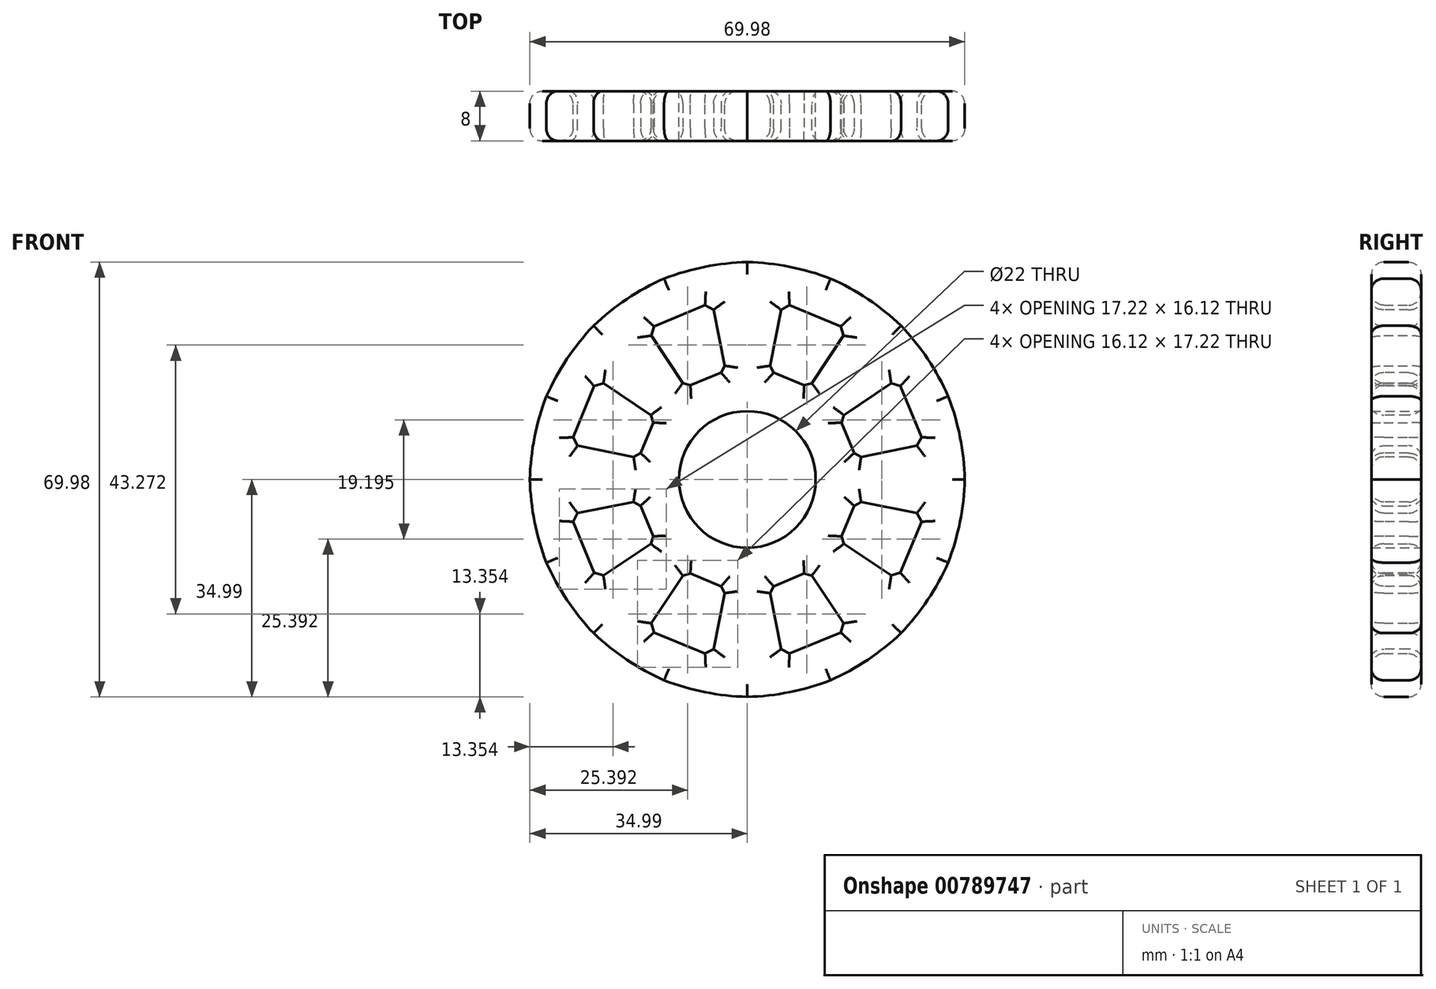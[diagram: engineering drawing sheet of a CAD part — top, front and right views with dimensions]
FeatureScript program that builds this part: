
annotation { "Feature Type Name" : "Feature", "Feature Type Description" : "" }
export const myFeature = defineFeature(function(context is Context, id is Id, definition is map)
    precondition{}
    {
        {
            var Q0;
            Q0=qCreatedBy(makeId("Front.planeOp"),FACE);
            var sketch = newSketch(context, id + "F0", { "sketchPlane" : qUnion([Q0])});
            skCircle(sketch, "E0.cCircle", {"center": v(0, 0) * mm, "radius": 35 * mm, "construction": true});
            skLineSegment(sketch, "E0.0", {"start": v(35, 6.96) * mm, "end": v(35, -6.96) * mm});
            skLineSegment(sketch, "E0.1", {"start": v(35, -6.96) * mm, "end": v(29.67, -19.83) * mm});
            skLineSegment(sketch, "E0.2", {"start": v(29.67, -19.83) * mm, "end": v(19.83, -29.67) * mm});
            skLineSegment(sketch, "E0.3", {"start": v(19.83, -29.67) * mm, "end": v(6.96, -35) * mm});
            skLineSegment(sketch, "E0.4", {"start": v(6.96, -35) * mm, "end": v(-6.96, -35) * mm});
            skLineSegment(sketch, "E0.5", {"start": v(-6.96, -35) * mm, "end": v(-19.83, -29.67) * mm});
            skLineSegment(sketch, "E0.6", {"start": v(-19.83, -29.67) * mm, "end": v(-29.67, -19.83) * mm});
            skLineSegment(sketch, "E0.7", {"start": v(-29.67, -19.83) * mm, "end": v(-35, -6.96) * mm});
            skLineSegment(sketch, "E0.8", {"start": v(-35, -6.96) * mm, "end": v(-35, 6.96) * mm});
            skLineSegment(sketch, "E0.9", {"start": v(-35, 6.96) * mm, "end": v(-29.67, 19.83) * mm});
            skLineSegment(sketch, "E0.10", {"start": v(-29.67, 19.83) * mm, "end": v(-19.83, 29.67) * mm});
            skLineSegment(sketch, "E0.11", {"start": v(-19.83, 29.67) * mm, "end": v(-6.96, 35) * mm});
            skLineSegment(sketch, "E0.12", {"start": v(-6.96, 35) * mm, "end": v(6.96, 35) * mm});
            skLineSegment(sketch, "E0.13", {"start": v(6.96, 35) * mm, "end": v(19.83, 29.67) * mm});
            skLineSegment(sketch, "E0.14", {"start": v(19.83, 29.67) * mm, "end": v(29.67, 19.83) * mm});
            skLineSegment(sketch, "E0.15", {"start": v(29.67, 19.83) * mm, "end": v(35, 6.96) * mm});
            skPoint(sketch, "E0.0.midPoint", {"position": v(35, 0) * mm});
            skCircle(sketch, "E1", {"center": v(0, 0) * mm, "radius": 11 * mm});
            skCircle(sketch, "E2.cCircle", {"center": v(0, 0) * mm, "radius": 28.5 * mm, "construction": true});
            skLineSegment(sketch, "E2.0", {"start": v(28.5, 5.67) * mm, "end": v(28.5, -5.67) * mm});
            skLineSegment(sketch, "E2.1", {"start": v(28.5, -5.67) * mm, "end": v(24.16, -16.14) * mm});
            skLineSegment(sketch, "E2.2", {"start": v(24.16, -16.14) * mm, "end": v(16.14, -24.16) * mm});
            skLineSegment(sketch, "E2.3", {"start": v(16.14, -24.16) * mm, "end": v(5.67, -28.5) * mm});
            skLineSegment(sketch, "E2.4", {"start": v(5.67, -28.5) * mm, "end": v(-5.67, -28.5) * mm});
            skLineSegment(sketch, "E2.5", {"start": v(-5.67, -28.5) * mm, "end": v(-16.14, -24.16) * mm});
            skLineSegment(sketch, "E2.6", {"start": v(-16.14, -24.16) * mm, "end": v(-24.16, -16.14) * mm});
            skLineSegment(sketch, "E2.7", {"start": v(-24.16, -16.14) * mm, "end": v(-28.5, -5.67) * mm});
            skLineSegment(sketch, "E2.8", {"start": v(-28.5, -5.67) * mm, "end": v(-28.5, 5.67) * mm});
            skLineSegment(sketch, "E2.9", {"start": v(-28.5, 5.67) * mm, "end": v(-24.16, 16.14) * mm});
            skLineSegment(sketch, "E2.10", {"start": v(-24.16, 16.14) * mm, "end": v(-16.14, 24.16) * mm});
            skLineSegment(sketch, "E2.11", {"start": v(-16.14, 24.16) * mm, "end": v(-5.67, 28.5) * mm});
            skLineSegment(sketch, "E2.12", {"start": v(-5.67, 28.5) * mm, "end": v(5.67, 28.5) * mm});
            skLineSegment(sketch, "E2.13", {"start": v(5.67, 28.5) * mm, "end": v(16.14, 24.16) * mm});
            skLineSegment(sketch, "E2.14", {"start": v(16.14, 24.16) * mm, "end": v(24.16, 16.14) * mm});
            skLineSegment(sketch, "E2.15", {"start": v(24.16, 16.14) * mm, "end": v(28.5, 5.67) * mm});
            skPoint(sketch, "E2.0.midPoint", {"position": v(28.5, 0) * mm});
            skCircle(sketch, "E3.cCircle", {"center": v(0, 0) * mm, "radius": 17.5 * mm, "construction": true});
            skLineSegment(sketch, "E3.0", {"start": v(17.5, 3.48) * mm, "end": v(17.5, -3.48) * mm});
            skLineSegment(sketch, "E3.1", {"start": v(17.5, -3.48) * mm, "end": v(14.84, -9.91) * mm});
            skLineSegment(sketch, "E3.2", {"start": v(14.84, -9.91) * mm, "end": v(9.91, -14.84) * mm});
            skLineSegment(sketch, "E3.3", {"start": v(9.91, -14.84) * mm, "end": v(3.48, -17.5) * mm});
            skLineSegment(sketch, "E3.4", {"start": v(3.48, -17.5) * mm, "end": v(-3.48, -17.5) * mm});
            skLineSegment(sketch, "E3.5", {"start": v(-3.48, -17.5) * mm, "end": v(-9.91, -14.84) * mm});
            skLineSegment(sketch, "E3.6", {"start": v(-9.91, -14.84) * mm, "end": v(-14.84, -9.91) * mm});
            skLineSegment(sketch, "E3.7", {"start": v(-14.84, -9.91) * mm, "end": v(-17.5, -3.48) * mm});
            skLineSegment(sketch, "E3.8", {"start": v(-17.5, -3.48) * mm, "end": v(-17.5, 3.48) * mm});
            skLineSegment(sketch, "E3.9", {"start": v(-17.5, 3.48) * mm, "end": v(-14.84, 9.91) * mm});
            skLineSegment(sketch, "E3.10", {"start": v(-14.84, 9.91) * mm, "end": v(-9.91, 14.84) * mm});
            skLineSegment(sketch, "E3.11", {"start": v(-9.91, 14.84) * mm, "end": v(-3.48, 17.5) * mm});
            skLineSegment(sketch, "E3.12", {"start": v(-3.48, 17.5) * mm, "end": v(3.48, 17.5) * mm});
            skLineSegment(sketch, "E3.13", {"start": v(3.48, 17.5) * mm, "end": v(9.91, 14.84) * mm});
            skLineSegment(sketch, "E3.14", {"start": v(9.91, 14.84) * mm, "end": v(14.84, 9.91) * mm});
            skLineSegment(sketch, "E3.15", {"start": v(14.84, 9.91) * mm, "end": v(17.5, 3.48) * mm});
            skPoint(sketch, "E3.0.midPoint", {"position": v(17.5, 0) * mm});
            skLineSegment(sketch, "E4", {"start": v(-3.48, 17.5) * mm, "end": v(-5.67, 28.5) * mm});
            skLineSegment(sketch, "E5", {"start": v(3.48, 17.5) * mm, "end": v(5.67, 28.5) * mm});
            skLineSegment(sketch, "E6", {"start": v(9.91, 14.84) * mm, "end": v(16.14, 24.16) * mm});
            skLineSegment(sketch, "E7", {"start": v(14.84, 9.91) * mm, "end": v(24.16, 16.14) * mm});
            skLineSegment(sketch, "E8", {"start": v(17.5, 3.48) * mm, "end": v(28.5, 5.67) * mm});
            skLineSegment(sketch, "E9", {"start": v(17.5, -3.48) * mm, "end": v(28.5, -5.67) * mm});
            skLineSegment(sketch, "E10", {"start": v(14.84, -9.91) * mm, "end": v(24.16, -16.14) * mm});
            skLineSegment(sketch, "E11", {"start": v(9.91, -14.84) * mm, "end": v(16.14, -24.16) * mm});
            skLineSegment(sketch, "E12", {"start": v(3.48, -17.5) * mm, "end": v(5.67, -28.5) * mm});
            skLineSegment(sketch, "E13", {"start": v(-3.48, -17.5) * mm, "end": v(-5.67, -28.5) * mm});
            skLineSegment(sketch, "E14", {"start": v(-9.91, -14.84) * mm, "end": v(-16.14, -24.16) * mm});
            skLineSegment(sketch, "E15", {"start": v(-14.84, -9.91) * mm, "end": v(-24.16, -16.14) * mm});
            skLineSegment(sketch, "E16", {"start": v(-17.5, -3.48) * mm, "end": v(-28.5, -5.67) * mm});
            skLineSegment(sketch, "E17", {"start": v(-17.5, 3.48) * mm, "end": v(-28.5, 5.67) * mm});
            skLineSegment(sketch, "E18", {"start": v(-14.84, 9.91) * mm, "end": v(-24.16, 16.14) * mm});
            skLineSegment(sketch, "E19", {"start": v(-9.91, 14.84) * mm, "end": v(-16.14, 24.16) * mm});
            skSolve(sketch);
        }
        {
            var Q0;
            Q0=makeQuery(id+"F0.imprint","IMPRINT",FACE,{"disambiguationData":[TD([[makeQuery(id+"F0.imprint","IMPRINT",EDGE,{"derivedFrom":sQuery(id+"F0.wireOp",EDGE,"E0.0")}),-1.0]])]});
            var Q1;
            Q1=makeQuery(id+"F0.imprint","IMPRINT",FACE,{"disambiguationData":[TD([[makeQuery(id+"F0.imprint","IMPRINT",EDGE,{"derivedFrom":sQuery(id+"F0.wireOp",EDGE,"E2.10")}),-1.0]])]});
            var Q2;
            Q2=makeQuery(id+"F0.imprint","IMPRINT",FACE,{"disambiguationData":[TD([[makeQuery(id+"F0.imprint","IMPRINT",EDGE,{"derivedFrom":sQuery(id+"F0.wireOp",EDGE,"E2.12")}),-1.0]])]});
            var Q3;
            Q3=makeQuery(id+"F0.imprint","IMPRINT",FACE,{"disambiguationData":[TD([[makeQuery(id+"F0.imprint","IMPRINT",EDGE,{"derivedFrom":sQuery(id+"F0.wireOp",EDGE,"E2.14")}),-1.0]])]});
            var Q4;
            Q4=makeQuery(id+"F0.imprint","IMPRINT",FACE,{"disambiguationData":[TD([[makeQuery(id+"F0.imprint","IMPRINT",EDGE,{"derivedFrom":sQuery(id+"F0.wireOp",EDGE,"E2.0")}),-1.0]])]});
            var Q5;
            Q5=makeQuery(id+"F0.imprint","IMPRINT",FACE,{"disambiguationData":[TD([[makeQuery(id+"F0.imprint","IMPRINT",EDGE,{"derivedFrom":sQuery(id+"F0.wireOp",EDGE,"E2.2")}),-1.0]])]});
            var Q6;
            Q6=makeQuery(id+"F0.imprint","IMPRINT",FACE,{"disambiguationData":[TD([[makeQuery(id+"F0.imprint","IMPRINT",EDGE,{"derivedFrom":sQuery(id+"F0.wireOp",EDGE,"E2.4")}),-1.0]])]});
            var Q7;
            Q7=makeQuery(id+"F0.imprint","IMPRINT",FACE,{"disambiguationData":[TD([[makeQuery(id+"F0.imprint","IMPRINT",EDGE,{"derivedFrom":sQuery(id+"F0.wireOp",EDGE,"E2.6")}),-1.0]])]});
            var Q8;
            Q8=makeQuery(id+"F0.imprint","IMPRINT",FACE,{"disambiguationData":[TD([[makeQuery(id+"F0.imprint","IMPRINT",EDGE,{"derivedFrom":sQuery(id+"F0.wireOp",EDGE,"E2.8")}),-1.0]])]});
            var Q9;
            Q9=makeQuery(id+"F0.imprint","IMPRINT",FACE,{"disambiguationData":[TD([[makeQuery(id+"F0.imprint","IMPRINT",EDGE,{"derivedFrom":sQuery(id+"F0.wireOp",EDGE,"E1")}),-1.0]])]});
            extrude(context, id + "F1", {"entities" : qUnion([Q0, Q1, Q2, Q3, Q4, Q5, Q6, Q7, Q8, Q9]), "depth" : 4 * mm, "offsetDistance" : 25 * mm});
        }
        {
            var Q0;
            Q0=makeQuery(id+"F1.opExtrude","SWEPT_EDGE",EDGE,{"disambiguationData":[OSD([sQuery(id+"F0.wireOp",EDGE,"E0.11"),sQuery(id+"F0.wireOp",EDGE,"E0.12")])]});
            var Q1;
            Q1=makeQuery(id+"F1.opExtrude","SWEPT_EDGE",EDGE,{"disambiguationData":[OSD([sQuery(id+"F0.wireOp",EDGE,"E0.12"),sQuery(id+"F0.wireOp",EDGE,"E0.13")])]});
            var Q2;
            Q2=makeQuery(id+"F1.opExtrude","SWEPT_EDGE",EDGE,{"disambiguationData":[OSD([sQuery(id+"F0.wireOp",EDGE,"E0.13"),sQuery(id+"F0.wireOp",EDGE,"E0.14")])]});
            var Q3;
            Q3=makeQuery(id+"F1.opExtrude","SWEPT_EDGE",EDGE,{"disambiguationData":[OSD([sQuery(id+"F0.wireOp",EDGE,"E0.10"),sQuery(id+"F0.wireOp",EDGE,"E0.11")])]});
            var Q4;
            Q4=makeQuery(id+"F1.opExtrude","SWEPT_EDGE",EDGE,{"disambiguationData":[OSD([sQuery(id+"F0.wireOp",EDGE,"E0.9"),sQuery(id+"F0.wireOp",EDGE,"E0.10")])]});
            var Q5;
            Q5=makeQuery(id+"F1.opExtrude","SWEPT_EDGE",EDGE,{"disambiguationData":[OSD([sQuery(id+"F0.wireOp",EDGE,"E0.8"),sQuery(id+"F0.wireOp",EDGE,"E0.9")])]});
            var Q6;
            Q6=makeQuery(id+"F1.opExtrude","SWEPT_EDGE",EDGE,{"disambiguationData":[OSD([sQuery(id+"F0.wireOp",EDGE,"E0.7"),sQuery(id+"F0.wireOp",EDGE,"E0.8")])]});
            var Q7;
            Q7=makeQuery(id+"F1.opExtrude","SWEPT_EDGE",EDGE,{"disambiguationData":[OSD([sQuery(id+"F0.wireOp",EDGE,"E0.6"),sQuery(id+"F0.wireOp",EDGE,"E0.7")])]});
            var Q8;
            Q8=makeQuery(id+"F1.opExtrude","SWEPT_EDGE",EDGE,{"disambiguationData":[OSD([sQuery(id+"F0.wireOp",EDGE,"E0.5"),sQuery(id+"F0.wireOp",EDGE,"E0.6")])]});
            var Q9;
            Q9=makeQuery(id+"F1.opExtrude","SWEPT_EDGE",EDGE,{"disambiguationData":[OSD([sQuery(id+"F0.wireOp",EDGE,"E0.4"),sQuery(id+"F0.wireOp",EDGE,"E0.5")])]});
            var Q10;
            Q10=makeQuery(id+"F1.opExtrude","SWEPT_EDGE",EDGE,{"disambiguationData":[OSD([sQuery(id+"F0.wireOp",EDGE,"E0.3"),sQuery(id+"F0.wireOp",EDGE,"E0.4")])]});
            var Q11;
            Q11=makeQuery(id+"F1.opExtrude","SWEPT_EDGE",EDGE,{"disambiguationData":[OSD([sQuery(id+"F0.wireOp",EDGE,"E0.2"),sQuery(id+"F0.wireOp",EDGE,"E0.3")])]});
            var Q12;
            Q12=makeQuery(id+"F1.opExtrude","SWEPT_EDGE",EDGE,{"disambiguationData":[OSD([sQuery(id+"F0.wireOp",EDGE,"E0.1"),sQuery(id+"F0.wireOp",EDGE,"E0.2")])]});
            var Q13;
            Q13=makeQuery(id+"F1.opExtrude","SWEPT_EDGE",EDGE,{"disambiguationData":[OSD([sQuery(id+"F0.wireOp",EDGE,"E0.0"),sQuery(id+"F0.wireOp",EDGE,"E0.1")])]});
            var Q14;
            Q14=makeQuery(id+"F1.opExtrude","SWEPT_EDGE",EDGE,{"disambiguationData":[OSD([sQuery(id+"F0.wireOp",EDGE,"E0.0"),sQuery(id+"F0.wireOp",EDGE,"E0.15")])]});
            var Q15;
            Q15=makeQuery(id+"F1.opExtrude","SWEPT_EDGE",EDGE,{"disambiguationData":[OSD([sQuery(id+"F0.wireOp",EDGE,"E0.14"),sQuery(id+"F0.wireOp",EDGE,"E0.15")])]});
            fillet(context, id + "F2", {"entities" : qUnion([Q0, Q1, Q2, Q3, Q4, Q5, Q6, Q7, Q8, Q9, Q10, Q11, Q12, Q13, Q14, Q15]), "radius" : 40 * mm, "tangentPropagation" : true, "allowEdgeOverflow" : false});
        }
        {
            var Q0;
            {var subQ0=sQuery(id+"F0.wireOp",EDGE,"E0.5");var subQ1=sQuery(id+"F0.wireOp",EDGE,"E0.4");Q0=makeQuery(id+"F2.opFillet","BLEND_EDGE",EDGE,{"blendedFrom":[makeQuery(id+"F1.opExtrude","SWEPT_EDGE",EDGE,{"disambiguationData":[OSD([subQ1,subQ0])]}),makeQuery(id+"F1.opExtrude","CAP_FACE",FACE,{"disambiguationData":[OSD([sQuery(id+"F0.wireOp",EDGE,"E0.0"),sQuery(id+"F0.wireOp",EDGE,"E0.1"),sQuery(id+"F0.wireOp",EDGE,"E0.2"),sQuery(id+"F0.wireOp",EDGE,"E0.3"),subQ1,subQ0,sQuery(id+"F0.wireOp",EDGE,"E0.6"),sQuery(id+"F0.wireOp",EDGE,"E0.7"),sQuery(id+"F0.wireOp",EDGE,"E0.8"),sQuery(id+"F0.wireOp",EDGE,"E0.9"),sQuery(id+"F0.wireOp",EDGE,"E0.10"),sQuery(id+"F0.wireOp",EDGE,"E0.11"),sQuery(id+"F0.wireOp",EDGE,"E0.12"),sQuery(id+"F0.wireOp",EDGE,"E0.13"),sQuery(id+"F0.wireOp",EDGE,"E0.14"),sQuery(id+"F0.wireOp",EDGE,"E0.15"),sQuery(id+"F0.wireOp",EDGE,"E1"),sQuery(id+"F0.wireOp",EDGE,"E2.1"),sQuery(id+"F0.wireOp",EDGE,"E2.3"),sQuery(id+"F0.wireOp",EDGE,"E2.5"),sQuery(id+"F0.wireOp",EDGE,"E2.7"),sQuery(id+"F0.wireOp",EDGE,"E2.9"),sQuery(id+"F0.wireOp",EDGE,"E2.11"),sQuery(id+"F0.wireOp",EDGE,"E2.13"),sQuery(id+"F0.wireOp",EDGE,"E2.15"),sQuery(id+"F0.wireOp",EDGE,"E3.1"),sQuery(id+"F0.wireOp",EDGE,"E3.3"),sQuery(id+"F0.wireOp",EDGE,"E3.5"),sQuery(id+"F0.wireOp",EDGE,"E3.7"),sQuery(id+"F0.wireOp",EDGE,"E3.9"),sQuery(id+"F0.wireOp",EDGE,"E3.11"),sQuery(id+"F0.wireOp",EDGE,"E3.13"),sQuery(id+"F0.wireOp",EDGE,"E3.15"),sQuery(id+"F0.wireOp",EDGE,"E4"),sQuery(id+"F0.wireOp",EDGE,"E5"),sQuery(id+"F0.wireOp",EDGE,"E6"),sQuery(id+"F0.wireOp",EDGE,"E7"),sQuery(id+"F0.wireOp",EDGE,"E8"),sQuery(id+"F0.wireOp",EDGE,"E9"),sQuery(id+"F0.wireOp",EDGE,"E10"),sQuery(id+"F0.wireOp",EDGE,"E11"),sQuery(id+"F0.wireOp",EDGE,"E12"),sQuery(id+"F0.wireOp",EDGE,"E13"),sQuery(id+"F0.wireOp",EDGE,"E14"),sQuery(id+"F0.wireOp",EDGE,"E15"),sQuery(id+"F0.wireOp",EDGE,"E16"),sQuery(id+"F0.wireOp",EDGE,"E17"),sQuery(id+"F0.wireOp",EDGE,"E18"),sQuery(id+"F0.wireOp",EDGE,"E19")])],"isStart":true})],"blendedInto":[makeQuery(id+"F1.opExtrude","CAP_FACE",FACE,{"disambiguationData":[OSD([sQuery(id+"F0.wireOp",EDGE,"E0.0"),sQuery(id+"F0.wireOp",EDGE,"E0.1"),sQuery(id+"F0.wireOp",EDGE,"E0.2"),sQuery(id+"F0.wireOp",EDGE,"E0.3"),subQ1,subQ0,sQuery(id+"F0.wireOp",EDGE,"E0.6"),sQuery(id+"F0.wireOp",EDGE,"E0.7"),sQuery(id+"F0.wireOp",EDGE,"E0.8"),sQuery(id+"F0.wireOp",EDGE,"E0.9"),sQuery(id+"F0.wireOp",EDGE,"E0.10"),sQuery(id+"F0.wireOp",EDGE,"E0.11"),sQuery(id+"F0.wireOp",EDGE,"E0.12"),sQuery(id+"F0.wireOp",EDGE,"E0.13"),sQuery(id+"F0.wireOp",EDGE,"E0.14"),sQuery(id+"F0.wireOp",EDGE,"E0.15"),sQuery(id+"F0.wireOp",EDGE,"E1"),sQuery(id+"F0.wireOp",EDGE,"E2.1"),sQuery(id+"F0.wireOp",EDGE,"E2.3"),sQuery(id+"F0.wireOp",EDGE,"E2.5"),sQuery(id+"F0.wireOp",EDGE,"E2.7"),sQuery(id+"F0.wireOp",EDGE,"E2.9"),sQuery(id+"F0.wireOp",EDGE,"E2.11"),sQuery(id+"F0.wireOp",EDGE,"E2.13"),sQuery(id+"F0.wireOp",EDGE,"E2.15"),sQuery(id+"F0.wireOp",EDGE,"E3.1"),sQuery(id+"F0.wireOp",EDGE,"E3.3"),sQuery(id+"F0.wireOp",EDGE,"E3.5"),sQuery(id+"F0.wireOp",EDGE,"E3.7"),sQuery(id+"F0.wireOp",EDGE,"E3.9"),sQuery(id+"F0.wireOp",EDGE,"E3.11"),sQuery(id+"F0.wireOp",EDGE,"E3.13"),sQuery(id+"F0.wireOp",EDGE,"E3.15"),sQuery(id+"F0.wireOp",EDGE,"E4"),sQuery(id+"F0.wireOp",EDGE,"E5"),sQuery(id+"F0.wireOp",EDGE,"E6"),sQuery(id+"F0.wireOp",EDGE,"E7"),sQuery(id+"F0.wireOp",EDGE,"E8"),sQuery(id+"F0.wireOp",EDGE,"E9"),sQuery(id+"F0.wireOp",EDGE,"E10"),sQuery(id+"F0.wireOp",EDGE,"E11"),sQuery(id+"F0.wireOp",EDGE,"E12"),sQuery(id+"F0.wireOp",EDGE,"E13"),sQuery(id+"F0.wireOp",EDGE,"E14"),sQuery(id+"F0.wireOp",EDGE,"E15"),sQuery(id+"F0.wireOp",EDGE,"E16"),sQuery(id+"F0.wireOp",EDGE,"E17"),sQuery(id+"F0.wireOp",EDGE,"E18"),sQuery(id+"F0.wireOp",EDGE,"E19")])],"isStart":true})]});}
            var Q1;
            {var subQ0=sQuery(id+"F0.wireOp",EDGE,"E0.4");var subQ1=sQuery(id+"F0.wireOp",EDGE,"E0.3");Q1=makeQuery(id+"F2.opFillet","BLEND_EDGE",EDGE,{"blendedFrom":[makeQuery(id+"F1.opExtrude","SWEPT_EDGE",EDGE,{"disambiguationData":[OSD([subQ1,subQ0])]}),makeQuery(id+"F1.opExtrude","CAP_FACE",FACE,{"disambiguationData":[OSD([sQuery(id+"F0.wireOp",EDGE,"E0.0"),sQuery(id+"F0.wireOp",EDGE,"E0.1"),sQuery(id+"F0.wireOp",EDGE,"E0.2"),subQ1,subQ0,sQuery(id+"F0.wireOp",EDGE,"E0.5"),sQuery(id+"F0.wireOp",EDGE,"E0.6"),sQuery(id+"F0.wireOp",EDGE,"E0.7"),sQuery(id+"F0.wireOp",EDGE,"E0.8"),sQuery(id+"F0.wireOp",EDGE,"E0.9"),sQuery(id+"F0.wireOp",EDGE,"E0.10"),sQuery(id+"F0.wireOp",EDGE,"E0.11"),sQuery(id+"F0.wireOp",EDGE,"E0.12"),sQuery(id+"F0.wireOp",EDGE,"E0.13"),sQuery(id+"F0.wireOp",EDGE,"E0.14"),sQuery(id+"F0.wireOp",EDGE,"E0.15"),sQuery(id+"F0.wireOp",EDGE,"E1"),sQuery(id+"F0.wireOp",EDGE,"E2.1"),sQuery(id+"F0.wireOp",EDGE,"E2.3"),sQuery(id+"F0.wireOp",EDGE,"E2.5"),sQuery(id+"F0.wireOp",EDGE,"E2.7"),sQuery(id+"F0.wireOp",EDGE,"E2.9"),sQuery(id+"F0.wireOp",EDGE,"E2.11"),sQuery(id+"F0.wireOp",EDGE,"E2.13"),sQuery(id+"F0.wireOp",EDGE,"E2.15"),sQuery(id+"F0.wireOp",EDGE,"E3.1"),sQuery(id+"F0.wireOp",EDGE,"E3.3"),sQuery(id+"F0.wireOp",EDGE,"E3.5"),sQuery(id+"F0.wireOp",EDGE,"E3.7"),sQuery(id+"F0.wireOp",EDGE,"E3.9"),sQuery(id+"F0.wireOp",EDGE,"E3.11"),sQuery(id+"F0.wireOp",EDGE,"E3.13"),sQuery(id+"F0.wireOp",EDGE,"E3.15"),sQuery(id+"F0.wireOp",EDGE,"E4"),sQuery(id+"F0.wireOp",EDGE,"E5"),sQuery(id+"F0.wireOp",EDGE,"E6"),sQuery(id+"F0.wireOp",EDGE,"E7"),sQuery(id+"F0.wireOp",EDGE,"E8"),sQuery(id+"F0.wireOp",EDGE,"E9"),sQuery(id+"F0.wireOp",EDGE,"E10"),sQuery(id+"F0.wireOp",EDGE,"E11"),sQuery(id+"F0.wireOp",EDGE,"E12"),sQuery(id+"F0.wireOp",EDGE,"E13"),sQuery(id+"F0.wireOp",EDGE,"E14"),sQuery(id+"F0.wireOp",EDGE,"E15"),sQuery(id+"F0.wireOp",EDGE,"E16"),sQuery(id+"F0.wireOp",EDGE,"E17"),sQuery(id+"F0.wireOp",EDGE,"E18"),sQuery(id+"F0.wireOp",EDGE,"E19")])],"isStart":true})],"blendedInto":[makeQuery(id+"F1.opExtrude","CAP_FACE",FACE,{"disambiguationData":[OSD([sQuery(id+"F0.wireOp",EDGE,"E0.0"),sQuery(id+"F0.wireOp",EDGE,"E0.1"),sQuery(id+"F0.wireOp",EDGE,"E0.2"),subQ1,subQ0,sQuery(id+"F0.wireOp",EDGE,"E0.5"),sQuery(id+"F0.wireOp",EDGE,"E0.6"),sQuery(id+"F0.wireOp",EDGE,"E0.7"),sQuery(id+"F0.wireOp",EDGE,"E0.8"),sQuery(id+"F0.wireOp",EDGE,"E0.9"),sQuery(id+"F0.wireOp",EDGE,"E0.10"),sQuery(id+"F0.wireOp",EDGE,"E0.11"),sQuery(id+"F0.wireOp",EDGE,"E0.12"),sQuery(id+"F0.wireOp",EDGE,"E0.13"),sQuery(id+"F0.wireOp",EDGE,"E0.14"),sQuery(id+"F0.wireOp",EDGE,"E0.15"),sQuery(id+"F0.wireOp",EDGE,"E1"),sQuery(id+"F0.wireOp",EDGE,"E2.1"),sQuery(id+"F0.wireOp",EDGE,"E2.3"),sQuery(id+"F0.wireOp",EDGE,"E2.5"),sQuery(id+"F0.wireOp",EDGE,"E2.7"),sQuery(id+"F0.wireOp",EDGE,"E2.9"),sQuery(id+"F0.wireOp",EDGE,"E2.11"),sQuery(id+"F0.wireOp",EDGE,"E2.13"),sQuery(id+"F0.wireOp",EDGE,"E2.15"),sQuery(id+"F0.wireOp",EDGE,"E3.1"),sQuery(id+"F0.wireOp",EDGE,"E3.3"),sQuery(id+"F0.wireOp",EDGE,"E3.5"),sQuery(id+"F0.wireOp",EDGE,"E3.7"),sQuery(id+"F0.wireOp",EDGE,"E3.9"),sQuery(id+"F0.wireOp",EDGE,"E3.11"),sQuery(id+"F0.wireOp",EDGE,"E3.13"),sQuery(id+"F0.wireOp",EDGE,"E3.15"),sQuery(id+"F0.wireOp",EDGE,"E4"),sQuery(id+"F0.wireOp",EDGE,"E5"),sQuery(id+"F0.wireOp",EDGE,"E6"),sQuery(id+"F0.wireOp",EDGE,"E7"),sQuery(id+"F0.wireOp",EDGE,"E8"),sQuery(id+"F0.wireOp",EDGE,"E9"),sQuery(id+"F0.wireOp",EDGE,"E10"),sQuery(id+"F0.wireOp",EDGE,"E11"),sQuery(id+"F0.wireOp",EDGE,"E12"),sQuery(id+"F0.wireOp",EDGE,"E13"),sQuery(id+"F0.wireOp",EDGE,"E14"),sQuery(id+"F0.wireOp",EDGE,"E15"),sQuery(id+"F0.wireOp",EDGE,"E16"),sQuery(id+"F0.wireOp",EDGE,"E17"),sQuery(id+"F0.wireOp",EDGE,"E18"),sQuery(id+"F0.wireOp",EDGE,"E19")])],"isStart":true})]});}
            var Q2;
            {var subQ0=sQuery(id+"F0.wireOp",EDGE,"E0.3");var subQ1=sQuery(id+"F0.wireOp",EDGE,"E0.2");Q2=makeQuery(id+"F2.opFillet","BLEND_EDGE",EDGE,{"blendedFrom":[makeQuery(id+"F1.opExtrude","SWEPT_EDGE",EDGE,{"disambiguationData":[OSD([subQ1,subQ0])]}),makeQuery(id+"F1.opExtrude","CAP_FACE",FACE,{"disambiguationData":[OSD([sQuery(id+"F0.wireOp",EDGE,"E0.0"),sQuery(id+"F0.wireOp",EDGE,"E0.1"),subQ1,subQ0,sQuery(id+"F0.wireOp",EDGE,"E0.4"),sQuery(id+"F0.wireOp",EDGE,"E0.5"),sQuery(id+"F0.wireOp",EDGE,"E0.6"),sQuery(id+"F0.wireOp",EDGE,"E0.7"),sQuery(id+"F0.wireOp",EDGE,"E0.8"),sQuery(id+"F0.wireOp",EDGE,"E0.9"),sQuery(id+"F0.wireOp",EDGE,"E0.10"),sQuery(id+"F0.wireOp",EDGE,"E0.11"),sQuery(id+"F0.wireOp",EDGE,"E0.12"),sQuery(id+"F0.wireOp",EDGE,"E0.13"),sQuery(id+"F0.wireOp",EDGE,"E0.14"),sQuery(id+"F0.wireOp",EDGE,"E0.15"),sQuery(id+"F0.wireOp",EDGE,"E1"),sQuery(id+"F0.wireOp",EDGE,"E2.1"),sQuery(id+"F0.wireOp",EDGE,"E2.3"),sQuery(id+"F0.wireOp",EDGE,"E2.5"),sQuery(id+"F0.wireOp",EDGE,"E2.7"),sQuery(id+"F0.wireOp",EDGE,"E2.9"),sQuery(id+"F0.wireOp",EDGE,"E2.11"),sQuery(id+"F0.wireOp",EDGE,"E2.13"),sQuery(id+"F0.wireOp",EDGE,"E2.15"),sQuery(id+"F0.wireOp",EDGE,"E3.1"),sQuery(id+"F0.wireOp",EDGE,"E3.3"),sQuery(id+"F0.wireOp",EDGE,"E3.5"),sQuery(id+"F0.wireOp",EDGE,"E3.7"),sQuery(id+"F0.wireOp",EDGE,"E3.9"),sQuery(id+"F0.wireOp",EDGE,"E3.11"),sQuery(id+"F0.wireOp",EDGE,"E3.13"),sQuery(id+"F0.wireOp",EDGE,"E3.15"),sQuery(id+"F0.wireOp",EDGE,"E4"),sQuery(id+"F0.wireOp",EDGE,"E5"),sQuery(id+"F0.wireOp",EDGE,"E6"),sQuery(id+"F0.wireOp",EDGE,"E7"),sQuery(id+"F0.wireOp",EDGE,"E8"),sQuery(id+"F0.wireOp",EDGE,"E9"),sQuery(id+"F0.wireOp",EDGE,"E10"),sQuery(id+"F0.wireOp",EDGE,"E11"),sQuery(id+"F0.wireOp",EDGE,"E12"),sQuery(id+"F0.wireOp",EDGE,"E13"),sQuery(id+"F0.wireOp",EDGE,"E14"),sQuery(id+"F0.wireOp",EDGE,"E15"),sQuery(id+"F0.wireOp",EDGE,"E16"),sQuery(id+"F0.wireOp",EDGE,"E17"),sQuery(id+"F0.wireOp",EDGE,"E18"),sQuery(id+"F0.wireOp",EDGE,"E19")])],"isStart":true})],"blendedInto":[makeQuery(id+"F1.opExtrude","CAP_FACE",FACE,{"disambiguationData":[OSD([sQuery(id+"F0.wireOp",EDGE,"E0.0"),sQuery(id+"F0.wireOp",EDGE,"E0.1"),subQ1,subQ0,sQuery(id+"F0.wireOp",EDGE,"E0.4"),sQuery(id+"F0.wireOp",EDGE,"E0.5"),sQuery(id+"F0.wireOp",EDGE,"E0.6"),sQuery(id+"F0.wireOp",EDGE,"E0.7"),sQuery(id+"F0.wireOp",EDGE,"E0.8"),sQuery(id+"F0.wireOp",EDGE,"E0.9"),sQuery(id+"F0.wireOp",EDGE,"E0.10"),sQuery(id+"F0.wireOp",EDGE,"E0.11"),sQuery(id+"F0.wireOp",EDGE,"E0.12"),sQuery(id+"F0.wireOp",EDGE,"E0.13"),sQuery(id+"F0.wireOp",EDGE,"E0.14"),sQuery(id+"F0.wireOp",EDGE,"E0.15"),sQuery(id+"F0.wireOp",EDGE,"E1"),sQuery(id+"F0.wireOp",EDGE,"E2.1"),sQuery(id+"F0.wireOp",EDGE,"E2.3"),sQuery(id+"F0.wireOp",EDGE,"E2.5"),sQuery(id+"F0.wireOp",EDGE,"E2.7"),sQuery(id+"F0.wireOp",EDGE,"E2.9"),sQuery(id+"F0.wireOp",EDGE,"E2.11"),sQuery(id+"F0.wireOp",EDGE,"E2.13"),sQuery(id+"F0.wireOp",EDGE,"E2.15"),sQuery(id+"F0.wireOp",EDGE,"E3.1"),sQuery(id+"F0.wireOp",EDGE,"E3.3"),sQuery(id+"F0.wireOp",EDGE,"E3.5"),sQuery(id+"F0.wireOp",EDGE,"E3.7"),sQuery(id+"F0.wireOp",EDGE,"E3.9"),sQuery(id+"F0.wireOp",EDGE,"E3.11"),sQuery(id+"F0.wireOp",EDGE,"E3.13"),sQuery(id+"F0.wireOp",EDGE,"E3.15"),sQuery(id+"F0.wireOp",EDGE,"E4"),sQuery(id+"F0.wireOp",EDGE,"E5"),sQuery(id+"F0.wireOp",EDGE,"E6"),sQuery(id+"F0.wireOp",EDGE,"E7"),sQuery(id+"F0.wireOp",EDGE,"E8"),sQuery(id+"F0.wireOp",EDGE,"E9"),sQuery(id+"F0.wireOp",EDGE,"E10"),sQuery(id+"F0.wireOp",EDGE,"E11"),sQuery(id+"F0.wireOp",EDGE,"E12"),sQuery(id+"F0.wireOp",EDGE,"E13"),sQuery(id+"F0.wireOp",EDGE,"E14"),sQuery(id+"F0.wireOp",EDGE,"E15"),sQuery(id+"F0.wireOp",EDGE,"E16"),sQuery(id+"F0.wireOp",EDGE,"E17"),sQuery(id+"F0.wireOp",EDGE,"E18"),sQuery(id+"F0.wireOp",EDGE,"E19")])],"isStart":true})]});}
            var Q3;
            {var subQ0=sQuery(id+"F0.wireOp",EDGE,"E0.2");var subQ1=sQuery(id+"F0.wireOp",EDGE,"E0.1");Q3=makeQuery(id+"F2.opFillet","BLEND_EDGE",EDGE,{"blendedFrom":[makeQuery(id+"F1.opExtrude","SWEPT_EDGE",EDGE,{"disambiguationData":[OSD([subQ1,subQ0])]}),makeQuery(id+"F1.opExtrude","CAP_FACE",FACE,{"disambiguationData":[OSD([sQuery(id+"F0.wireOp",EDGE,"E0.0"),subQ1,subQ0,sQuery(id+"F0.wireOp",EDGE,"E0.3"),sQuery(id+"F0.wireOp",EDGE,"E0.4"),sQuery(id+"F0.wireOp",EDGE,"E0.5"),sQuery(id+"F0.wireOp",EDGE,"E0.6"),sQuery(id+"F0.wireOp",EDGE,"E0.7"),sQuery(id+"F0.wireOp",EDGE,"E0.8"),sQuery(id+"F0.wireOp",EDGE,"E0.9"),sQuery(id+"F0.wireOp",EDGE,"E0.10"),sQuery(id+"F0.wireOp",EDGE,"E0.11"),sQuery(id+"F0.wireOp",EDGE,"E0.12"),sQuery(id+"F0.wireOp",EDGE,"E0.13"),sQuery(id+"F0.wireOp",EDGE,"E0.14"),sQuery(id+"F0.wireOp",EDGE,"E0.15"),sQuery(id+"F0.wireOp",EDGE,"E1"),sQuery(id+"F0.wireOp",EDGE,"E2.1"),sQuery(id+"F0.wireOp",EDGE,"E2.3"),sQuery(id+"F0.wireOp",EDGE,"E2.5"),sQuery(id+"F0.wireOp",EDGE,"E2.7"),sQuery(id+"F0.wireOp",EDGE,"E2.9"),sQuery(id+"F0.wireOp",EDGE,"E2.11"),sQuery(id+"F0.wireOp",EDGE,"E2.13"),sQuery(id+"F0.wireOp",EDGE,"E2.15"),sQuery(id+"F0.wireOp",EDGE,"E3.1"),sQuery(id+"F0.wireOp",EDGE,"E3.3"),sQuery(id+"F0.wireOp",EDGE,"E3.5"),sQuery(id+"F0.wireOp",EDGE,"E3.7"),sQuery(id+"F0.wireOp",EDGE,"E3.9"),sQuery(id+"F0.wireOp",EDGE,"E3.11"),sQuery(id+"F0.wireOp",EDGE,"E3.13"),sQuery(id+"F0.wireOp",EDGE,"E3.15"),sQuery(id+"F0.wireOp",EDGE,"E4"),sQuery(id+"F0.wireOp",EDGE,"E5"),sQuery(id+"F0.wireOp",EDGE,"E6"),sQuery(id+"F0.wireOp",EDGE,"E7"),sQuery(id+"F0.wireOp",EDGE,"E8"),sQuery(id+"F0.wireOp",EDGE,"E9"),sQuery(id+"F0.wireOp",EDGE,"E10"),sQuery(id+"F0.wireOp",EDGE,"E11"),sQuery(id+"F0.wireOp",EDGE,"E12"),sQuery(id+"F0.wireOp",EDGE,"E13"),sQuery(id+"F0.wireOp",EDGE,"E14"),sQuery(id+"F0.wireOp",EDGE,"E15"),sQuery(id+"F0.wireOp",EDGE,"E16"),sQuery(id+"F0.wireOp",EDGE,"E17"),sQuery(id+"F0.wireOp",EDGE,"E18"),sQuery(id+"F0.wireOp",EDGE,"E19")])],"isStart":true})],"blendedInto":[makeQuery(id+"F1.opExtrude","CAP_FACE",FACE,{"disambiguationData":[OSD([sQuery(id+"F0.wireOp",EDGE,"E0.0"),subQ1,subQ0,sQuery(id+"F0.wireOp",EDGE,"E0.3"),sQuery(id+"F0.wireOp",EDGE,"E0.4"),sQuery(id+"F0.wireOp",EDGE,"E0.5"),sQuery(id+"F0.wireOp",EDGE,"E0.6"),sQuery(id+"F0.wireOp",EDGE,"E0.7"),sQuery(id+"F0.wireOp",EDGE,"E0.8"),sQuery(id+"F0.wireOp",EDGE,"E0.9"),sQuery(id+"F0.wireOp",EDGE,"E0.10"),sQuery(id+"F0.wireOp",EDGE,"E0.11"),sQuery(id+"F0.wireOp",EDGE,"E0.12"),sQuery(id+"F0.wireOp",EDGE,"E0.13"),sQuery(id+"F0.wireOp",EDGE,"E0.14"),sQuery(id+"F0.wireOp",EDGE,"E0.15"),sQuery(id+"F0.wireOp",EDGE,"E1"),sQuery(id+"F0.wireOp",EDGE,"E2.1"),sQuery(id+"F0.wireOp",EDGE,"E2.3"),sQuery(id+"F0.wireOp",EDGE,"E2.5"),sQuery(id+"F0.wireOp",EDGE,"E2.7"),sQuery(id+"F0.wireOp",EDGE,"E2.9"),sQuery(id+"F0.wireOp",EDGE,"E2.11"),sQuery(id+"F0.wireOp",EDGE,"E2.13"),sQuery(id+"F0.wireOp",EDGE,"E2.15"),sQuery(id+"F0.wireOp",EDGE,"E3.1"),sQuery(id+"F0.wireOp",EDGE,"E3.3"),sQuery(id+"F0.wireOp",EDGE,"E3.5"),sQuery(id+"F0.wireOp",EDGE,"E3.7"),sQuery(id+"F0.wireOp",EDGE,"E3.9"),sQuery(id+"F0.wireOp",EDGE,"E3.11"),sQuery(id+"F0.wireOp",EDGE,"E3.13"),sQuery(id+"F0.wireOp",EDGE,"E3.15"),sQuery(id+"F0.wireOp",EDGE,"E4"),sQuery(id+"F0.wireOp",EDGE,"E5"),sQuery(id+"F0.wireOp",EDGE,"E6"),sQuery(id+"F0.wireOp",EDGE,"E7"),sQuery(id+"F0.wireOp",EDGE,"E8"),sQuery(id+"F0.wireOp",EDGE,"E9"),sQuery(id+"F0.wireOp",EDGE,"E10"),sQuery(id+"F0.wireOp",EDGE,"E11"),sQuery(id+"F0.wireOp",EDGE,"E12"),sQuery(id+"F0.wireOp",EDGE,"E13"),sQuery(id+"F0.wireOp",EDGE,"E14"),sQuery(id+"F0.wireOp",EDGE,"E15"),sQuery(id+"F0.wireOp",EDGE,"E16"),sQuery(id+"F0.wireOp",EDGE,"E17"),sQuery(id+"F0.wireOp",EDGE,"E18"),sQuery(id+"F0.wireOp",EDGE,"E19")])],"isStart":true})]});}
            var Q4;
            {var subQ0=sQuery(id+"F0.wireOp",EDGE,"E0.1");var subQ1=sQuery(id+"F0.wireOp",EDGE,"E0.0");Q4=makeQuery(id+"F2.opFillet","BLEND_EDGE",EDGE,{"blendedFrom":[makeQuery(id+"F1.opExtrude","SWEPT_EDGE",EDGE,{"disambiguationData":[OSD([subQ1,subQ0])]}),makeQuery(id+"F1.opExtrude","CAP_FACE",FACE,{"disambiguationData":[OSD([subQ1,subQ0,sQuery(id+"F0.wireOp",EDGE,"E0.2"),sQuery(id+"F0.wireOp",EDGE,"E0.3"),sQuery(id+"F0.wireOp",EDGE,"E0.4"),sQuery(id+"F0.wireOp",EDGE,"E0.5"),sQuery(id+"F0.wireOp",EDGE,"E0.6"),sQuery(id+"F0.wireOp",EDGE,"E0.7"),sQuery(id+"F0.wireOp",EDGE,"E0.8"),sQuery(id+"F0.wireOp",EDGE,"E0.9"),sQuery(id+"F0.wireOp",EDGE,"E0.10"),sQuery(id+"F0.wireOp",EDGE,"E0.11"),sQuery(id+"F0.wireOp",EDGE,"E0.12"),sQuery(id+"F0.wireOp",EDGE,"E0.13"),sQuery(id+"F0.wireOp",EDGE,"E0.14"),sQuery(id+"F0.wireOp",EDGE,"E0.15"),sQuery(id+"F0.wireOp",EDGE,"E1"),sQuery(id+"F0.wireOp",EDGE,"E2.1"),sQuery(id+"F0.wireOp",EDGE,"E2.3"),sQuery(id+"F0.wireOp",EDGE,"E2.5"),sQuery(id+"F0.wireOp",EDGE,"E2.7"),sQuery(id+"F0.wireOp",EDGE,"E2.9"),sQuery(id+"F0.wireOp",EDGE,"E2.11"),sQuery(id+"F0.wireOp",EDGE,"E2.13"),sQuery(id+"F0.wireOp",EDGE,"E2.15"),sQuery(id+"F0.wireOp",EDGE,"E3.1"),sQuery(id+"F0.wireOp",EDGE,"E3.3"),sQuery(id+"F0.wireOp",EDGE,"E3.5"),sQuery(id+"F0.wireOp",EDGE,"E3.7"),sQuery(id+"F0.wireOp",EDGE,"E3.9"),sQuery(id+"F0.wireOp",EDGE,"E3.11"),sQuery(id+"F0.wireOp",EDGE,"E3.13"),sQuery(id+"F0.wireOp",EDGE,"E3.15"),sQuery(id+"F0.wireOp",EDGE,"E4"),sQuery(id+"F0.wireOp",EDGE,"E5"),sQuery(id+"F0.wireOp",EDGE,"E6"),sQuery(id+"F0.wireOp",EDGE,"E7"),sQuery(id+"F0.wireOp",EDGE,"E8"),sQuery(id+"F0.wireOp",EDGE,"E9"),sQuery(id+"F0.wireOp",EDGE,"E10"),sQuery(id+"F0.wireOp",EDGE,"E11"),sQuery(id+"F0.wireOp",EDGE,"E12"),sQuery(id+"F0.wireOp",EDGE,"E13"),sQuery(id+"F0.wireOp",EDGE,"E14"),sQuery(id+"F0.wireOp",EDGE,"E15"),sQuery(id+"F0.wireOp",EDGE,"E16"),sQuery(id+"F0.wireOp",EDGE,"E17"),sQuery(id+"F0.wireOp",EDGE,"E18"),sQuery(id+"F0.wireOp",EDGE,"E19")])],"isStart":true})],"blendedInto":[makeQuery(id+"F1.opExtrude","CAP_FACE",FACE,{"disambiguationData":[OSD([subQ1,subQ0,sQuery(id+"F0.wireOp",EDGE,"E0.2"),sQuery(id+"F0.wireOp",EDGE,"E0.3"),sQuery(id+"F0.wireOp",EDGE,"E0.4"),sQuery(id+"F0.wireOp",EDGE,"E0.5"),sQuery(id+"F0.wireOp",EDGE,"E0.6"),sQuery(id+"F0.wireOp",EDGE,"E0.7"),sQuery(id+"F0.wireOp",EDGE,"E0.8"),sQuery(id+"F0.wireOp",EDGE,"E0.9"),sQuery(id+"F0.wireOp",EDGE,"E0.10"),sQuery(id+"F0.wireOp",EDGE,"E0.11"),sQuery(id+"F0.wireOp",EDGE,"E0.12"),sQuery(id+"F0.wireOp",EDGE,"E0.13"),sQuery(id+"F0.wireOp",EDGE,"E0.14"),sQuery(id+"F0.wireOp",EDGE,"E0.15"),sQuery(id+"F0.wireOp",EDGE,"E1"),sQuery(id+"F0.wireOp",EDGE,"E2.1"),sQuery(id+"F0.wireOp",EDGE,"E2.3"),sQuery(id+"F0.wireOp",EDGE,"E2.5"),sQuery(id+"F0.wireOp",EDGE,"E2.7"),sQuery(id+"F0.wireOp",EDGE,"E2.9"),sQuery(id+"F0.wireOp",EDGE,"E2.11"),sQuery(id+"F0.wireOp",EDGE,"E2.13"),sQuery(id+"F0.wireOp",EDGE,"E2.15"),sQuery(id+"F0.wireOp",EDGE,"E3.1"),sQuery(id+"F0.wireOp",EDGE,"E3.3"),sQuery(id+"F0.wireOp",EDGE,"E3.5"),sQuery(id+"F0.wireOp",EDGE,"E3.7"),sQuery(id+"F0.wireOp",EDGE,"E3.9"),sQuery(id+"F0.wireOp",EDGE,"E3.11"),sQuery(id+"F0.wireOp",EDGE,"E3.13"),sQuery(id+"F0.wireOp",EDGE,"E3.15"),sQuery(id+"F0.wireOp",EDGE,"E4"),sQuery(id+"F0.wireOp",EDGE,"E5"),sQuery(id+"F0.wireOp",EDGE,"E6"),sQuery(id+"F0.wireOp",EDGE,"E7"),sQuery(id+"F0.wireOp",EDGE,"E8"),sQuery(id+"F0.wireOp",EDGE,"E9"),sQuery(id+"F0.wireOp",EDGE,"E10"),sQuery(id+"F0.wireOp",EDGE,"E11"),sQuery(id+"F0.wireOp",EDGE,"E12"),sQuery(id+"F0.wireOp",EDGE,"E13"),sQuery(id+"F0.wireOp",EDGE,"E14"),sQuery(id+"F0.wireOp",EDGE,"E15"),sQuery(id+"F0.wireOp",EDGE,"E16"),sQuery(id+"F0.wireOp",EDGE,"E17"),sQuery(id+"F0.wireOp",EDGE,"E18"),sQuery(id+"F0.wireOp",EDGE,"E19")])],"isStart":true})]});}
            var Q5;
            {var subQ0=sQuery(id+"F0.wireOp",EDGE,"E0.15");var subQ1=sQuery(id+"F0.wireOp",EDGE,"E0.0");Q5=makeQuery(id+"F2.opFillet","BLEND_EDGE",EDGE,{"blendedFrom":[makeQuery(id+"F1.opExtrude","SWEPT_EDGE",EDGE,{"disambiguationData":[OSD([subQ1,subQ0])]}),makeQuery(id+"F1.opExtrude","CAP_FACE",FACE,{"disambiguationData":[OSD([subQ1,sQuery(id+"F0.wireOp",EDGE,"E0.1"),sQuery(id+"F0.wireOp",EDGE,"E0.2"),sQuery(id+"F0.wireOp",EDGE,"E0.3"),sQuery(id+"F0.wireOp",EDGE,"E0.4"),sQuery(id+"F0.wireOp",EDGE,"E0.5"),sQuery(id+"F0.wireOp",EDGE,"E0.6"),sQuery(id+"F0.wireOp",EDGE,"E0.7"),sQuery(id+"F0.wireOp",EDGE,"E0.8"),sQuery(id+"F0.wireOp",EDGE,"E0.9"),sQuery(id+"F0.wireOp",EDGE,"E0.10"),sQuery(id+"F0.wireOp",EDGE,"E0.11"),sQuery(id+"F0.wireOp",EDGE,"E0.12"),sQuery(id+"F0.wireOp",EDGE,"E0.13"),sQuery(id+"F0.wireOp",EDGE,"E0.14"),subQ0,sQuery(id+"F0.wireOp",EDGE,"E1"),sQuery(id+"F0.wireOp",EDGE,"E2.1"),sQuery(id+"F0.wireOp",EDGE,"E2.3"),sQuery(id+"F0.wireOp",EDGE,"E2.5"),sQuery(id+"F0.wireOp",EDGE,"E2.7"),sQuery(id+"F0.wireOp",EDGE,"E2.9"),sQuery(id+"F0.wireOp",EDGE,"E2.11"),sQuery(id+"F0.wireOp",EDGE,"E2.13"),sQuery(id+"F0.wireOp",EDGE,"E2.15"),sQuery(id+"F0.wireOp",EDGE,"E3.1"),sQuery(id+"F0.wireOp",EDGE,"E3.3"),sQuery(id+"F0.wireOp",EDGE,"E3.5"),sQuery(id+"F0.wireOp",EDGE,"E3.7"),sQuery(id+"F0.wireOp",EDGE,"E3.9"),sQuery(id+"F0.wireOp",EDGE,"E3.11"),sQuery(id+"F0.wireOp",EDGE,"E3.13"),sQuery(id+"F0.wireOp",EDGE,"E3.15"),sQuery(id+"F0.wireOp",EDGE,"E4"),sQuery(id+"F0.wireOp",EDGE,"E5"),sQuery(id+"F0.wireOp",EDGE,"E6"),sQuery(id+"F0.wireOp",EDGE,"E7"),sQuery(id+"F0.wireOp",EDGE,"E8"),sQuery(id+"F0.wireOp",EDGE,"E9"),sQuery(id+"F0.wireOp",EDGE,"E10"),sQuery(id+"F0.wireOp",EDGE,"E11"),sQuery(id+"F0.wireOp",EDGE,"E12"),sQuery(id+"F0.wireOp",EDGE,"E13"),sQuery(id+"F0.wireOp",EDGE,"E14"),sQuery(id+"F0.wireOp",EDGE,"E15"),sQuery(id+"F0.wireOp",EDGE,"E16"),sQuery(id+"F0.wireOp",EDGE,"E17"),sQuery(id+"F0.wireOp",EDGE,"E18"),sQuery(id+"F0.wireOp",EDGE,"E19")])],"isStart":true})],"blendedInto":[makeQuery(id+"F1.opExtrude","CAP_FACE",FACE,{"disambiguationData":[OSD([subQ1,sQuery(id+"F0.wireOp",EDGE,"E0.1"),sQuery(id+"F0.wireOp",EDGE,"E0.2"),sQuery(id+"F0.wireOp",EDGE,"E0.3"),sQuery(id+"F0.wireOp",EDGE,"E0.4"),sQuery(id+"F0.wireOp",EDGE,"E0.5"),sQuery(id+"F0.wireOp",EDGE,"E0.6"),sQuery(id+"F0.wireOp",EDGE,"E0.7"),sQuery(id+"F0.wireOp",EDGE,"E0.8"),sQuery(id+"F0.wireOp",EDGE,"E0.9"),sQuery(id+"F0.wireOp",EDGE,"E0.10"),sQuery(id+"F0.wireOp",EDGE,"E0.11"),sQuery(id+"F0.wireOp",EDGE,"E0.12"),sQuery(id+"F0.wireOp",EDGE,"E0.13"),sQuery(id+"F0.wireOp",EDGE,"E0.14"),subQ0,sQuery(id+"F0.wireOp",EDGE,"E1"),sQuery(id+"F0.wireOp",EDGE,"E2.1"),sQuery(id+"F0.wireOp",EDGE,"E2.3"),sQuery(id+"F0.wireOp",EDGE,"E2.5"),sQuery(id+"F0.wireOp",EDGE,"E2.7"),sQuery(id+"F0.wireOp",EDGE,"E2.9"),sQuery(id+"F0.wireOp",EDGE,"E2.11"),sQuery(id+"F0.wireOp",EDGE,"E2.13"),sQuery(id+"F0.wireOp",EDGE,"E2.15"),sQuery(id+"F0.wireOp",EDGE,"E3.1"),sQuery(id+"F0.wireOp",EDGE,"E3.3"),sQuery(id+"F0.wireOp",EDGE,"E3.5"),sQuery(id+"F0.wireOp",EDGE,"E3.7"),sQuery(id+"F0.wireOp",EDGE,"E3.9"),sQuery(id+"F0.wireOp",EDGE,"E3.11"),sQuery(id+"F0.wireOp",EDGE,"E3.13"),sQuery(id+"F0.wireOp",EDGE,"E3.15"),sQuery(id+"F0.wireOp",EDGE,"E4"),sQuery(id+"F0.wireOp",EDGE,"E5"),sQuery(id+"F0.wireOp",EDGE,"E6"),sQuery(id+"F0.wireOp",EDGE,"E7"),sQuery(id+"F0.wireOp",EDGE,"E8"),sQuery(id+"F0.wireOp",EDGE,"E9"),sQuery(id+"F0.wireOp",EDGE,"E10"),sQuery(id+"F0.wireOp",EDGE,"E11"),sQuery(id+"F0.wireOp",EDGE,"E12"),sQuery(id+"F0.wireOp",EDGE,"E13"),sQuery(id+"F0.wireOp",EDGE,"E14"),sQuery(id+"F0.wireOp",EDGE,"E15"),sQuery(id+"F0.wireOp",EDGE,"E16"),sQuery(id+"F0.wireOp",EDGE,"E17"),sQuery(id+"F0.wireOp",EDGE,"E18"),sQuery(id+"F0.wireOp",EDGE,"E19")])],"isStart":true})]});}
            var Q6;
            {var subQ0=sQuery(id+"F0.wireOp",EDGE,"E0.15");var subQ1=sQuery(id+"F0.wireOp",EDGE,"E0.14");Q6=makeQuery(id+"F2.opFillet","BLEND_EDGE",EDGE,{"blendedFrom":[makeQuery(id+"F1.opExtrude","SWEPT_EDGE",EDGE,{"disambiguationData":[OSD([subQ1,subQ0])]}),makeQuery(id+"F1.opExtrude","CAP_FACE",FACE,{"disambiguationData":[OSD([sQuery(id+"F0.wireOp",EDGE,"E0.0"),sQuery(id+"F0.wireOp",EDGE,"E0.1"),sQuery(id+"F0.wireOp",EDGE,"E0.2"),sQuery(id+"F0.wireOp",EDGE,"E0.3"),sQuery(id+"F0.wireOp",EDGE,"E0.4"),sQuery(id+"F0.wireOp",EDGE,"E0.5"),sQuery(id+"F0.wireOp",EDGE,"E0.6"),sQuery(id+"F0.wireOp",EDGE,"E0.7"),sQuery(id+"F0.wireOp",EDGE,"E0.8"),sQuery(id+"F0.wireOp",EDGE,"E0.9"),sQuery(id+"F0.wireOp",EDGE,"E0.10"),sQuery(id+"F0.wireOp",EDGE,"E0.11"),sQuery(id+"F0.wireOp",EDGE,"E0.12"),sQuery(id+"F0.wireOp",EDGE,"E0.13"),subQ1,subQ0,sQuery(id+"F0.wireOp",EDGE,"E1"),sQuery(id+"F0.wireOp",EDGE,"E2.1"),sQuery(id+"F0.wireOp",EDGE,"E2.3"),sQuery(id+"F0.wireOp",EDGE,"E2.5"),sQuery(id+"F0.wireOp",EDGE,"E2.7"),sQuery(id+"F0.wireOp",EDGE,"E2.9"),sQuery(id+"F0.wireOp",EDGE,"E2.11"),sQuery(id+"F0.wireOp",EDGE,"E2.13"),sQuery(id+"F0.wireOp",EDGE,"E2.15"),sQuery(id+"F0.wireOp",EDGE,"E3.1"),sQuery(id+"F0.wireOp",EDGE,"E3.3"),sQuery(id+"F0.wireOp",EDGE,"E3.5"),sQuery(id+"F0.wireOp",EDGE,"E3.7"),sQuery(id+"F0.wireOp",EDGE,"E3.9"),sQuery(id+"F0.wireOp",EDGE,"E3.11"),sQuery(id+"F0.wireOp",EDGE,"E3.13"),sQuery(id+"F0.wireOp",EDGE,"E3.15"),sQuery(id+"F0.wireOp",EDGE,"E4"),sQuery(id+"F0.wireOp",EDGE,"E5"),sQuery(id+"F0.wireOp",EDGE,"E6"),sQuery(id+"F0.wireOp",EDGE,"E7"),sQuery(id+"F0.wireOp",EDGE,"E8"),sQuery(id+"F0.wireOp",EDGE,"E9"),sQuery(id+"F0.wireOp",EDGE,"E10"),sQuery(id+"F0.wireOp",EDGE,"E11"),sQuery(id+"F0.wireOp",EDGE,"E12"),sQuery(id+"F0.wireOp",EDGE,"E13"),sQuery(id+"F0.wireOp",EDGE,"E14"),sQuery(id+"F0.wireOp",EDGE,"E15"),sQuery(id+"F0.wireOp",EDGE,"E16"),sQuery(id+"F0.wireOp",EDGE,"E17"),sQuery(id+"F0.wireOp",EDGE,"E18"),sQuery(id+"F0.wireOp",EDGE,"E19")])],"isStart":true})],"blendedInto":[makeQuery(id+"F1.opExtrude","CAP_FACE",FACE,{"disambiguationData":[OSD([sQuery(id+"F0.wireOp",EDGE,"E0.0"),sQuery(id+"F0.wireOp",EDGE,"E0.1"),sQuery(id+"F0.wireOp",EDGE,"E0.2"),sQuery(id+"F0.wireOp",EDGE,"E0.3"),sQuery(id+"F0.wireOp",EDGE,"E0.4"),sQuery(id+"F0.wireOp",EDGE,"E0.5"),sQuery(id+"F0.wireOp",EDGE,"E0.6"),sQuery(id+"F0.wireOp",EDGE,"E0.7"),sQuery(id+"F0.wireOp",EDGE,"E0.8"),sQuery(id+"F0.wireOp",EDGE,"E0.9"),sQuery(id+"F0.wireOp",EDGE,"E0.10"),sQuery(id+"F0.wireOp",EDGE,"E0.11"),sQuery(id+"F0.wireOp",EDGE,"E0.12"),sQuery(id+"F0.wireOp",EDGE,"E0.13"),subQ1,subQ0,sQuery(id+"F0.wireOp",EDGE,"E1"),sQuery(id+"F0.wireOp",EDGE,"E2.1"),sQuery(id+"F0.wireOp",EDGE,"E2.3"),sQuery(id+"F0.wireOp",EDGE,"E2.5"),sQuery(id+"F0.wireOp",EDGE,"E2.7"),sQuery(id+"F0.wireOp",EDGE,"E2.9"),sQuery(id+"F0.wireOp",EDGE,"E2.11"),sQuery(id+"F0.wireOp",EDGE,"E2.13"),sQuery(id+"F0.wireOp",EDGE,"E2.15"),sQuery(id+"F0.wireOp",EDGE,"E3.1"),sQuery(id+"F0.wireOp",EDGE,"E3.3"),sQuery(id+"F0.wireOp",EDGE,"E3.5"),sQuery(id+"F0.wireOp",EDGE,"E3.7"),sQuery(id+"F0.wireOp",EDGE,"E3.9"),sQuery(id+"F0.wireOp",EDGE,"E3.11"),sQuery(id+"F0.wireOp",EDGE,"E3.13"),sQuery(id+"F0.wireOp",EDGE,"E3.15"),sQuery(id+"F0.wireOp",EDGE,"E4"),sQuery(id+"F0.wireOp",EDGE,"E5"),sQuery(id+"F0.wireOp",EDGE,"E6"),sQuery(id+"F0.wireOp",EDGE,"E7"),sQuery(id+"F0.wireOp",EDGE,"E8"),sQuery(id+"F0.wireOp",EDGE,"E9"),sQuery(id+"F0.wireOp",EDGE,"E10"),sQuery(id+"F0.wireOp",EDGE,"E11"),sQuery(id+"F0.wireOp",EDGE,"E12"),sQuery(id+"F0.wireOp",EDGE,"E13"),sQuery(id+"F0.wireOp",EDGE,"E14"),sQuery(id+"F0.wireOp",EDGE,"E15"),sQuery(id+"F0.wireOp",EDGE,"E16"),sQuery(id+"F0.wireOp",EDGE,"E17"),sQuery(id+"F0.wireOp",EDGE,"E18"),sQuery(id+"F0.wireOp",EDGE,"E19")])],"isStart":true})]});}
            var Q7;
            {var subQ0=sQuery(id+"F0.wireOp",EDGE,"E0.14");var subQ1=sQuery(id+"F0.wireOp",EDGE,"E0.13");Q7=makeQuery(id+"F2.opFillet","BLEND_EDGE",EDGE,{"blendedFrom":[makeQuery(id+"F1.opExtrude","SWEPT_EDGE",EDGE,{"disambiguationData":[OSD([subQ1,subQ0])]}),makeQuery(id+"F1.opExtrude","CAP_FACE",FACE,{"disambiguationData":[OSD([sQuery(id+"F0.wireOp",EDGE,"E0.0"),sQuery(id+"F0.wireOp",EDGE,"E0.1"),sQuery(id+"F0.wireOp",EDGE,"E0.2"),sQuery(id+"F0.wireOp",EDGE,"E0.3"),sQuery(id+"F0.wireOp",EDGE,"E0.4"),sQuery(id+"F0.wireOp",EDGE,"E0.5"),sQuery(id+"F0.wireOp",EDGE,"E0.6"),sQuery(id+"F0.wireOp",EDGE,"E0.7"),sQuery(id+"F0.wireOp",EDGE,"E0.8"),sQuery(id+"F0.wireOp",EDGE,"E0.9"),sQuery(id+"F0.wireOp",EDGE,"E0.10"),sQuery(id+"F0.wireOp",EDGE,"E0.11"),sQuery(id+"F0.wireOp",EDGE,"E0.12"),subQ1,subQ0,sQuery(id+"F0.wireOp",EDGE,"E0.15"),sQuery(id+"F0.wireOp",EDGE,"E1"),sQuery(id+"F0.wireOp",EDGE,"E2.1"),sQuery(id+"F0.wireOp",EDGE,"E2.3"),sQuery(id+"F0.wireOp",EDGE,"E2.5"),sQuery(id+"F0.wireOp",EDGE,"E2.7"),sQuery(id+"F0.wireOp",EDGE,"E2.9"),sQuery(id+"F0.wireOp",EDGE,"E2.11"),sQuery(id+"F0.wireOp",EDGE,"E2.13"),sQuery(id+"F0.wireOp",EDGE,"E2.15"),sQuery(id+"F0.wireOp",EDGE,"E3.1"),sQuery(id+"F0.wireOp",EDGE,"E3.3"),sQuery(id+"F0.wireOp",EDGE,"E3.5"),sQuery(id+"F0.wireOp",EDGE,"E3.7"),sQuery(id+"F0.wireOp",EDGE,"E3.9"),sQuery(id+"F0.wireOp",EDGE,"E3.11"),sQuery(id+"F0.wireOp",EDGE,"E3.13"),sQuery(id+"F0.wireOp",EDGE,"E3.15"),sQuery(id+"F0.wireOp",EDGE,"E4"),sQuery(id+"F0.wireOp",EDGE,"E5"),sQuery(id+"F0.wireOp",EDGE,"E6"),sQuery(id+"F0.wireOp",EDGE,"E7"),sQuery(id+"F0.wireOp",EDGE,"E8"),sQuery(id+"F0.wireOp",EDGE,"E9"),sQuery(id+"F0.wireOp",EDGE,"E10"),sQuery(id+"F0.wireOp",EDGE,"E11"),sQuery(id+"F0.wireOp",EDGE,"E12"),sQuery(id+"F0.wireOp",EDGE,"E13"),sQuery(id+"F0.wireOp",EDGE,"E14"),sQuery(id+"F0.wireOp",EDGE,"E15"),sQuery(id+"F0.wireOp",EDGE,"E16"),sQuery(id+"F0.wireOp",EDGE,"E17"),sQuery(id+"F0.wireOp",EDGE,"E18"),sQuery(id+"F0.wireOp",EDGE,"E19")])],"isStart":true})],"blendedInto":[makeQuery(id+"F1.opExtrude","CAP_FACE",FACE,{"disambiguationData":[OSD([sQuery(id+"F0.wireOp",EDGE,"E0.0"),sQuery(id+"F0.wireOp",EDGE,"E0.1"),sQuery(id+"F0.wireOp",EDGE,"E0.2"),sQuery(id+"F0.wireOp",EDGE,"E0.3"),sQuery(id+"F0.wireOp",EDGE,"E0.4"),sQuery(id+"F0.wireOp",EDGE,"E0.5"),sQuery(id+"F0.wireOp",EDGE,"E0.6"),sQuery(id+"F0.wireOp",EDGE,"E0.7"),sQuery(id+"F0.wireOp",EDGE,"E0.8"),sQuery(id+"F0.wireOp",EDGE,"E0.9"),sQuery(id+"F0.wireOp",EDGE,"E0.10"),sQuery(id+"F0.wireOp",EDGE,"E0.11"),sQuery(id+"F0.wireOp",EDGE,"E0.12"),subQ1,subQ0,sQuery(id+"F0.wireOp",EDGE,"E0.15"),sQuery(id+"F0.wireOp",EDGE,"E1"),sQuery(id+"F0.wireOp",EDGE,"E2.1"),sQuery(id+"F0.wireOp",EDGE,"E2.3"),sQuery(id+"F0.wireOp",EDGE,"E2.5"),sQuery(id+"F0.wireOp",EDGE,"E2.7"),sQuery(id+"F0.wireOp",EDGE,"E2.9"),sQuery(id+"F0.wireOp",EDGE,"E2.11"),sQuery(id+"F0.wireOp",EDGE,"E2.13"),sQuery(id+"F0.wireOp",EDGE,"E2.15"),sQuery(id+"F0.wireOp",EDGE,"E3.1"),sQuery(id+"F0.wireOp",EDGE,"E3.3"),sQuery(id+"F0.wireOp",EDGE,"E3.5"),sQuery(id+"F0.wireOp",EDGE,"E3.7"),sQuery(id+"F0.wireOp",EDGE,"E3.9"),sQuery(id+"F0.wireOp",EDGE,"E3.11"),sQuery(id+"F0.wireOp",EDGE,"E3.13"),sQuery(id+"F0.wireOp",EDGE,"E3.15"),sQuery(id+"F0.wireOp",EDGE,"E4"),sQuery(id+"F0.wireOp",EDGE,"E5"),sQuery(id+"F0.wireOp",EDGE,"E6"),sQuery(id+"F0.wireOp",EDGE,"E7"),sQuery(id+"F0.wireOp",EDGE,"E8"),sQuery(id+"F0.wireOp",EDGE,"E9"),sQuery(id+"F0.wireOp",EDGE,"E10"),sQuery(id+"F0.wireOp",EDGE,"E11"),sQuery(id+"F0.wireOp",EDGE,"E12"),sQuery(id+"F0.wireOp",EDGE,"E13"),sQuery(id+"F0.wireOp",EDGE,"E14"),sQuery(id+"F0.wireOp",EDGE,"E15"),sQuery(id+"F0.wireOp",EDGE,"E16"),sQuery(id+"F0.wireOp",EDGE,"E17"),sQuery(id+"F0.wireOp",EDGE,"E18"),sQuery(id+"F0.wireOp",EDGE,"E19")])],"isStart":true})]});}
            var Q8;
            {var subQ0=sQuery(id+"F0.wireOp",EDGE,"E0.13");var subQ1=sQuery(id+"F0.wireOp",EDGE,"E0.12");Q8=makeQuery(id+"F2.opFillet","BLEND_EDGE",EDGE,{"blendedFrom":[makeQuery(id+"F1.opExtrude","SWEPT_EDGE",EDGE,{"disambiguationData":[OSD([subQ1,subQ0])]}),makeQuery(id+"F1.opExtrude","CAP_FACE",FACE,{"disambiguationData":[OSD([sQuery(id+"F0.wireOp",EDGE,"E0.0"),sQuery(id+"F0.wireOp",EDGE,"E0.1"),sQuery(id+"F0.wireOp",EDGE,"E0.2"),sQuery(id+"F0.wireOp",EDGE,"E0.3"),sQuery(id+"F0.wireOp",EDGE,"E0.4"),sQuery(id+"F0.wireOp",EDGE,"E0.5"),sQuery(id+"F0.wireOp",EDGE,"E0.6"),sQuery(id+"F0.wireOp",EDGE,"E0.7"),sQuery(id+"F0.wireOp",EDGE,"E0.8"),sQuery(id+"F0.wireOp",EDGE,"E0.9"),sQuery(id+"F0.wireOp",EDGE,"E0.10"),sQuery(id+"F0.wireOp",EDGE,"E0.11"),subQ1,subQ0,sQuery(id+"F0.wireOp",EDGE,"E0.14"),sQuery(id+"F0.wireOp",EDGE,"E0.15"),sQuery(id+"F0.wireOp",EDGE,"E1"),sQuery(id+"F0.wireOp",EDGE,"E2.1"),sQuery(id+"F0.wireOp",EDGE,"E2.3"),sQuery(id+"F0.wireOp",EDGE,"E2.5"),sQuery(id+"F0.wireOp",EDGE,"E2.7"),sQuery(id+"F0.wireOp",EDGE,"E2.9"),sQuery(id+"F0.wireOp",EDGE,"E2.11"),sQuery(id+"F0.wireOp",EDGE,"E2.13"),sQuery(id+"F0.wireOp",EDGE,"E2.15"),sQuery(id+"F0.wireOp",EDGE,"E3.1"),sQuery(id+"F0.wireOp",EDGE,"E3.3"),sQuery(id+"F0.wireOp",EDGE,"E3.5"),sQuery(id+"F0.wireOp",EDGE,"E3.7"),sQuery(id+"F0.wireOp",EDGE,"E3.9"),sQuery(id+"F0.wireOp",EDGE,"E3.11"),sQuery(id+"F0.wireOp",EDGE,"E3.13"),sQuery(id+"F0.wireOp",EDGE,"E3.15"),sQuery(id+"F0.wireOp",EDGE,"E4"),sQuery(id+"F0.wireOp",EDGE,"E5"),sQuery(id+"F0.wireOp",EDGE,"E6"),sQuery(id+"F0.wireOp",EDGE,"E7"),sQuery(id+"F0.wireOp",EDGE,"E8"),sQuery(id+"F0.wireOp",EDGE,"E9"),sQuery(id+"F0.wireOp",EDGE,"E10"),sQuery(id+"F0.wireOp",EDGE,"E11"),sQuery(id+"F0.wireOp",EDGE,"E12"),sQuery(id+"F0.wireOp",EDGE,"E13"),sQuery(id+"F0.wireOp",EDGE,"E14"),sQuery(id+"F0.wireOp",EDGE,"E15"),sQuery(id+"F0.wireOp",EDGE,"E16"),sQuery(id+"F0.wireOp",EDGE,"E17"),sQuery(id+"F0.wireOp",EDGE,"E18"),sQuery(id+"F0.wireOp",EDGE,"E19")])],"isStart":true})],"blendedInto":[makeQuery(id+"F1.opExtrude","CAP_FACE",FACE,{"disambiguationData":[OSD([sQuery(id+"F0.wireOp",EDGE,"E0.0"),sQuery(id+"F0.wireOp",EDGE,"E0.1"),sQuery(id+"F0.wireOp",EDGE,"E0.2"),sQuery(id+"F0.wireOp",EDGE,"E0.3"),sQuery(id+"F0.wireOp",EDGE,"E0.4"),sQuery(id+"F0.wireOp",EDGE,"E0.5"),sQuery(id+"F0.wireOp",EDGE,"E0.6"),sQuery(id+"F0.wireOp",EDGE,"E0.7"),sQuery(id+"F0.wireOp",EDGE,"E0.8"),sQuery(id+"F0.wireOp",EDGE,"E0.9"),sQuery(id+"F0.wireOp",EDGE,"E0.10"),sQuery(id+"F0.wireOp",EDGE,"E0.11"),subQ1,subQ0,sQuery(id+"F0.wireOp",EDGE,"E0.14"),sQuery(id+"F0.wireOp",EDGE,"E0.15"),sQuery(id+"F0.wireOp",EDGE,"E1"),sQuery(id+"F0.wireOp",EDGE,"E2.1"),sQuery(id+"F0.wireOp",EDGE,"E2.3"),sQuery(id+"F0.wireOp",EDGE,"E2.5"),sQuery(id+"F0.wireOp",EDGE,"E2.7"),sQuery(id+"F0.wireOp",EDGE,"E2.9"),sQuery(id+"F0.wireOp",EDGE,"E2.11"),sQuery(id+"F0.wireOp",EDGE,"E2.13"),sQuery(id+"F0.wireOp",EDGE,"E2.15"),sQuery(id+"F0.wireOp",EDGE,"E3.1"),sQuery(id+"F0.wireOp",EDGE,"E3.3"),sQuery(id+"F0.wireOp",EDGE,"E3.5"),sQuery(id+"F0.wireOp",EDGE,"E3.7"),sQuery(id+"F0.wireOp",EDGE,"E3.9"),sQuery(id+"F0.wireOp",EDGE,"E3.11"),sQuery(id+"F0.wireOp",EDGE,"E3.13"),sQuery(id+"F0.wireOp",EDGE,"E3.15"),sQuery(id+"F0.wireOp",EDGE,"E4"),sQuery(id+"F0.wireOp",EDGE,"E5"),sQuery(id+"F0.wireOp",EDGE,"E6"),sQuery(id+"F0.wireOp",EDGE,"E7"),sQuery(id+"F0.wireOp",EDGE,"E8"),sQuery(id+"F0.wireOp",EDGE,"E9"),sQuery(id+"F0.wireOp",EDGE,"E10"),sQuery(id+"F0.wireOp",EDGE,"E11"),sQuery(id+"F0.wireOp",EDGE,"E12"),sQuery(id+"F0.wireOp",EDGE,"E13"),sQuery(id+"F0.wireOp",EDGE,"E14"),sQuery(id+"F0.wireOp",EDGE,"E15"),sQuery(id+"F0.wireOp",EDGE,"E16"),sQuery(id+"F0.wireOp",EDGE,"E17"),sQuery(id+"F0.wireOp",EDGE,"E18"),sQuery(id+"F0.wireOp",EDGE,"E19")])],"isStart":true})]});}
            var Q9;
            {var subQ0=sQuery(id+"F0.wireOp",EDGE,"E0.12");var subQ1=sQuery(id+"F0.wireOp",EDGE,"E0.11");Q9=makeQuery(id+"F2.opFillet","BLEND_EDGE",EDGE,{"blendedFrom":[makeQuery(id+"F1.opExtrude","SWEPT_EDGE",EDGE,{"disambiguationData":[OSD([subQ1,subQ0])]}),makeQuery(id+"F1.opExtrude","CAP_FACE",FACE,{"disambiguationData":[OSD([sQuery(id+"F0.wireOp",EDGE,"E0.0"),sQuery(id+"F0.wireOp",EDGE,"E0.1"),sQuery(id+"F0.wireOp",EDGE,"E0.2"),sQuery(id+"F0.wireOp",EDGE,"E0.3"),sQuery(id+"F0.wireOp",EDGE,"E0.4"),sQuery(id+"F0.wireOp",EDGE,"E0.5"),sQuery(id+"F0.wireOp",EDGE,"E0.6"),sQuery(id+"F0.wireOp",EDGE,"E0.7"),sQuery(id+"F0.wireOp",EDGE,"E0.8"),sQuery(id+"F0.wireOp",EDGE,"E0.9"),sQuery(id+"F0.wireOp",EDGE,"E0.10"),subQ1,subQ0,sQuery(id+"F0.wireOp",EDGE,"E0.13"),sQuery(id+"F0.wireOp",EDGE,"E0.14"),sQuery(id+"F0.wireOp",EDGE,"E0.15"),sQuery(id+"F0.wireOp",EDGE,"E1"),sQuery(id+"F0.wireOp",EDGE,"E2.1"),sQuery(id+"F0.wireOp",EDGE,"E2.3"),sQuery(id+"F0.wireOp",EDGE,"E2.5"),sQuery(id+"F0.wireOp",EDGE,"E2.7"),sQuery(id+"F0.wireOp",EDGE,"E2.9"),sQuery(id+"F0.wireOp",EDGE,"E2.11"),sQuery(id+"F0.wireOp",EDGE,"E2.13"),sQuery(id+"F0.wireOp",EDGE,"E2.15"),sQuery(id+"F0.wireOp",EDGE,"E3.1"),sQuery(id+"F0.wireOp",EDGE,"E3.3"),sQuery(id+"F0.wireOp",EDGE,"E3.5"),sQuery(id+"F0.wireOp",EDGE,"E3.7"),sQuery(id+"F0.wireOp",EDGE,"E3.9"),sQuery(id+"F0.wireOp",EDGE,"E3.11"),sQuery(id+"F0.wireOp",EDGE,"E3.13"),sQuery(id+"F0.wireOp",EDGE,"E3.15"),sQuery(id+"F0.wireOp",EDGE,"E4"),sQuery(id+"F0.wireOp",EDGE,"E5"),sQuery(id+"F0.wireOp",EDGE,"E6"),sQuery(id+"F0.wireOp",EDGE,"E7"),sQuery(id+"F0.wireOp",EDGE,"E8"),sQuery(id+"F0.wireOp",EDGE,"E9"),sQuery(id+"F0.wireOp",EDGE,"E10"),sQuery(id+"F0.wireOp",EDGE,"E11"),sQuery(id+"F0.wireOp",EDGE,"E12"),sQuery(id+"F0.wireOp",EDGE,"E13"),sQuery(id+"F0.wireOp",EDGE,"E14"),sQuery(id+"F0.wireOp",EDGE,"E15"),sQuery(id+"F0.wireOp",EDGE,"E16"),sQuery(id+"F0.wireOp",EDGE,"E17"),sQuery(id+"F0.wireOp",EDGE,"E18"),sQuery(id+"F0.wireOp",EDGE,"E19")])],"isStart":true})],"blendedInto":[makeQuery(id+"F1.opExtrude","CAP_FACE",FACE,{"disambiguationData":[OSD([sQuery(id+"F0.wireOp",EDGE,"E0.0"),sQuery(id+"F0.wireOp",EDGE,"E0.1"),sQuery(id+"F0.wireOp",EDGE,"E0.2"),sQuery(id+"F0.wireOp",EDGE,"E0.3"),sQuery(id+"F0.wireOp",EDGE,"E0.4"),sQuery(id+"F0.wireOp",EDGE,"E0.5"),sQuery(id+"F0.wireOp",EDGE,"E0.6"),sQuery(id+"F0.wireOp",EDGE,"E0.7"),sQuery(id+"F0.wireOp",EDGE,"E0.8"),sQuery(id+"F0.wireOp",EDGE,"E0.9"),sQuery(id+"F0.wireOp",EDGE,"E0.10"),subQ1,subQ0,sQuery(id+"F0.wireOp",EDGE,"E0.13"),sQuery(id+"F0.wireOp",EDGE,"E0.14"),sQuery(id+"F0.wireOp",EDGE,"E0.15"),sQuery(id+"F0.wireOp",EDGE,"E1"),sQuery(id+"F0.wireOp",EDGE,"E2.1"),sQuery(id+"F0.wireOp",EDGE,"E2.3"),sQuery(id+"F0.wireOp",EDGE,"E2.5"),sQuery(id+"F0.wireOp",EDGE,"E2.7"),sQuery(id+"F0.wireOp",EDGE,"E2.9"),sQuery(id+"F0.wireOp",EDGE,"E2.11"),sQuery(id+"F0.wireOp",EDGE,"E2.13"),sQuery(id+"F0.wireOp",EDGE,"E2.15"),sQuery(id+"F0.wireOp",EDGE,"E3.1"),sQuery(id+"F0.wireOp",EDGE,"E3.3"),sQuery(id+"F0.wireOp",EDGE,"E3.5"),sQuery(id+"F0.wireOp",EDGE,"E3.7"),sQuery(id+"F0.wireOp",EDGE,"E3.9"),sQuery(id+"F0.wireOp",EDGE,"E3.11"),sQuery(id+"F0.wireOp",EDGE,"E3.13"),sQuery(id+"F0.wireOp",EDGE,"E3.15"),sQuery(id+"F0.wireOp",EDGE,"E4"),sQuery(id+"F0.wireOp",EDGE,"E5"),sQuery(id+"F0.wireOp",EDGE,"E6"),sQuery(id+"F0.wireOp",EDGE,"E7"),sQuery(id+"F0.wireOp",EDGE,"E8"),sQuery(id+"F0.wireOp",EDGE,"E9"),sQuery(id+"F0.wireOp",EDGE,"E10"),sQuery(id+"F0.wireOp",EDGE,"E11"),sQuery(id+"F0.wireOp",EDGE,"E12"),sQuery(id+"F0.wireOp",EDGE,"E13"),sQuery(id+"F0.wireOp",EDGE,"E14"),sQuery(id+"F0.wireOp",EDGE,"E15"),sQuery(id+"F0.wireOp",EDGE,"E16"),sQuery(id+"F0.wireOp",EDGE,"E17"),sQuery(id+"F0.wireOp",EDGE,"E18"),sQuery(id+"F0.wireOp",EDGE,"E19")])],"isStart":true})]});}
            var Q10;
            {var subQ0=sQuery(id+"F0.wireOp",EDGE,"E0.11");var subQ1=sQuery(id+"F0.wireOp",EDGE,"E0.10");Q10=makeQuery(id+"F2.opFillet","BLEND_EDGE",EDGE,{"blendedFrom":[makeQuery(id+"F1.opExtrude","SWEPT_EDGE",EDGE,{"disambiguationData":[OSD([subQ1,subQ0])]}),makeQuery(id+"F1.opExtrude","CAP_FACE",FACE,{"disambiguationData":[OSD([sQuery(id+"F0.wireOp",EDGE,"E0.0"),sQuery(id+"F0.wireOp",EDGE,"E0.1"),sQuery(id+"F0.wireOp",EDGE,"E0.2"),sQuery(id+"F0.wireOp",EDGE,"E0.3"),sQuery(id+"F0.wireOp",EDGE,"E0.4"),sQuery(id+"F0.wireOp",EDGE,"E0.5"),sQuery(id+"F0.wireOp",EDGE,"E0.6"),sQuery(id+"F0.wireOp",EDGE,"E0.7"),sQuery(id+"F0.wireOp",EDGE,"E0.8"),sQuery(id+"F0.wireOp",EDGE,"E0.9"),subQ1,subQ0,sQuery(id+"F0.wireOp",EDGE,"E0.12"),sQuery(id+"F0.wireOp",EDGE,"E0.13"),sQuery(id+"F0.wireOp",EDGE,"E0.14"),sQuery(id+"F0.wireOp",EDGE,"E0.15"),sQuery(id+"F0.wireOp",EDGE,"E1"),sQuery(id+"F0.wireOp",EDGE,"E2.1"),sQuery(id+"F0.wireOp",EDGE,"E2.3"),sQuery(id+"F0.wireOp",EDGE,"E2.5"),sQuery(id+"F0.wireOp",EDGE,"E2.7"),sQuery(id+"F0.wireOp",EDGE,"E2.9"),sQuery(id+"F0.wireOp",EDGE,"E2.11"),sQuery(id+"F0.wireOp",EDGE,"E2.13"),sQuery(id+"F0.wireOp",EDGE,"E2.15"),sQuery(id+"F0.wireOp",EDGE,"E3.1"),sQuery(id+"F0.wireOp",EDGE,"E3.3"),sQuery(id+"F0.wireOp",EDGE,"E3.5"),sQuery(id+"F0.wireOp",EDGE,"E3.7"),sQuery(id+"F0.wireOp",EDGE,"E3.9"),sQuery(id+"F0.wireOp",EDGE,"E3.11"),sQuery(id+"F0.wireOp",EDGE,"E3.13"),sQuery(id+"F0.wireOp",EDGE,"E3.15"),sQuery(id+"F0.wireOp",EDGE,"E4"),sQuery(id+"F0.wireOp",EDGE,"E5"),sQuery(id+"F0.wireOp",EDGE,"E6"),sQuery(id+"F0.wireOp",EDGE,"E7"),sQuery(id+"F0.wireOp",EDGE,"E8"),sQuery(id+"F0.wireOp",EDGE,"E9"),sQuery(id+"F0.wireOp",EDGE,"E10"),sQuery(id+"F0.wireOp",EDGE,"E11"),sQuery(id+"F0.wireOp",EDGE,"E12"),sQuery(id+"F0.wireOp",EDGE,"E13"),sQuery(id+"F0.wireOp",EDGE,"E14"),sQuery(id+"F0.wireOp",EDGE,"E15"),sQuery(id+"F0.wireOp",EDGE,"E16"),sQuery(id+"F0.wireOp",EDGE,"E17"),sQuery(id+"F0.wireOp",EDGE,"E18"),sQuery(id+"F0.wireOp",EDGE,"E19")])],"isStart":true})],"blendedInto":[makeQuery(id+"F1.opExtrude","CAP_FACE",FACE,{"disambiguationData":[OSD([sQuery(id+"F0.wireOp",EDGE,"E0.0"),sQuery(id+"F0.wireOp",EDGE,"E0.1"),sQuery(id+"F0.wireOp",EDGE,"E0.2"),sQuery(id+"F0.wireOp",EDGE,"E0.3"),sQuery(id+"F0.wireOp",EDGE,"E0.4"),sQuery(id+"F0.wireOp",EDGE,"E0.5"),sQuery(id+"F0.wireOp",EDGE,"E0.6"),sQuery(id+"F0.wireOp",EDGE,"E0.7"),sQuery(id+"F0.wireOp",EDGE,"E0.8"),sQuery(id+"F0.wireOp",EDGE,"E0.9"),subQ1,subQ0,sQuery(id+"F0.wireOp",EDGE,"E0.12"),sQuery(id+"F0.wireOp",EDGE,"E0.13"),sQuery(id+"F0.wireOp",EDGE,"E0.14"),sQuery(id+"F0.wireOp",EDGE,"E0.15"),sQuery(id+"F0.wireOp",EDGE,"E1"),sQuery(id+"F0.wireOp",EDGE,"E2.1"),sQuery(id+"F0.wireOp",EDGE,"E2.3"),sQuery(id+"F0.wireOp",EDGE,"E2.5"),sQuery(id+"F0.wireOp",EDGE,"E2.7"),sQuery(id+"F0.wireOp",EDGE,"E2.9"),sQuery(id+"F0.wireOp",EDGE,"E2.11"),sQuery(id+"F0.wireOp",EDGE,"E2.13"),sQuery(id+"F0.wireOp",EDGE,"E2.15"),sQuery(id+"F0.wireOp",EDGE,"E3.1"),sQuery(id+"F0.wireOp",EDGE,"E3.3"),sQuery(id+"F0.wireOp",EDGE,"E3.5"),sQuery(id+"F0.wireOp",EDGE,"E3.7"),sQuery(id+"F0.wireOp",EDGE,"E3.9"),sQuery(id+"F0.wireOp",EDGE,"E3.11"),sQuery(id+"F0.wireOp",EDGE,"E3.13"),sQuery(id+"F0.wireOp",EDGE,"E3.15"),sQuery(id+"F0.wireOp",EDGE,"E4"),sQuery(id+"F0.wireOp",EDGE,"E5"),sQuery(id+"F0.wireOp",EDGE,"E6"),sQuery(id+"F0.wireOp",EDGE,"E7"),sQuery(id+"F0.wireOp",EDGE,"E8"),sQuery(id+"F0.wireOp",EDGE,"E9"),sQuery(id+"F0.wireOp",EDGE,"E10"),sQuery(id+"F0.wireOp",EDGE,"E11"),sQuery(id+"F0.wireOp",EDGE,"E12"),sQuery(id+"F0.wireOp",EDGE,"E13"),sQuery(id+"F0.wireOp",EDGE,"E14"),sQuery(id+"F0.wireOp",EDGE,"E15"),sQuery(id+"F0.wireOp",EDGE,"E16"),sQuery(id+"F0.wireOp",EDGE,"E17"),sQuery(id+"F0.wireOp",EDGE,"E18"),sQuery(id+"F0.wireOp",EDGE,"E19")])],"isStart":true})]});}
            var Q11;
            {var subQ0=sQuery(id+"F0.wireOp",EDGE,"E0.10");var subQ1=sQuery(id+"F0.wireOp",EDGE,"E0.9");Q11=makeQuery(id+"F2.opFillet","BLEND_EDGE",EDGE,{"blendedFrom":[makeQuery(id+"F1.opExtrude","SWEPT_EDGE",EDGE,{"disambiguationData":[OSD([subQ1,subQ0])]}),makeQuery(id+"F1.opExtrude","CAP_FACE",FACE,{"disambiguationData":[OSD([sQuery(id+"F0.wireOp",EDGE,"E0.0"),sQuery(id+"F0.wireOp",EDGE,"E0.1"),sQuery(id+"F0.wireOp",EDGE,"E0.2"),sQuery(id+"F0.wireOp",EDGE,"E0.3"),sQuery(id+"F0.wireOp",EDGE,"E0.4"),sQuery(id+"F0.wireOp",EDGE,"E0.5"),sQuery(id+"F0.wireOp",EDGE,"E0.6"),sQuery(id+"F0.wireOp",EDGE,"E0.7"),sQuery(id+"F0.wireOp",EDGE,"E0.8"),subQ1,subQ0,sQuery(id+"F0.wireOp",EDGE,"E0.11"),sQuery(id+"F0.wireOp",EDGE,"E0.12"),sQuery(id+"F0.wireOp",EDGE,"E0.13"),sQuery(id+"F0.wireOp",EDGE,"E0.14"),sQuery(id+"F0.wireOp",EDGE,"E0.15"),sQuery(id+"F0.wireOp",EDGE,"E1"),sQuery(id+"F0.wireOp",EDGE,"E2.1"),sQuery(id+"F0.wireOp",EDGE,"E2.3"),sQuery(id+"F0.wireOp",EDGE,"E2.5"),sQuery(id+"F0.wireOp",EDGE,"E2.7"),sQuery(id+"F0.wireOp",EDGE,"E2.9"),sQuery(id+"F0.wireOp",EDGE,"E2.11"),sQuery(id+"F0.wireOp",EDGE,"E2.13"),sQuery(id+"F0.wireOp",EDGE,"E2.15"),sQuery(id+"F0.wireOp",EDGE,"E3.1"),sQuery(id+"F0.wireOp",EDGE,"E3.3"),sQuery(id+"F0.wireOp",EDGE,"E3.5"),sQuery(id+"F0.wireOp",EDGE,"E3.7"),sQuery(id+"F0.wireOp",EDGE,"E3.9"),sQuery(id+"F0.wireOp",EDGE,"E3.11"),sQuery(id+"F0.wireOp",EDGE,"E3.13"),sQuery(id+"F0.wireOp",EDGE,"E3.15"),sQuery(id+"F0.wireOp",EDGE,"E4"),sQuery(id+"F0.wireOp",EDGE,"E5"),sQuery(id+"F0.wireOp",EDGE,"E6"),sQuery(id+"F0.wireOp",EDGE,"E7"),sQuery(id+"F0.wireOp",EDGE,"E8"),sQuery(id+"F0.wireOp",EDGE,"E9"),sQuery(id+"F0.wireOp",EDGE,"E10"),sQuery(id+"F0.wireOp",EDGE,"E11"),sQuery(id+"F0.wireOp",EDGE,"E12"),sQuery(id+"F0.wireOp",EDGE,"E13"),sQuery(id+"F0.wireOp",EDGE,"E14"),sQuery(id+"F0.wireOp",EDGE,"E15"),sQuery(id+"F0.wireOp",EDGE,"E16"),sQuery(id+"F0.wireOp",EDGE,"E17"),sQuery(id+"F0.wireOp",EDGE,"E18"),sQuery(id+"F0.wireOp",EDGE,"E19")])],"isStart":true})],"blendedInto":[makeQuery(id+"F1.opExtrude","CAP_FACE",FACE,{"disambiguationData":[OSD([sQuery(id+"F0.wireOp",EDGE,"E0.0"),sQuery(id+"F0.wireOp",EDGE,"E0.1"),sQuery(id+"F0.wireOp",EDGE,"E0.2"),sQuery(id+"F0.wireOp",EDGE,"E0.3"),sQuery(id+"F0.wireOp",EDGE,"E0.4"),sQuery(id+"F0.wireOp",EDGE,"E0.5"),sQuery(id+"F0.wireOp",EDGE,"E0.6"),sQuery(id+"F0.wireOp",EDGE,"E0.7"),sQuery(id+"F0.wireOp",EDGE,"E0.8"),subQ1,subQ0,sQuery(id+"F0.wireOp",EDGE,"E0.11"),sQuery(id+"F0.wireOp",EDGE,"E0.12"),sQuery(id+"F0.wireOp",EDGE,"E0.13"),sQuery(id+"F0.wireOp",EDGE,"E0.14"),sQuery(id+"F0.wireOp",EDGE,"E0.15"),sQuery(id+"F0.wireOp",EDGE,"E1"),sQuery(id+"F0.wireOp",EDGE,"E2.1"),sQuery(id+"F0.wireOp",EDGE,"E2.3"),sQuery(id+"F0.wireOp",EDGE,"E2.5"),sQuery(id+"F0.wireOp",EDGE,"E2.7"),sQuery(id+"F0.wireOp",EDGE,"E2.9"),sQuery(id+"F0.wireOp",EDGE,"E2.11"),sQuery(id+"F0.wireOp",EDGE,"E2.13"),sQuery(id+"F0.wireOp",EDGE,"E2.15"),sQuery(id+"F0.wireOp",EDGE,"E3.1"),sQuery(id+"F0.wireOp",EDGE,"E3.3"),sQuery(id+"F0.wireOp",EDGE,"E3.5"),sQuery(id+"F0.wireOp",EDGE,"E3.7"),sQuery(id+"F0.wireOp",EDGE,"E3.9"),sQuery(id+"F0.wireOp",EDGE,"E3.11"),sQuery(id+"F0.wireOp",EDGE,"E3.13"),sQuery(id+"F0.wireOp",EDGE,"E3.15"),sQuery(id+"F0.wireOp",EDGE,"E4"),sQuery(id+"F0.wireOp",EDGE,"E5"),sQuery(id+"F0.wireOp",EDGE,"E6"),sQuery(id+"F0.wireOp",EDGE,"E7"),sQuery(id+"F0.wireOp",EDGE,"E8"),sQuery(id+"F0.wireOp",EDGE,"E9"),sQuery(id+"F0.wireOp",EDGE,"E10"),sQuery(id+"F0.wireOp",EDGE,"E11"),sQuery(id+"F0.wireOp",EDGE,"E12"),sQuery(id+"F0.wireOp",EDGE,"E13"),sQuery(id+"F0.wireOp",EDGE,"E14"),sQuery(id+"F0.wireOp",EDGE,"E15"),sQuery(id+"F0.wireOp",EDGE,"E16"),sQuery(id+"F0.wireOp",EDGE,"E17"),sQuery(id+"F0.wireOp",EDGE,"E18"),sQuery(id+"F0.wireOp",EDGE,"E19")])],"isStart":true})]});}
            var Q12;
            {var subQ0=sQuery(id+"F0.wireOp",EDGE,"E0.9");var subQ1=sQuery(id+"F0.wireOp",EDGE,"E0.8");Q12=makeQuery(id+"F2.opFillet","BLEND_EDGE",EDGE,{"blendedFrom":[makeQuery(id+"F1.opExtrude","SWEPT_EDGE",EDGE,{"disambiguationData":[OSD([subQ1,subQ0])]}),makeQuery(id+"F1.opExtrude","CAP_FACE",FACE,{"disambiguationData":[OSD([sQuery(id+"F0.wireOp",EDGE,"E0.0"),sQuery(id+"F0.wireOp",EDGE,"E0.1"),sQuery(id+"F0.wireOp",EDGE,"E0.2"),sQuery(id+"F0.wireOp",EDGE,"E0.3"),sQuery(id+"F0.wireOp",EDGE,"E0.4"),sQuery(id+"F0.wireOp",EDGE,"E0.5"),sQuery(id+"F0.wireOp",EDGE,"E0.6"),sQuery(id+"F0.wireOp",EDGE,"E0.7"),subQ1,subQ0,sQuery(id+"F0.wireOp",EDGE,"E0.10"),sQuery(id+"F0.wireOp",EDGE,"E0.11"),sQuery(id+"F0.wireOp",EDGE,"E0.12"),sQuery(id+"F0.wireOp",EDGE,"E0.13"),sQuery(id+"F0.wireOp",EDGE,"E0.14"),sQuery(id+"F0.wireOp",EDGE,"E0.15"),sQuery(id+"F0.wireOp",EDGE,"E1"),sQuery(id+"F0.wireOp",EDGE,"E2.1"),sQuery(id+"F0.wireOp",EDGE,"E2.3"),sQuery(id+"F0.wireOp",EDGE,"E2.5"),sQuery(id+"F0.wireOp",EDGE,"E2.7"),sQuery(id+"F0.wireOp",EDGE,"E2.9"),sQuery(id+"F0.wireOp",EDGE,"E2.11"),sQuery(id+"F0.wireOp",EDGE,"E2.13"),sQuery(id+"F0.wireOp",EDGE,"E2.15"),sQuery(id+"F0.wireOp",EDGE,"E3.1"),sQuery(id+"F0.wireOp",EDGE,"E3.3"),sQuery(id+"F0.wireOp",EDGE,"E3.5"),sQuery(id+"F0.wireOp",EDGE,"E3.7"),sQuery(id+"F0.wireOp",EDGE,"E3.9"),sQuery(id+"F0.wireOp",EDGE,"E3.11"),sQuery(id+"F0.wireOp",EDGE,"E3.13"),sQuery(id+"F0.wireOp",EDGE,"E3.15"),sQuery(id+"F0.wireOp",EDGE,"E4"),sQuery(id+"F0.wireOp",EDGE,"E5"),sQuery(id+"F0.wireOp",EDGE,"E6"),sQuery(id+"F0.wireOp",EDGE,"E7"),sQuery(id+"F0.wireOp",EDGE,"E8"),sQuery(id+"F0.wireOp",EDGE,"E9"),sQuery(id+"F0.wireOp",EDGE,"E10"),sQuery(id+"F0.wireOp",EDGE,"E11"),sQuery(id+"F0.wireOp",EDGE,"E12"),sQuery(id+"F0.wireOp",EDGE,"E13"),sQuery(id+"F0.wireOp",EDGE,"E14"),sQuery(id+"F0.wireOp",EDGE,"E15"),sQuery(id+"F0.wireOp",EDGE,"E16"),sQuery(id+"F0.wireOp",EDGE,"E17"),sQuery(id+"F0.wireOp",EDGE,"E18"),sQuery(id+"F0.wireOp",EDGE,"E19")])],"isStart":true})],"blendedInto":[makeQuery(id+"F1.opExtrude","CAP_FACE",FACE,{"disambiguationData":[OSD([sQuery(id+"F0.wireOp",EDGE,"E0.0"),sQuery(id+"F0.wireOp",EDGE,"E0.1"),sQuery(id+"F0.wireOp",EDGE,"E0.2"),sQuery(id+"F0.wireOp",EDGE,"E0.3"),sQuery(id+"F0.wireOp",EDGE,"E0.4"),sQuery(id+"F0.wireOp",EDGE,"E0.5"),sQuery(id+"F0.wireOp",EDGE,"E0.6"),sQuery(id+"F0.wireOp",EDGE,"E0.7"),subQ1,subQ0,sQuery(id+"F0.wireOp",EDGE,"E0.10"),sQuery(id+"F0.wireOp",EDGE,"E0.11"),sQuery(id+"F0.wireOp",EDGE,"E0.12"),sQuery(id+"F0.wireOp",EDGE,"E0.13"),sQuery(id+"F0.wireOp",EDGE,"E0.14"),sQuery(id+"F0.wireOp",EDGE,"E0.15"),sQuery(id+"F0.wireOp",EDGE,"E1"),sQuery(id+"F0.wireOp",EDGE,"E2.1"),sQuery(id+"F0.wireOp",EDGE,"E2.3"),sQuery(id+"F0.wireOp",EDGE,"E2.5"),sQuery(id+"F0.wireOp",EDGE,"E2.7"),sQuery(id+"F0.wireOp",EDGE,"E2.9"),sQuery(id+"F0.wireOp",EDGE,"E2.11"),sQuery(id+"F0.wireOp",EDGE,"E2.13"),sQuery(id+"F0.wireOp",EDGE,"E2.15"),sQuery(id+"F0.wireOp",EDGE,"E3.1"),sQuery(id+"F0.wireOp",EDGE,"E3.3"),sQuery(id+"F0.wireOp",EDGE,"E3.5"),sQuery(id+"F0.wireOp",EDGE,"E3.7"),sQuery(id+"F0.wireOp",EDGE,"E3.9"),sQuery(id+"F0.wireOp",EDGE,"E3.11"),sQuery(id+"F0.wireOp",EDGE,"E3.13"),sQuery(id+"F0.wireOp",EDGE,"E3.15"),sQuery(id+"F0.wireOp",EDGE,"E4"),sQuery(id+"F0.wireOp",EDGE,"E5"),sQuery(id+"F0.wireOp",EDGE,"E6"),sQuery(id+"F0.wireOp",EDGE,"E7"),sQuery(id+"F0.wireOp",EDGE,"E8"),sQuery(id+"F0.wireOp",EDGE,"E9"),sQuery(id+"F0.wireOp",EDGE,"E10"),sQuery(id+"F0.wireOp",EDGE,"E11"),sQuery(id+"F0.wireOp",EDGE,"E12"),sQuery(id+"F0.wireOp",EDGE,"E13"),sQuery(id+"F0.wireOp",EDGE,"E14"),sQuery(id+"F0.wireOp",EDGE,"E15"),sQuery(id+"F0.wireOp",EDGE,"E16"),sQuery(id+"F0.wireOp",EDGE,"E17"),sQuery(id+"F0.wireOp",EDGE,"E18"),sQuery(id+"F0.wireOp",EDGE,"E19")])],"isStart":true})]});}
            var Q13;
            {var subQ0=sQuery(id+"F0.wireOp",EDGE,"E0.8");var subQ1=sQuery(id+"F0.wireOp",EDGE,"E0.7");Q13=makeQuery(id+"F2.opFillet","BLEND_EDGE",EDGE,{"blendedFrom":[makeQuery(id+"F1.opExtrude","SWEPT_EDGE",EDGE,{"disambiguationData":[OSD([subQ1,subQ0])]}),makeQuery(id+"F1.opExtrude","CAP_FACE",FACE,{"disambiguationData":[OSD([sQuery(id+"F0.wireOp",EDGE,"E0.0"),sQuery(id+"F0.wireOp",EDGE,"E0.1"),sQuery(id+"F0.wireOp",EDGE,"E0.2"),sQuery(id+"F0.wireOp",EDGE,"E0.3"),sQuery(id+"F0.wireOp",EDGE,"E0.4"),sQuery(id+"F0.wireOp",EDGE,"E0.5"),sQuery(id+"F0.wireOp",EDGE,"E0.6"),subQ1,subQ0,sQuery(id+"F0.wireOp",EDGE,"E0.9"),sQuery(id+"F0.wireOp",EDGE,"E0.10"),sQuery(id+"F0.wireOp",EDGE,"E0.11"),sQuery(id+"F0.wireOp",EDGE,"E0.12"),sQuery(id+"F0.wireOp",EDGE,"E0.13"),sQuery(id+"F0.wireOp",EDGE,"E0.14"),sQuery(id+"F0.wireOp",EDGE,"E0.15"),sQuery(id+"F0.wireOp",EDGE,"E1"),sQuery(id+"F0.wireOp",EDGE,"E2.1"),sQuery(id+"F0.wireOp",EDGE,"E2.3"),sQuery(id+"F0.wireOp",EDGE,"E2.5"),sQuery(id+"F0.wireOp",EDGE,"E2.7"),sQuery(id+"F0.wireOp",EDGE,"E2.9"),sQuery(id+"F0.wireOp",EDGE,"E2.11"),sQuery(id+"F0.wireOp",EDGE,"E2.13"),sQuery(id+"F0.wireOp",EDGE,"E2.15"),sQuery(id+"F0.wireOp",EDGE,"E3.1"),sQuery(id+"F0.wireOp",EDGE,"E3.3"),sQuery(id+"F0.wireOp",EDGE,"E3.5"),sQuery(id+"F0.wireOp",EDGE,"E3.7"),sQuery(id+"F0.wireOp",EDGE,"E3.9"),sQuery(id+"F0.wireOp",EDGE,"E3.11"),sQuery(id+"F0.wireOp",EDGE,"E3.13"),sQuery(id+"F0.wireOp",EDGE,"E3.15"),sQuery(id+"F0.wireOp",EDGE,"E4"),sQuery(id+"F0.wireOp",EDGE,"E5"),sQuery(id+"F0.wireOp",EDGE,"E6"),sQuery(id+"F0.wireOp",EDGE,"E7"),sQuery(id+"F0.wireOp",EDGE,"E8"),sQuery(id+"F0.wireOp",EDGE,"E9"),sQuery(id+"F0.wireOp",EDGE,"E10"),sQuery(id+"F0.wireOp",EDGE,"E11"),sQuery(id+"F0.wireOp",EDGE,"E12"),sQuery(id+"F0.wireOp",EDGE,"E13"),sQuery(id+"F0.wireOp",EDGE,"E14"),sQuery(id+"F0.wireOp",EDGE,"E15"),sQuery(id+"F0.wireOp",EDGE,"E16"),sQuery(id+"F0.wireOp",EDGE,"E17"),sQuery(id+"F0.wireOp",EDGE,"E18"),sQuery(id+"F0.wireOp",EDGE,"E19")])],"isStart":true})],"blendedInto":[makeQuery(id+"F1.opExtrude","CAP_FACE",FACE,{"disambiguationData":[OSD([sQuery(id+"F0.wireOp",EDGE,"E0.0"),sQuery(id+"F0.wireOp",EDGE,"E0.1"),sQuery(id+"F0.wireOp",EDGE,"E0.2"),sQuery(id+"F0.wireOp",EDGE,"E0.3"),sQuery(id+"F0.wireOp",EDGE,"E0.4"),sQuery(id+"F0.wireOp",EDGE,"E0.5"),sQuery(id+"F0.wireOp",EDGE,"E0.6"),subQ1,subQ0,sQuery(id+"F0.wireOp",EDGE,"E0.9"),sQuery(id+"F0.wireOp",EDGE,"E0.10"),sQuery(id+"F0.wireOp",EDGE,"E0.11"),sQuery(id+"F0.wireOp",EDGE,"E0.12"),sQuery(id+"F0.wireOp",EDGE,"E0.13"),sQuery(id+"F0.wireOp",EDGE,"E0.14"),sQuery(id+"F0.wireOp",EDGE,"E0.15"),sQuery(id+"F0.wireOp",EDGE,"E1"),sQuery(id+"F0.wireOp",EDGE,"E2.1"),sQuery(id+"F0.wireOp",EDGE,"E2.3"),sQuery(id+"F0.wireOp",EDGE,"E2.5"),sQuery(id+"F0.wireOp",EDGE,"E2.7"),sQuery(id+"F0.wireOp",EDGE,"E2.9"),sQuery(id+"F0.wireOp",EDGE,"E2.11"),sQuery(id+"F0.wireOp",EDGE,"E2.13"),sQuery(id+"F0.wireOp",EDGE,"E2.15"),sQuery(id+"F0.wireOp",EDGE,"E3.1"),sQuery(id+"F0.wireOp",EDGE,"E3.3"),sQuery(id+"F0.wireOp",EDGE,"E3.5"),sQuery(id+"F0.wireOp",EDGE,"E3.7"),sQuery(id+"F0.wireOp",EDGE,"E3.9"),sQuery(id+"F0.wireOp",EDGE,"E3.11"),sQuery(id+"F0.wireOp",EDGE,"E3.13"),sQuery(id+"F0.wireOp",EDGE,"E3.15"),sQuery(id+"F0.wireOp",EDGE,"E4"),sQuery(id+"F0.wireOp",EDGE,"E5"),sQuery(id+"F0.wireOp",EDGE,"E6"),sQuery(id+"F0.wireOp",EDGE,"E7"),sQuery(id+"F0.wireOp",EDGE,"E8"),sQuery(id+"F0.wireOp",EDGE,"E9"),sQuery(id+"F0.wireOp",EDGE,"E10"),sQuery(id+"F0.wireOp",EDGE,"E11"),sQuery(id+"F0.wireOp",EDGE,"E12"),sQuery(id+"F0.wireOp",EDGE,"E13"),sQuery(id+"F0.wireOp",EDGE,"E14"),sQuery(id+"F0.wireOp",EDGE,"E15"),sQuery(id+"F0.wireOp",EDGE,"E16"),sQuery(id+"F0.wireOp",EDGE,"E17"),sQuery(id+"F0.wireOp",EDGE,"E18"),sQuery(id+"F0.wireOp",EDGE,"E19")])],"isStart":true})]});}
            var Q14;
            {var subQ0=sQuery(id+"F0.wireOp",EDGE,"E0.7");var subQ1=sQuery(id+"F0.wireOp",EDGE,"E0.6");Q14=makeQuery(id+"F2.opFillet","BLEND_EDGE",EDGE,{"blendedFrom":[makeQuery(id+"F1.opExtrude","SWEPT_EDGE",EDGE,{"disambiguationData":[OSD([subQ1,subQ0])]}),makeQuery(id+"F1.opExtrude","CAP_FACE",FACE,{"disambiguationData":[OSD([sQuery(id+"F0.wireOp",EDGE,"E0.0"),sQuery(id+"F0.wireOp",EDGE,"E0.1"),sQuery(id+"F0.wireOp",EDGE,"E0.2"),sQuery(id+"F0.wireOp",EDGE,"E0.3"),sQuery(id+"F0.wireOp",EDGE,"E0.4"),sQuery(id+"F0.wireOp",EDGE,"E0.5"),subQ1,subQ0,sQuery(id+"F0.wireOp",EDGE,"E0.8"),sQuery(id+"F0.wireOp",EDGE,"E0.9"),sQuery(id+"F0.wireOp",EDGE,"E0.10"),sQuery(id+"F0.wireOp",EDGE,"E0.11"),sQuery(id+"F0.wireOp",EDGE,"E0.12"),sQuery(id+"F0.wireOp",EDGE,"E0.13"),sQuery(id+"F0.wireOp",EDGE,"E0.14"),sQuery(id+"F0.wireOp",EDGE,"E0.15"),sQuery(id+"F0.wireOp",EDGE,"E1"),sQuery(id+"F0.wireOp",EDGE,"E2.1"),sQuery(id+"F0.wireOp",EDGE,"E2.3"),sQuery(id+"F0.wireOp",EDGE,"E2.5"),sQuery(id+"F0.wireOp",EDGE,"E2.7"),sQuery(id+"F0.wireOp",EDGE,"E2.9"),sQuery(id+"F0.wireOp",EDGE,"E2.11"),sQuery(id+"F0.wireOp",EDGE,"E2.13"),sQuery(id+"F0.wireOp",EDGE,"E2.15"),sQuery(id+"F0.wireOp",EDGE,"E3.1"),sQuery(id+"F0.wireOp",EDGE,"E3.3"),sQuery(id+"F0.wireOp",EDGE,"E3.5"),sQuery(id+"F0.wireOp",EDGE,"E3.7"),sQuery(id+"F0.wireOp",EDGE,"E3.9"),sQuery(id+"F0.wireOp",EDGE,"E3.11"),sQuery(id+"F0.wireOp",EDGE,"E3.13"),sQuery(id+"F0.wireOp",EDGE,"E3.15"),sQuery(id+"F0.wireOp",EDGE,"E4"),sQuery(id+"F0.wireOp",EDGE,"E5"),sQuery(id+"F0.wireOp",EDGE,"E6"),sQuery(id+"F0.wireOp",EDGE,"E7"),sQuery(id+"F0.wireOp",EDGE,"E8"),sQuery(id+"F0.wireOp",EDGE,"E9"),sQuery(id+"F0.wireOp",EDGE,"E10"),sQuery(id+"F0.wireOp",EDGE,"E11"),sQuery(id+"F0.wireOp",EDGE,"E12"),sQuery(id+"F0.wireOp",EDGE,"E13"),sQuery(id+"F0.wireOp",EDGE,"E14"),sQuery(id+"F0.wireOp",EDGE,"E15"),sQuery(id+"F0.wireOp",EDGE,"E16"),sQuery(id+"F0.wireOp",EDGE,"E17"),sQuery(id+"F0.wireOp",EDGE,"E18"),sQuery(id+"F0.wireOp",EDGE,"E19")])],"isStart":true})],"blendedInto":[makeQuery(id+"F1.opExtrude","CAP_FACE",FACE,{"disambiguationData":[OSD([sQuery(id+"F0.wireOp",EDGE,"E0.0"),sQuery(id+"F0.wireOp",EDGE,"E0.1"),sQuery(id+"F0.wireOp",EDGE,"E0.2"),sQuery(id+"F0.wireOp",EDGE,"E0.3"),sQuery(id+"F0.wireOp",EDGE,"E0.4"),sQuery(id+"F0.wireOp",EDGE,"E0.5"),subQ1,subQ0,sQuery(id+"F0.wireOp",EDGE,"E0.8"),sQuery(id+"F0.wireOp",EDGE,"E0.9"),sQuery(id+"F0.wireOp",EDGE,"E0.10"),sQuery(id+"F0.wireOp",EDGE,"E0.11"),sQuery(id+"F0.wireOp",EDGE,"E0.12"),sQuery(id+"F0.wireOp",EDGE,"E0.13"),sQuery(id+"F0.wireOp",EDGE,"E0.14"),sQuery(id+"F0.wireOp",EDGE,"E0.15"),sQuery(id+"F0.wireOp",EDGE,"E1"),sQuery(id+"F0.wireOp",EDGE,"E2.1"),sQuery(id+"F0.wireOp",EDGE,"E2.3"),sQuery(id+"F0.wireOp",EDGE,"E2.5"),sQuery(id+"F0.wireOp",EDGE,"E2.7"),sQuery(id+"F0.wireOp",EDGE,"E2.9"),sQuery(id+"F0.wireOp",EDGE,"E2.11"),sQuery(id+"F0.wireOp",EDGE,"E2.13"),sQuery(id+"F0.wireOp",EDGE,"E2.15"),sQuery(id+"F0.wireOp",EDGE,"E3.1"),sQuery(id+"F0.wireOp",EDGE,"E3.3"),sQuery(id+"F0.wireOp",EDGE,"E3.5"),sQuery(id+"F0.wireOp",EDGE,"E3.7"),sQuery(id+"F0.wireOp",EDGE,"E3.9"),sQuery(id+"F0.wireOp",EDGE,"E3.11"),sQuery(id+"F0.wireOp",EDGE,"E3.13"),sQuery(id+"F0.wireOp",EDGE,"E3.15"),sQuery(id+"F0.wireOp",EDGE,"E4"),sQuery(id+"F0.wireOp",EDGE,"E5"),sQuery(id+"F0.wireOp",EDGE,"E6"),sQuery(id+"F0.wireOp",EDGE,"E7"),sQuery(id+"F0.wireOp",EDGE,"E8"),sQuery(id+"F0.wireOp",EDGE,"E9"),sQuery(id+"F0.wireOp",EDGE,"E10"),sQuery(id+"F0.wireOp",EDGE,"E11"),sQuery(id+"F0.wireOp",EDGE,"E12"),sQuery(id+"F0.wireOp",EDGE,"E13"),sQuery(id+"F0.wireOp",EDGE,"E14"),sQuery(id+"F0.wireOp",EDGE,"E15"),sQuery(id+"F0.wireOp",EDGE,"E16"),sQuery(id+"F0.wireOp",EDGE,"E17"),sQuery(id+"F0.wireOp",EDGE,"E18"),sQuery(id+"F0.wireOp",EDGE,"E19")])],"isStart":true})]});}
            var Q15;
            {var subQ0=sQuery(id+"F0.wireOp",EDGE,"E0.6");var subQ1=sQuery(id+"F0.wireOp",EDGE,"E0.5");Q15=makeQuery(id+"F2.opFillet","BLEND_EDGE",EDGE,{"blendedFrom":[makeQuery(id+"F1.opExtrude","SWEPT_EDGE",EDGE,{"disambiguationData":[OSD([subQ1,subQ0])]}),makeQuery(id+"F1.opExtrude","CAP_FACE",FACE,{"disambiguationData":[OSD([sQuery(id+"F0.wireOp",EDGE,"E0.0"),sQuery(id+"F0.wireOp",EDGE,"E0.1"),sQuery(id+"F0.wireOp",EDGE,"E0.2"),sQuery(id+"F0.wireOp",EDGE,"E0.3"),sQuery(id+"F0.wireOp",EDGE,"E0.4"),subQ1,subQ0,sQuery(id+"F0.wireOp",EDGE,"E0.7"),sQuery(id+"F0.wireOp",EDGE,"E0.8"),sQuery(id+"F0.wireOp",EDGE,"E0.9"),sQuery(id+"F0.wireOp",EDGE,"E0.10"),sQuery(id+"F0.wireOp",EDGE,"E0.11"),sQuery(id+"F0.wireOp",EDGE,"E0.12"),sQuery(id+"F0.wireOp",EDGE,"E0.13"),sQuery(id+"F0.wireOp",EDGE,"E0.14"),sQuery(id+"F0.wireOp",EDGE,"E0.15"),sQuery(id+"F0.wireOp",EDGE,"E1"),sQuery(id+"F0.wireOp",EDGE,"E2.1"),sQuery(id+"F0.wireOp",EDGE,"E2.3"),sQuery(id+"F0.wireOp",EDGE,"E2.5"),sQuery(id+"F0.wireOp",EDGE,"E2.7"),sQuery(id+"F0.wireOp",EDGE,"E2.9"),sQuery(id+"F0.wireOp",EDGE,"E2.11"),sQuery(id+"F0.wireOp",EDGE,"E2.13"),sQuery(id+"F0.wireOp",EDGE,"E2.15"),sQuery(id+"F0.wireOp",EDGE,"E3.1"),sQuery(id+"F0.wireOp",EDGE,"E3.3"),sQuery(id+"F0.wireOp",EDGE,"E3.5"),sQuery(id+"F0.wireOp",EDGE,"E3.7"),sQuery(id+"F0.wireOp",EDGE,"E3.9"),sQuery(id+"F0.wireOp",EDGE,"E3.11"),sQuery(id+"F0.wireOp",EDGE,"E3.13"),sQuery(id+"F0.wireOp",EDGE,"E3.15"),sQuery(id+"F0.wireOp",EDGE,"E4"),sQuery(id+"F0.wireOp",EDGE,"E5"),sQuery(id+"F0.wireOp",EDGE,"E6"),sQuery(id+"F0.wireOp",EDGE,"E7"),sQuery(id+"F0.wireOp",EDGE,"E8"),sQuery(id+"F0.wireOp",EDGE,"E9"),sQuery(id+"F0.wireOp",EDGE,"E10"),sQuery(id+"F0.wireOp",EDGE,"E11"),sQuery(id+"F0.wireOp",EDGE,"E12"),sQuery(id+"F0.wireOp",EDGE,"E13"),sQuery(id+"F0.wireOp",EDGE,"E14"),sQuery(id+"F0.wireOp",EDGE,"E15"),sQuery(id+"F0.wireOp",EDGE,"E16"),sQuery(id+"F0.wireOp",EDGE,"E17"),sQuery(id+"F0.wireOp",EDGE,"E18"),sQuery(id+"F0.wireOp",EDGE,"E19")])],"isStart":true})],"blendedInto":[makeQuery(id+"F1.opExtrude","CAP_FACE",FACE,{"disambiguationData":[OSD([sQuery(id+"F0.wireOp",EDGE,"E0.0"),sQuery(id+"F0.wireOp",EDGE,"E0.1"),sQuery(id+"F0.wireOp",EDGE,"E0.2"),sQuery(id+"F0.wireOp",EDGE,"E0.3"),sQuery(id+"F0.wireOp",EDGE,"E0.4"),subQ1,subQ0,sQuery(id+"F0.wireOp",EDGE,"E0.7"),sQuery(id+"F0.wireOp",EDGE,"E0.8"),sQuery(id+"F0.wireOp",EDGE,"E0.9"),sQuery(id+"F0.wireOp",EDGE,"E0.10"),sQuery(id+"F0.wireOp",EDGE,"E0.11"),sQuery(id+"F0.wireOp",EDGE,"E0.12"),sQuery(id+"F0.wireOp",EDGE,"E0.13"),sQuery(id+"F0.wireOp",EDGE,"E0.14"),sQuery(id+"F0.wireOp",EDGE,"E0.15"),sQuery(id+"F0.wireOp",EDGE,"E1"),sQuery(id+"F0.wireOp",EDGE,"E2.1"),sQuery(id+"F0.wireOp",EDGE,"E2.3"),sQuery(id+"F0.wireOp",EDGE,"E2.5"),sQuery(id+"F0.wireOp",EDGE,"E2.7"),sQuery(id+"F0.wireOp",EDGE,"E2.9"),sQuery(id+"F0.wireOp",EDGE,"E2.11"),sQuery(id+"F0.wireOp",EDGE,"E2.13"),sQuery(id+"F0.wireOp",EDGE,"E2.15"),sQuery(id+"F0.wireOp",EDGE,"E3.1"),sQuery(id+"F0.wireOp",EDGE,"E3.3"),sQuery(id+"F0.wireOp",EDGE,"E3.5"),sQuery(id+"F0.wireOp",EDGE,"E3.7"),sQuery(id+"F0.wireOp",EDGE,"E3.9"),sQuery(id+"F0.wireOp",EDGE,"E3.11"),sQuery(id+"F0.wireOp",EDGE,"E3.13"),sQuery(id+"F0.wireOp",EDGE,"E3.15"),sQuery(id+"F0.wireOp",EDGE,"E4"),sQuery(id+"F0.wireOp",EDGE,"E5"),sQuery(id+"F0.wireOp",EDGE,"E6"),sQuery(id+"F0.wireOp",EDGE,"E7"),sQuery(id+"F0.wireOp",EDGE,"E8"),sQuery(id+"F0.wireOp",EDGE,"E9"),sQuery(id+"F0.wireOp",EDGE,"E10"),sQuery(id+"F0.wireOp",EDGE,"E11"),sQuery(id+"F0.wireOp",EDGE,"E12"),sQuery(id+"F0.wireOp",EDGE,"E13"),sQuery(id+"F0.wireOp",EDGE,"E14"),sQuery(id+"F0.wireOp",EDGE,"E15"),sQuery(id+"F0.wireOp",EDGE,"E16"),sQuery(id+"F0.wireOp",EDGE,"E17"),sQuery(id+"F0.wireOp",EDGE,"E18"),sQuery(id+"F0.wireOp",EDGE,"E19")])],"isStart":true})]});}
            fillet(context, id + "F3", {"entities" : qUnion([Q0, Q1, Q2, Q3, Q4, Q5, Q6, Q7, Q8, Q9, Q10, Q11, Q12, Q13, Q14, Q15]), "radius" : 2 * mm, "tangentPropagation" : true, "allowEdgeOverflow" : false});
        }
        {
            var Q0;
            Q0=makeQuery(id+"F1.opExtrude","SWEPT_EDGE",EDGE,{"disambiguationData":[OSD([sQuery(id+"F0.wireOp",EDGE,"E3.11"),sQuery(id+"F0.wireOp",EDGE,"E3.12"),sQuery(id+"F0.wireOp",EDGE,"E4")])]});
            var Q1;
            Q1=makeQuery(id+"F1.opExtrude","SWEPT_EDGE",EDGE,{"disambiguationData":[OSD([sQuery(id+"F0.wireOp",EDGE,"E3.10"),sQuery(id+"F0.wireOp",EDGE,"E3.11"),sQuery(id+"F0.wireOp",EDGE,"E19")])]});
            var Q2;
            Q2=makeQuery(id+"F1.opExtrude","SWEPT_EDGE",EDGE,{"disambiguationData":[OSD([sQuery(id+"F0.wireOp",EDGE,"E2.11"),sQuery(id+"F0.wireOp",EDGE,"E2.12"),sQuery(id+"F0.wireOp",EDGE,"E4")])]});
            var Q3;
            Q3=makeQuery(id+"F1.opExtrude","SWEPT_EDGE",EDGE,{"disambiguationData":[OSD([sQuery(id+"F0.wireOp",EDGE,"E2.10"),sQuery(id+"F0.wireOp",EDGE,"E2.11"),sQuery(id+"F0.wireOp",EDGE,"E19")])]});
            chamfer(context, id + "F4", {"entities" : qUnion([Q0, Q1, Q2, Q3]), "width" : 1 * mm, "tangentPropagation" : true});
        }
        {
            var Q0;
            Q0=makeQuery(id+"F1.opExtrude","SWEPT_EDGE",EDGE,{"disambiguationData":[OSD([sQuery(id+"F0.wireOp",EDGE,"E3.9"),sQuery(id+"F0.wireOp",EDGE,"E3.10"),sQuery(id+"F0.wireOp",EDGE,"E18")])]});
            var Q1;
            Q1=makeQuery(id+"F1.opExtrude","SWEPT_EDGE",EDGE,{"disambiguationData":[OSD([sQuery(id+"F0.wireOp",EDGE,"E2.9"),sQuery(id+"F0.wireOp",EDGE,"E2.10"),sQuery(id+"F0.wireOp",EDGE,"E18")])]});
            var Q2;
            Q2=makeQuery(id+"F1.opExtrude","SWEPT_EDGE",EDGE,{"disambiguationData":[OSD([sQuery(id+"F0.wireOp",EDGE,"E2.8"),sQuery(id+"F0.wireOp",EDGE,"E2.9"),sQuery(id+"F0.wireOp",EDGE,"E17")])]});
            var Q3;
            Q3=makeQuery(id+"F1.opExtrude","SWEPT_EDGE",EDGE,{"disambiguationData":[OSD([sQuery(id+"F0.wireOp",EDGE,"E3.8"),sQuery(id+"F0.wireOp",EDGE,"E3.9"),sQuery(id+"F0.wireOp",EDGE,"E17")])]});
            var Q4;
            Q4=makeQuery(id+"F1.opExtrude","SWEPT_EDGE",EDGE,{"disambiguationData":[OSD([sQuery(id+"F0.wireOp",EDGE,"E3.7"),sQuery(id+"F0.wireOp",EDGE,"E3.8"),sQuery(id+"F0.wireOp",EDGE,"E16")])]});
            var Q5;
            Q5=makeQuery(id+"F1.opExtrude","SWEPT_EDGE",EDGE,{"disambiguationData":[OSD([sQuery(id+"F0.wireOp",EDGE,"E2.7"),sQuery(id+"F0.wireOp",EDGE,"E2.8"),sQuery(id+"F0.wireOp",EDGE,"E16")])]});
            var Q6;
            Q6=makeQuery(id+"F1.opExtrude","SWEPT_EDGE",EDGE,{"disambiguationData":[OSD([sQuery(id+"F0.wireOp",EDGE,"E2.6"),sQuery(id+"F0.wireOp",EDGE,"E2.7"),sQuery(id+"F0.wireOp",EDGE,"E15")])]});
            var Q7;
            Q7=makeQuery(id+"F1.opExtrude","SWEPT_EDGE",EDGE,{"disambiguationData":[OSD([sQuery(id+"F0.wireOp",EDGE,"E3.6"),sQuery(id+"F0.wireOp",EDGE,"E3.7"),sQuery(id+"F0.wireOp",EDGE,"E15")])]});
            var Q8;
            Q8=makeQuery(id+"F1.opExtrude","SWEPT_EDGE",EDGE,{"disambiguationData":[OSD([sQuery(id+"F0.wireOp",EDGE,"E3.4"),sQuery(id+"F0.wireOp",EDGE,"E3.5"),sQuery(id+"F0.wireOp",EDGE,"E13")])]});
            var Q9;
            Q9=makeQuery(id+"F1.opExtrude","SWEPT_EDGE",EDGE,{"disambiguationData":[OSD([sQuery(id+"F0.wireOp",EDGE,"E2.4"),sQuery(id+"F0.wireOp",EDGE,"E2.5"),sQuery(id+"F0.wireOp",EDGE,"E13")])]});
            var Q10;
            Q10=makeQuery(id+"F1.opExtrude","SWEPT_EDGE",EDGE,{"disambiguationData":[OSD([sQuery(id+"F0.wireOp",EDGE,"E2.5"),sQuery(id+"F0.wireOp",EDGE,"E2.6"),sQuery(id+"F0.wireOp",EDGE,"E14")])]});
            var Q11;
            Q11=makeQuery(id+"F1.opExtrude","SWEPT_EDGE",EDGE,{"disambiguationData":[OSD([sQuery(id+"F0.wireOp",EDGE,"E3.5"),sQuery(id+"F0.wireOp",EDGE,"E3.6"),sQuery(id+"F0.wireOp",EDGE,"E14")])]});
            var Q12;
            Q12=makeQuery(id+"F1.opExtrude","SWEPT_EDGE",EDGE,{"disambiguationData":[OSD([sQuery(id+"F0.wireOp",EDGE,"E3.2"),sQuery(id+"F0.wireOp",EDGE,"E3.3"),sQuery(id+"F0.wireOp",EDGE,"E11")])]});
            var Q13;
            Q13=makeQuery(id+"F1.opExtrude","SWEPT_EDGE",EDGE,{"disambiguationData":[OSD([sQuery(id+"F0.wireOp",EDGE,"E3.3"),sQuery(id+"F0.wireOp",EDGE,"E3.4"),sQuery(id+"F0.wireOp",EDGE,"E12")])]});
            var Q14;
            Q14=makeQuery(id+"F1.opExtrude","SWEPT_EDGE",EDGE,{"disambiguationData":[OSD([sQuery(id+"F0.wireOp",EDGE,"E2.3"),sQuery(id+"F0.wireOp",EDGE,"E2.4"),sQuery(id+"F0.wireOp",EDGE,"E12")])]});
            var Q15;
            Q15=makeQuery(id+"F1.opExtrude","SWEPT_EDGE",EDGE,{"disambiguationData":[OSD([sQuery(id+"F0.wireOp",EDGE,"E2.2"),sQuery(id+"F0.wireOp",EDGE,"E2.3"),sQuery(id+"F0.wireOp",EDGE,"E11")])]});
            var Q16;
            Q16=makeQuery(id+"F1.opExtrude","SWEPT_EDGE",EDGE,{"disambiguationData":[OSD([sQuery(id+"F0.wireOp",EDGE,"E2.0"),sQuery(id+"F0.wireOp",EDGE,"E2.1"),sQuery(id+"F0.wireOp",EDGE,"E9")])]});
            var Q17;
            Q17=makeQuery(id+"F1.opExtrude","SWEPT_EDGE",EDGE,{"disambiguationData":[OSD([sQuery(id+"F0.wireOp",EDGE,"E2.1"),sQuery(id+"F0.wireOp",EDGE,"E2.2"),sQuery(id+"F0.wireOp",EDGE,"E10")])]});
            var Q18;
            Q18=makeQuery(id+"F1.opExtrude","SWEPT_EDGE",EDGE,{"disambiguationData":[OSD([sQuery(id+"F0.wireOp",EDGE,"E3.1"),sQuery(id+"F0.wireOp",EDGE,"E3.2"),sQuery(id+"F0.wireOp",EDGE,"E10")])]});
            var Q19;
            Q19=makeQuery(id+"F1.opExtrude","SWEPT_EDGE",EDGE,{"disambiguationData":[OSD([sQuery(id+"F0.wireOp",EDGE,"E3.0"),sQuery(id+"F0.wireOp",EDGE,"E3.1"),sQuery(id+"F0.wireOp",EDGE,"E9")])]});
            var Q20;
            Q20=makeQuery(id+"F1.opExtrude","SWEPT_EDGE",EDGE,{"disambiguationData":[OSD([sQuery(id+"F0.wireOp",EDGE,"E3.0"),sQuery(id+"F0.wireOp",EDGE,"E3.15"),sQuery(id+"F0.wireOp",EDGE,"E8")])]});
            var Q21;
            Q21=makeQuery(id+"F1.opExtrude","SWEPT_EDGE",EDGE,{"disambiguationData":[OSD([sQuery(id+"F0.wireOp",EDGE,"E3.14"),sQuery(id+"F0.wireOp",EDGE,"E3.15"),sQuery(id+"F0.wireOp",EDGE,"E7")])]});
            var Q22;
            Q22=makeQuery(id+"F1.opExtrude","SWEPT_EDGE",EDGE,{"disambiguationData":[OSD([sQuery(id+"F0.wireOp",EDGE,"E2.14"),sQuery(id+"F0.wireOp",EDGE,"E2.15"),sQuery(id+"F0.wireOp",EDGE,"E7")])]});
            var Q23;
            Q23=makeQuery(id+"F1.opExtrude","SWEPT_EDGE",EDGE,{"disambiguationData":[OSD([sQuery(id+"F0.wireOp",EDGE,"E2.0"),sQuery(id+"F0.wireOp",EDGE,"E2.15"),sQuery(id+"F0.wireOp",EDGE,"E8")])]});
            var Q24;
            Q24=makeQuery(id+"F1.opExtrude","SWEPT_EDGE",EDGE,{"disambiguationData":[OSD([sQuery(id+"F0.wireOp",EDGE,"E3.12"),sQuery(id+"F0.wireOp",EDGE,"E3.13"),sQuery(id+"F0.wireOp",EDGE,"E5")])]});
            var Q25;
            Q25=makeQuery(id+"F1.opExtrude","SWEPT_EDGE",EDGE,{"disambiguationData":[OSD([sQuery(id+"F0.wireOp",EDGE,"E2.12"),sQuery(id+"F0.wireOp",EDGE,"E2.13"),sQuery(id+"F0.wireOp",EDGE,"E5")])]});
            var Q26;
            Q26=makeQuery(id+"F1.opExtrude","SWEPT_EDGE",EDGE,{"disambiguationData":[OSD([sQuery(id+"F0.wireOp",EDGE,"E2.13"),sQuery(id+"F0.wireOp",EDGE,"E2.14"),sQuery(id+"F0.wireOp",EDGE,"E6")])]});
            var Q27;
            Q27=makeQuery(id+"F1.opExtrude","SWEPT_EDGE",EDGE,{"disambiguationData":[OSD([sQuery(id+"F0.wireOp",EDGE,"E3.13"),sQuery(id+"F0.wireOp",EDGE,"E3.14"),sQuery(id+"F0.wireOp",EDGE,"E6")])]});
            chamfer(context, id + "F5", {"entities" : qUnion([Q0, Q1, Q2, Q3, Q4, Q5, Q6, Q7, Q8, Q9, Q10, Q11, Q12, Q13, Q14, Q15, Q16, Q17, Q18, Q19, Q20, Q21, Q22, Q23, Q24, Q25, Q26, Q27]), "width" : 1 * mm, "tangentPropagation" : true});
        }
        {
            var Q0;
            {var subQ0=sQuery(id+"F0.wireOp",EDGE,"E4");var subQ1=sQuery(id+"F0.wireOp",EDGE,"E3.11");Q0=makeQuery(id+"F4.opChamfer","BLEND_EDGE",EDGE,{"blendedFrom":[makeQuery(id+"F1.opExtrude","SWEPT_EDGE",EDGE,{"disambiguationData":[OSD([subQ1,sQuery(id+"F0.wireOp",EDGE,"E3.12"),subQ0])]}),makeQuery(id+"F1.opExtrude","CAP_FACE",FACE,{"disambiguationData":[OSD([sQuery(id+"F0.wireOp",EDGE,"E0.0"),sQuery(id+"F0.wireOp",EDGE,"E0.1"),sQuery(id+"F0.wireOp",EDGE,"E0.2"),sQuery(id+"F0.wireOp",EDGE,"E0.3"),sQuery(id+"F0.wireOp",EDGE,"E0.4"),sQuery(id+"F0.wireOp",EDGE,"E0.5"),sQuery(id+"F0.wireOp",EDGE,"E0.6"),sQuery(id+"F0.wireOp",EDGE,"E0.7"),sQuery(id+"F0.wireOp",EDGE,"E0.8"),sQuery(id+"F0.wireOp",EDGE,"E0.9"),sQuery(id+"F0.wireOp",EDGE,"E0.10"),sQuery(id+"F0.wireOp",EDGE,"E0.11"),sQuery(id+"F0.wireOp",EDGE,"E0.12"),sQuery(id+"F0.wireOp",EDGE,"E0.13"),sQuery(id+"F0.wireOp",EDGE,"E0.14"),sQuery(id+"F0.wireOp",EDGE,"E0.15"),sQuery(id+"F0.wireOp",EDGE,"E1"),sQuery(id+"F0.wireOp",EDGE,"E2.1"),sQuery(id+"F0.wireOp",EDGE,"E2.3"),sQuery(id+"F0.wireOp",EDGE,"E2.5"),sQuery(id+"F0.wireOp",EDGE,"E2.7"),sQuery(id+"F0.wireOp",EDGE,"E2.9"),sQuery(id+"F0.wireOp",EDGE,"E2.11"),sQuery(id+"F0.wireOp",EDGE,"E2.13"),sQuery(id+"F0.wireOp",EDGE,"E2.15"),sQuery(id+"F0.wireOp",EDGE,"E3.1"),sQuery(id+"F0.wireOp",EDGE,"E3.3"),sQuery(id+"F0.wireOp",EDGE,"E3.5"),sQuery(id+"F0.wireOp",EDGE,"E3.7"),sQuery(id+"F0.wireOp",EDGE,"E3.9"),subQ1,sQuery(id+"F0.wireOp",EDGE,"E3.13"),sQuery(id+"F0.wireOp",EDGE,"E3.15"),subQ0,sQuery(id+"F0.wireOp",EDGE,"E5"),sQuery(id+"F0.wireOp",EDGE,"E6"),sQuery(id+"F0.wireOp",EDGE,"E7"),sQuery(id+"F0.wireOp",EDGE,"E8"),sQuery(id+"F0.wireOp",EDGE,"E9"),sQuery(id+"F0.wireOp",EDGE,"E10"),sQuery(id+"F0.wireOp",EDGE,"E11"),sQuery(id+"F0.wireOp",EDGE,"E12"),sQuery(id+"F0.wireOp",EDGE,"E13"),sQuery(id+"F0.wireOp",EDGE,"E14"),sQuery(id+"F0.wireOp",EDGE,"E15"),sQuery(id+"F0.wireOp",EDGE,"E16"),sQuery(id+"F0.wireOp",EDGE,"E17"),sQuery(id+"F0.wireOp",EDGE,"E18"),sQuery(id+"F0.wireOp",EDGE,"E19")])],"isStart":true})],"blendedInto":[makeQuery(id+"F1.opExtrude","CAP_FACE",FACE,{"disambiguationData":[OSD([sQuery(id+"F0.wireOp",EDGE,"E0.0"),sQuery(id+"F0.wireOp",EDGE,"E0.1"),sQuery(id+"F0.wireOp",EDGE,"E0.2"),sQuery(id+"F0.wireOp",EDGE,"E0.3"),sQuery(id+"F0.wireOp",EDGE,"E0.4"),sQuery(id+"F0.wireOp",EDGE,"E0.5"),sQuery(id+"F0.wireOp",EDGE,"E0.6"),sQuery(id+"F0.wireOp",EDGE,"E0.7"),sQuery(id+"F0.wireOp",EDGE,"E0.8"),sQuery(id+"F0.wireOp",EDGE,"E0.9"),sQuery(id+"F0.wireOp",EDGE,"E0.10"),sQuery(id+"F0.wireOp",EDGE,"E0.11"),sQuery(id+"F0.wireOp",EDGE,"E0.12"),sQuery(id+"F0.wireOp",EDGE,"E0.13"),sQuery(id+"F0.wireOp",EDGE,"E0.14"),sQuery(id+"F0.wireOp",EDGE,"E0.15"),sQuery(id+"F0.wireOp",EDGE,"E1"),sQuery(id+"F0.wireOp",EDGE,"E2.1"),sQuery(id+"F0.wireOp",EDGE,"E2.3"),sQuery(id+"F0.wireOp",EDGE,"E2.5"),sQuery(id+"F0.wireOp",EDGE,"E2.7"),sQuery(id+"F0.wireOp",EDGE,"E2.9"),sQuery(id+"F0.wireOp",EDGE,"E2.11"),sQuery(id+"F0.wireOp",EDGE,"E2.13"),sQuery(id+"F0.wireOp",EDGE,"E2.15"),sQuery(id+"F0.wireOp",EDGE,"E3.1"),sQuery(id+"F0.wireOp",EDGE,"E3.3"),sQuery(id+"F0.wireOp",EDGE,"E3.5"),sQuery(id+"F0.wireOp",EDGE,"E3.7"),sQuery(id+"F0.wireOp",EDGE,"E3.9"),subQ1,sQuery(id+"F0.wireOp",EDGE,"E3.13"),sQuery(id+"F0.wireOp",EDGE,"E3.15"),subQ0,sQuery(id+"F0.wireOp",EDGE,"E5"),sQuery(id+"F0.wireOp",EDGE,"E6"),sQuery(id+"F0.wireOp",EDGE,"E7"),sQuery(id+"F0.wireOp",EDGE,"E8"),sQuery(id+"F0.wireOp",EDGE,"E9"),sQuery(id+"F0.wireOp",EDGE,"E10"),sQuery(id+"F0.wireOp",EDGE,"E11"),sQuery(id+"F0.wireOp",EDGE,"E12"),sQuery(id+"F0.wireOp",EDGE,"E13"),sQuery(id+"F0.wireOp",EDGE,"E14"),sQuery(id+"F0.wireOp",EDGE,"E15"),sQuery(id+"F0.wireOp",EDGE,"E16"),sQuery(id+"F0.wireOp",EDGE,"E17"),sQuery(id+"F0.wireOp",EDGE,"E18"),sQuery(id+"F0.wireOp",EDGE,"E19")])],"isStart":true})]});}
            var Q1;
            Q1=makeQuery(id+"F1.opExtrude","CAP_EDGE",EDGE,{"disambiguationData":[OSD([sQuery(id+"F0.wireOp",EDGE,"E3.11")])],"isStart":true});
            var Q2;
            {var subQ0=sQuery(id+"F0.wireOp",EDGE,"E19");var subQ1=sQuery(id+"F0.wireOp",EDGE,"E3.11");Q2=makeQuery(id+"F4.opChamfer","BLEND_EDGE",EDGE,{"blendedFrom":[makeQuery(id+"F1.opExtrude","SWEPT_EDGE",EDGE,{"disambiguationData":[OSD([sQuery(id+"F0.wireOp",EDGE,"E3.10"),subQ1,subQ0])]}),makeQuery(id+"F1.opExtrude","CAP_FACE",FACE,{"disambiguationData":[OSD([sQuery(id+"F0.wireOp",EDGE,"E0.0"),sQuery(id+"F0.wireOp",EDGE,"E0.1"),sQuery(id+"F0.wireOp",EDGE,"E0.2"),sQuery(id+"F0.wireOp",EDGE,"E0.3"),sQuery(id+"F0.wireOp",EDGE,"E0.4"),sQuery(id+"F0.wireOp",EDGE,"E0.5"),sQuery(id+"F0.wireOp",EDGE,"E0.6"),sQuery(id+"F0.wireOp",EDGE,"E0.7"),sQuery(id+"F0.wireOp",EDGE,"E0.8"),sQuery(id+"F0.wireOp",EDGE,"E0.9"),sQuery(id+"F0.wireOp",EDGE,"E0.10"),sQuery(id+"F0.wireOp",EDGE,"E0.11"),sQuery(id+"F0.wireOp",EDGE,"E0.12"),sQuery(id+"F0.wireOp",EDGE,"E0.13"),sQuery(id+"F0.wireOp",EDGE,"E0.14"),sQuery(id+"F0.wireOp",EDGE,"E0.15"),sQuery(id+"F0.wireOp",EDGE,"E1"),sQuery(id+"F0.wireOp",EDGE,"E2.1"),sQuery(id+"F0.wireOp",EDGE,"E2.3"),sQuery(id+"F0.wireOp",EDGE,"E2.5"),sQuery(id+"F0.wireOp",EDGE,"E2.7"),sQuery(id+"F0.wireOp",EDGE,"E2.9"),sQuery(id+"F0.wireOp",EDGE,"E2.11"),sQuery(id+"F0.wireOp",EDGE,"E2.13"),sQuery(id+"F0.wireOp",EDGE,"E2.15"),sQuery(id+"F0.wireOp",EDGE,"E3.1"),sQuery(id+"F0.wireOp",EDGE,"E3.3"),sQuery(id+"F0.wireOp",EDGE,"E3.5"),sQuery(id+"F0.wireOp",EDGE,"E3.7"),sQuery(id+"F0.wireOp",EDGE,"E3.9"),subQ1,sQuery(id+"F0.wireOp",EDGE,"E3.13"),sQuery(id+"F0.wireOp",EDGE,"E3.15"),sQuery(id+"F0.wireOp",EDGE,"E4"),sQuery(id+"F0.wireOp",EDGE,"E5"),sQuery(id+"F0.wireOp",EDGE,"E6"),sQuery(id+"F0.wireOp",EDGE,"E7"),sQuery(id+"F0.wireOp",EDGE,"E8"),sQuery(id+"F0.wireOp",EDGE,"E9"),sQuery(id+"F0.wireOp",EDGE,"E10"),sQuery(id+"F0.wireOp",EDGE,"E11"),sQuery(id+"F0.wireOp",EDGE,"E12"),sQuery(id+"F0.wireOp",EDGE,"E13"),sQuery(id+"F0.wireOp",EDGE,"E14"),sQuery(id+"F0.wireOp",EDGE,"E15"),sQuery(id+"F0.wireOp",EDGE,"E16"),sQuery(id+"F0.wireOp",EDGE,"E17"),sQuery(id+"F0.wireOp",EDGE,"E18"),subQ0])],"isStart":true})],"blendedInto":[makeQuery(id+"F1.opExtrude","CAP_FACE",FACE,{"disambiguationData":[OSD([sQuery(id+"F0.wireOp",EDGE,"E0.0"),sQuery(id+"F0.wireOp",EDGE,"E0.1"),sQuery(id+"F0.wireOp",EDGE,"E0.2"),sQuery(id+"F0.wireOp",EDGE,"E0.3"),sQuery(id+"F0.wireOp",EDGE,"E0.4"),sQuery(id+"F0.wireOp",EDGE,"E0.5"),sQuery(id+"F0.wireOp",EDGE,"E0.6"),sQuery(id+"F0.wireOp",EDGE,"E0.7"),sQuery(id+"F0.wireOp",EDGE,"E0.8"),sQuery(id+"F0.wireOp",EDGE,"E0.9"),sQuery(id+"F0.wireOp",EDGE,"E0.10"),sQuery(id+"F0.wireOp",EDGE,"E0.11"),sQuery(id+"F0.wireOp",EDGE,"E0.12"),sQuery(id+"F0.wireOp",EDGE,"E0.13"),sQuery(id+"F0.wireOp",EDGE,"E0.14"),sQuery(id+"F0.wireOp",EDGE,"E0.15"),sQuery(id+"F0.wireOp",EDGE,"E1"),sQuery(id+"F0.wireOp",EDGE,"E2.1"),sQuery(id+"F0.wireOp",EDGE,"E2.3"),sQuery(id+"F0.wireOp",EDGE,"E2.5"),sQuery(id+"F0.wireOp",EDGE,"E2.7"),sQuery(id+"F0.wireOp",EDGE,"E2.9"),sQuery(id+"F0.wireOp",EDGE,"E2.11"),sQuery(id+"F0.wireOp",EDGE,"E2.13"),sQuery(id+"F0.wireOp",EDGE,"E2.15"),sQuery(id+"F0.wireOp",EDGE,"E3.1"),sQuery(id+"F0.wireOp",EDGE,"E3.3"),sQuery(id+"F0.wireOp",EDGE,"E3.5"),sQuery(id+"F0.wireOp",EDGE,"E3.7"),sQuery(id+"F0.wireOp",EDGE,"E3.9"),subQ1,sQuery(id+"F0.wireOp",EDGE,"E3.13"),sQuery(id+"F0.wireOp",EDGE,"E3.15"),sQuery(id+"F0.wireOp",EDGE,"E4"),sQuery(id+"F0.wireOp",EDGE,"E5"),sQuery(id+"F0.wireOp",EDGE,"E6"),sQuery(id+"F0.wireOp",EDGE,"E7"),sQuery(id+"F0.wireOp",EDGE,"E8"),sQuery(id+"F0.wireOp",EDGE,"E9"),sQuery(id+"F0.wireOp",EDGE,"E10"),sQuery(id+"F0.wireOp",EDGE,"E11"),sQuery(id+"F0.wireOp",EDGE,"E12"),sQuery(id+"F0.wireOp",EDGE,"E13"),sQuery(id+"F0.wireOp",EDGE,"E14"),sQuery(id+"F0.wireOp",EDGE,"E15"),sQuery(id+"F0.wireOp",EDGE,"E16"),sQuery(id+"F0.wireOp",EDGE,"E17"),sQuery(id+"F0.wireOp",EDGE,"E18"),subQ0])],"isStart":true})]});}
            var Q3;
            Q3=makeQuery(id+"F1.opExtrude","CAP_EDGE",EDGE,{"disambiguationData":[OSD([sQuery(id+"F0.wireOp",EDGE,"E19")])],"isStart":true});
            var Q4;
            {var subQ0=sQuery(id+"F0.wireOp",EDGE,"E19");var subQ1=sQuery(id+"F0.wireOp",EDGE,"E2.11");Q4=makeQuery(id+"F4.opChamfer","BLEND_EDGE",EDGE,{"blendedFrom":[makeQuery(id+"F1.opExtrude","SWEPT_EDGE",EDGE,{"disambiguationData":[OSD([sQuery(id+"F0.wireOp",EDGE,"E2.10"),subQ1,subQ0])]}),makeQuery(id+"F1.opExtrude","CAP_FACE",FACE,{"disambiguationData":[OSD([sQuery(id+"F0.wireOp",EDGE,"E0.0"),sQuery(id+"F0.wireOp",EDGE,"E0.1"),sQuery(id+"F0.wireOp",EDGE,"E0.2"),sQuery(id+"F0.wireOp",EDGE,"E0.3"),sQuery(id+"F0.wireOp",EDGE,"E0.4"),sQuery(id+"F0.wireOp",EDGE,"E0.5"),sQuery(id+"F0.wireOp",EDGE,"E0.6"),sQuery(id+"F0.wireOp",EDGE,"E0.7"),sQuery(id+"F0.wireOp",EDGE,"E0.8"),sQuery(id+"F0.wireOp",EDGE,"E0.9"),sQuery(id+"F0.wireOp",EDGE,"E0.10"),sQuery(id+"F0.wireOp",EDGE,"E0.11"),sQuery(id+"F0.wireOp",EDGE,"E0.12"),sQuery(id+"F0.wireOp",EDGE,"E0.13"),sQuery(id+"F0.wireOp",EDGE,"E0.14"),sQuery(id+"F0.wireOp",EDGE,"E0.15"),sQuery(id+"F0.wireOp",EDGE,"E1"),sQuery(id+"F0.wireOp",EDGE,"E2.1"),sQuery(id+"F0.wireOp",EDGE,"E2.3"),sQuery(id+"F0.wireOp",EDGE,"E2.5"),sQuery(id+"F0.wireOp",EDGE,"E2.7"),sQuery(id+"F0.wireOp",EDGE,"E2.9"),subQ1,sQuery(id+"F0.wireOp",EDGE,"E2.13"),sQuery(id+"F0.wireOp",EDGE,"E2.15"),sQuery(id+"F0.wireOp",EDGE,"E3.1"),sQuery(id+"F0.wireOp",EDGE,"E3.3"),sQuery(id+"F0.wireOp",EDGE,"E3.5"),sQuery(id+"F0.wireOp",EDGE,"E3.7"),sQuery(id+"F0.wireOp",EDGE,"E3.9"),sQuery(id+"F0.wireOp",EDGE,"E3.11"),sQuery(id+"F0.wireOp",EDGE,"E3.13"),sQuery(id+"F0.wireOp",EDGE,"E3.15"),sQuery(id+"F0.wireOp",EDGE,"E4"),sQuery(id+"F0.wireOp",EDGE,"E5"),sQuery(id+"F0.wireOp",EDGE,"E6"),sQuery(id+"F0.wireOp",EDGE,"E7"),sQuery(id+"F0.wireOp",EDGE,"E8"),sQuery(id+"F0.wireOp",EDGE,"E9"),sQuery(id+"F0.wireOp",EDGE,"E10"),sQuery(id+"F0.wireOp",EDGE,"E11"),sQuery(id+"F0.wireOp",EDGE,"E12"),sQuery(id+"F0.wireOp",EDGE,"E13"),sQuery(id+"F0.wireOp",EDGE,"E14"),sQuery(id+"F0.wireOp",EDGE,"E15"),sQuery(id+"F0.wireOp",EDGE,"E16"),sQuery(id+"F0.wireOp",EDGE,"E17"),sQuery(id+"F0.wireOp",EDGE,"E18"),subQ0])],"isStart":true})],"blendedInto":[makeQuery(id+"F1.opExtrude","CAP_FACE",FACE,{"disambiguationData":[OSD([sQuery(id+"F0.wireOp",EDGE,"E0.0"),sQuery(id+"F0.wireOp",EDGE,"E0.1"),sQuery(id+"F0.wireOp",EDGE,"E0.2"),sQuery(id+"F0.wireOp",EDGE,"E0.3"),sQuery(id+"F0.wireOp",EDGE,"E0.4"),sQuery(id+"F0.wireOp",EDGE,"E0.5"),sQuery(id+"F0.wireOp",EDGE,"E0.6"),sQuery(id+"F0.wireOp",EDGE,"E0.7"),sQuery(id+"F0.wireOp",EDGE,"E0.8"),sQuery(id+"F0.wireOp",EDGE,"E0.9"),sQuery(id+"F0.wireOp",EDGE,"E0.10"),sQuery(id+"F0.wireOp",EDGE,"E0.11"),sQuery(id+"F0.wireOp",EDGE,"E0.12"),sQuery(id+"F0.wireOp",EDGE,"E0.13"),sQuery(id+"F0.wireOp",EDGE,"E0.14"),sQuery(id+"F0.wireOp",EDGE,"E0.15"),sQuery(id+"F0.wireOp",EDGE,"E1"),sQuery(id+"F0.wireOp",EDGE,"E2.1"),sQuery(id+"F0.wireOp",EDGE,"E2.3"),sQuery(id+"F0.wireOp",EDGE,"E2.5"),sQuery(id+"F0.wireOp",EDGE,"E2.7"),sQuery(id+"F0.wireOp",EDGE,"E2.9"),subQ1,sQuery(id+"F0.wireOp",EDGE,"E2.13"),sQuery(id+"F0.wireOp",EDGE,"E2.15"),sQuery(id+"F0.wireOp",EDGE,"E3.1"),sQuery(id+"F0.wireOp",EDGE,"E3.3"),sQuery(id+"F0.wireOp",EDGE,"E3.5"),sQuery(id+"F0.wireOp",EDGE,"E3.7"),sQuery(id+"F0.wireOp",EDGE,"E3.9"),sQuery(id+"F0.wireOp",EDGE,"E3.11"),sQuery(id+"F0.wireOp",EDGE,"E3.13"),sQuery(id+"F0.wireOp",EDGE,"E3.15"),sQuery(id+"F0.wireOp",EDGE,"E4"),sQuery(id+"F0.wireOp",EDGE,"E5"),sQuery(id+"F0.wireOp",EDGE,"E6"),sQuery(id+"F0.wireOp",EDGE,"E7"),sQuery(id+"F0.wireOp",EDGE,"E8"),sQuery(id+"F0.wireOp",EDGE,"E9"),sQuery(id+"F0.wireOp",EDGE,"E10"),sQuery(id+"F0.wireOp",EDGE,"E11"),sQuery(id+"F0.wireOp",EDGE,"E12"),sQuery(id+"F0.wireOp",EDGE,"E13"),sQuery(id+"F0.wireOp",EDGE,"E14"),sQuery(id+"F0.wireOp",EDGE,"E15"),sQuery(id+"F0.wireOp",EDGE,"E16"),sQuery(id+"F0.wireOp",EDGE,"E17"),sQuery(id+"F0.wireOp",EDGE,"E18"),subQ0])],"isStart":true})]});}
            var Q5;
            Q5=makeQuery(id+"F1.opExtrude","CAP_EDGE",EDGE,{"disambiguationData":[OSD([sQuery(id+"F0.wireOp",EDGE,"E2.11")])],"isStart":true});
            var Q6;
            {var subQ0=sQuery(id+"F0.wireOp",EDGE,"E4");var subQ1=sQuery(id+"F0.wireOp",EDGE,"E2.11");Q6=makeQuery(id+"F4.opChamfer","BLEND_EDGE",EDGE,{"blendedFrom":[makeQuery(id+"F1.opExtrude","SWEPT_EDGE",EDGE,{"disambiguationData":[OSD([subQ1,sQuery(id+"F0.wireOp",EDGE,"E2.12"),subQ0])]}),makeQuery(id+"F1.opExtrude","CAP_FACE",FACE,{"disambiguationData":[OSD([sQuery(id+"F0.wireOp",EDGE,"E0.0"),sQuery(id+"F0.wireOp",EDGE,"E0.1"),sQuery(id+"F0.wireOp",EDGE,"E0.2"),sQuery(id+"F0.wireOp",EDGE,"E0.3"),sQuery(id+"F0.wireOp",EDGE,"E0.4"),sQuery(id+"F0.wireOp",EDGE,"E0.5"),sQuery(id+"F0.wireOp",EDGE,"E0.6"),sQuery(id+"F0.wireOp",EDGE,"E0.7"),sQuery(id+"F0.wireOp",EDGE,"E0.8"),sQuery(id+"F0.wireOp",EDGE,"E0.9"),sQuery(id+"F0.wireOp",EDGE,"E0.10"),sQuery(id+"F0.wireOp",EDGE,"E0.11"),sQuery(id+"F0.wireOp",EDGE,"E0.12"),sQuery(id+"F0.wireOp",EDGE,"E0.13"),sQuery(id+"F0.wireOp",EDGE,"E0.14"),sQuery(id+"F0.wireOp",EDGE,"E0.15"),sQuery(id+"F0.wireOp",EDGE,"E1"),sQuery(id+"F0.wireOp",EDGE,"E2.1"),sQuery(id+"F0.wireOp",EDGE,"E2.3"),sQuery(id+"F0.wireOp",EDGE,"E2.5"),sQuery(id+"F0.wireOp",EDGE,"E2.7"),sQuery(id+"F0.wireOp",EDGE,"E2.9"),subQ1,sQuery(id+"F0.wireOp",EDGE,"E2.13"),sQuery(id+"F0.wireOp",EDGE,"E2.15"),sQuery(id+"F0.wireOp",EDGE,"E3.1"),sQuery(id+"F0.wireOp",EDGE,"E3.3"),sQuery(id+"F0.wireOp",EDGE,"E3.5"),sQuery(id+"F0.wireOp",EDGE,"E3.7"),sQuery(id+"F0.wireOp",EDGE,"E3.9"),sQuery(id+"F0.wireOp",EDGE,"E3.11"),sQuery(id+"F0.wireOp",EDGE,"E3.13"),sQuery(id+"F0.wireOp",EDGE,"E3.15"),subQ0,sQuery(id+"F0.wireOp",EDGE,"E5"),sQuery(id+"F0.wireOp",EDGE,"E6"),sQuery(id+"F0.wireOp",EDGE,"E7"),sQuery(id+"F0.wireOp",EDGE,"E8"),sQuery(id+"F0.wireOp",EDGE,"E9"),sQuery(id+"F0.wireOp",EDGE,"E10"),sQuery(id+"F0.wireOp",EDGE,"E11"),sQuery(id+"F0.wireOp",EDGE,"E12"),sQuery(id+"F0.wireOp",EDGE,"E13"),sQuery(id+"F0.wireOp",EDGE,"E14"),sQuery(id+"F0.wireOp",EDGE,"E15"),sQuery(id+"F0.wireOp",EDGE,"E16"),sQuery(id+"F0.wireOp",EDGE,"E17"),sQuery(id+"F0.wireOp",EDGE,"E18"),sQuery(id+"F0.wireOp",EDGE,"E19")])],"isStart":true})],"blendedInto":[makeQuery(id+"F1.opExtrude","CAP_FACE",FACE,{"disambiguationData":[OSD([sQuery(id+"F0.wireOp",EDGE,"E0.0"),sQuery(id+"F0.wireOp",EDGE,"E0.1"),sQuery(id+"F0.wireOp",EDGE,"E0.2"),sQuery(id+"F0.wireOp",EDGE,"E0.3"),sQuery(id+"F0.wireOp",EDGE,"E0.4"),sQuery(id+"F0.wireOp",EDGE,"E0.5"),sQuery(id+"F0.wireOp",EDGE,"E0.6"),sQuery(id+"F0.wireOp",EDGE,"E0.7"),sQuery(id+"F0.wireOp",EDGE,"E0.8"),sQuery(id+"F0.wireOp",EDGE,"E0.9"),sQuery(id+"F0.wireOp",EDGE,"E0.10"),sQuery(id+"F0.wireOp",EDGE,"E0.11"),sQuery(id+"F0.wireOp",EDGE,"E0.12"),sQuery(id+"F0.wireOp",EDGE,"E0.13"),sQuery(id+"F0.wireOp",EDGE,"E0.14"),sQuery(id+"F0.wireOp",EDGE,"E0.15"),sQuery(id+"F0.wireOp",EDGE,"E1"),sQuery(id+"F0.wireOp",EDGE,"E2.1"),sQuery(id+"F0.wireOp",EDGE,"E2.3"),sQuery(id+"F0.wireOp",EDGE,"E2.5"),sQuery(id+"F0.wireOp",EDGE,"E2.7"),sQuery(id+"F0.wireOp",EDGE,"E2.9"),subQ1,sQuery(id+"F0.wireOp",EDGE,"E2.13"),sQuery(id+"F0.wireOp",EDGE,"E2.15"),sQuery(id+"F0.wireOp",EDGE,"E3.1"),sQuery(id+"F0.wireOp",EDGE,"E3.3"),sQuery(id+"F0.wireOp",EDGE,"E3.5"),sQuery(id+"F0.wireOp",EDGE,"E3.7"),sQuery(id+"F0.wireOp",EDGE,"E3.9"),sQuery(id+"F0.wireOp",EDGE,"E3.11"),sQuery(id+"F0.wireOp",EDGE,"E3.13"),sQuery(id+"F0.wireOp",EDGE,"E3.15"),subQ0,sQuery(id+"F0.wireOp",EDGE,"E5"),sQuery(id+"F0.wireOp",EDGE,"E6"),sQuery(id+"F0.wireOp",EDGE,"E7"),sQuery(id+"F0.wireOp",EDGE,"E8"),sQuery(id+"F0.wireOp",EDGE,"E9"),sQuery(id+"F0.wireOp",EDGE,"E10"),sQuery(id+"F0.wireOp",EDGE,"E11"),sQuery(id+"F0.wireOp",EDGE,"E12"),sQuery(id+"F0.wireOp",EDGE,"E13"),sQuery(id+"F0.wireOp",EDGE,"E14"),sQuery(id+"F0.wireOp",EDGE,"E15"),sQuery(id+"F0.wireOp",EDGE,"E16"),sQuery(id+"F0.wireOp",EDGE,"E17"),sQuery(id+"F0.wireOp",EDGE,"E18"),sQuery(id+"F0.wireOp",EDGE,"E19")])],"isStart":true})]});}
            var Q7;
            Q7=makeQuery(id+"F1.opExtrude","CAP_EDGE",EDGE,{"disambiguationData":[OSD([sQuery(id+"F0.wireOp",EDGE,"E4")])],"isStart":true});
            var Q8;
            Q8=makeQuery(id+"F1.opExtrude","CAP_EDGE",EDGE,{"disambiguationData":[OSD([sQuery(id+"F0.wireOp",EDGE,"E5")])],"isStart":true});
            var Q9;
            {var subQ0=sQuery(id+"F0.wireOp",EDGE,"E5");var subQ1=sQuery(id+"F0.wireOp",EDGE,"E3.13");Q9=makeQuery(id+"F5.opChamfer","BLEND_EDGE",EDGE,{"blendedFrom":[makeQuery(id+"F1.opExtrude","SWEPT_EDGE",EDGE,{"disambiguationData":[OSD([sQuery(id+"F0.wireOp",EDGE,"E3.12"),subQ1,subQ0])]}),makeQuery(id+"F1.opExtrude","CAP_FACE",FACE,{"disambiguationData":[OSD([sQuery(id+"F0.wireOp",EDGE,"E0.0"),sQuery(id+"F0.wireOp",EDGE,"E0.1"),sQuery(id+"F0.wireOp",EDGE,"E0.2"),sQuery(id+"F0.wireOp",EDGE,"E0.3"),sQuery(id+"F0.wireOp",EDGE,"E0.4"),sQuery(id+"F0.wireOp",EDGE,"E0.5"),sQuery(id+"F0.wireOp",EDGE,"E0.6"),sQuery(id+"F0.wireOp",EDGE,"E0.7"),sQuery(id+"F0.wireOp",EDGE,"E0.8"),sQuery(id+"F0.wireOp",EDGE,"E0.9"),sQuery(id+"F0.wireOp",EDGE,"E0.10"),sQuery(id+"F0.wireOp",EDGE,"E0.11"),sQuery(id+"F0.wireOp",EDGE,"E0.12"),sQuery(id+"F0.wireOp",EDGE,"E0.13"),sQuery(id+"F0.wireOp",EDGE,"E0.14"),sQuery(id+"F0.wireOp",EDGE,"E0.15"),sQuery(id+"F0.wireOp",EDGE,"E1"),sQuery(id+"F0.wireOp",EDGE,"E2.1"),sQuery(id+"F0.wireOp",EDGE,"E2.3"),sQuery(id+"F0.wireOp",EDGE,"E2.5"),sQuery(id+"F0.wireOp",EDGE,"E2.7"),sQuery(id+"F0.wireOp",EDGE,"E2.9"),sQuery(id+"F0.wireOp",EDGE,"E2.11"),sQuery(id+"F0.wireOp",EDGE,"E2.13"),sQuery(id+"F0.wireOp",EDGE,"E2.15"),sQuery(id+"F0.wireOp",EDGE,"E3.1"),sQuery(id+"F0.wireOp",EDGE,"E3.3"),sQuery(id+"F0.wireOp",EDGE,"E3.5"),sQuery(id+"F0.wireOp",EDGE,"E3.7"),sQuery(id+"F0.wireOp",EDGE,"E3.9"),sQuery(id+"F0.wireOp",EDGE,"E3.11"),subQ1,sQuery(id+"F0.wireOp",EDGE,"E3.15"),sQuery(id+"F0.wireOp",EDGE,"E4"),subQ0,sQuery(id+"F0.wireOp",EDGE,"E6"),sQuery(id+"F0.wireOp",EDGE,"E7"),sQuery(id+"F0.wireOp",EDGE,"E8"),sQuery(id+"F0.wireOp",EDGE,"E9"),sQuery(id+"F0.wireOp",EDGE,"E10"),sQuery(id+"F0.wireOp",EDGE,"E11"),sQuery(id+"F0.wireOp",EDGE,"E12"),sQuery(id+"F0.wireOp",EDGE,"E13"),sQuery(id+"F0.wireOp",EDGE,"E14"),sQuery(id+"F0.wireOp",EDGE,"E15"),sQuery(id+"F0.wireOp",EDGE,"E16"),sQuery(id+"F0.wireOp",EDGE,"E17"),sQuery(id+"F0.wireOp",EDGE,"E18"),sQuery(id+"F0.wireOp",EDGE,"E19")])],"isStart":true})],"blendedInto":[makeQuery(id+"F1.opExtrude","CAP_FACE",FACE,{"disambiguationData":[OSD([sQuery(id+"F0.wireOp",EDGE,"E0.0"),sQuery(id+"F0.wireOp",EDGE,"E0.1"),sQuery(id+"F0.wireOp",EDGE,"E0.2"),sQuery(id+"F0.wireOp",EDGE,"E0.3"),sQuery(id+"F0.wireOp",EDGE,"E0.4"),sQuery(id+"F0.wireOp",EDGE,"E0.5"),sQuery(id+"F0.wireOp",EDGE,"E0.6"),sQuery(id+"F0.wireOp",EDGE,"E0.7"),sQuery(id+"F0.wireOp",EDGE,"E0.8"),sQuery(id+"F0.wireOp",EDGE,"E0.9"),sQuery(id+"F0.wireOp",EDGE,"E0.10"),sQuery(id+"F0.wireOp",EDGE,"E0.11"),sQuery(id+"F0.wireOp",EDGE,"E0.12"),sQuery(id+"F0.wireOp",EDGE,"E0.13"),sQuery(id+"F0.wireOp",EDGE,"E0.14"),sQuery(id+"F0.wireOp",EDGE,"E0.15"),sQuery(id+"F0.wireOp",EDGE,"E1"),sQuery(id+"F0.wireOp",EDGE,"E2.1"),sQuery(id+"F0.wireOp",EDGE,"E2.3"),sQuery(id+"F0.wireOp",EDGE,"E2.5"),sQuery(id+"F0.wireOp",EDGE,"E2.7"),sQuery(id+"F0.wireOp",EDGE,"E2.9"),sQuery(id+"F0.wireOp",EDGE,"E2.11"),sQuery(id+"F0.wireOp",EDGE,"E2.13"),sQuery(id+"F0.wireOp",EDGE,"E2.15"),sQuery(id+"F0.wireOp",EDGE,"E3.1"),sQuery(id+"F0.wireOp",EDGE,"E3.3"),sQuery(id+"F0.wireOp",EDGE,"E3.5"),sQuery(id+"F0.wireOp",EDGE,"E3.7"),sQuery(id+"F0.wireOp",EDGE,"E3.9"),sQuery(id+"F0.wireOp",EDGE,"E3.11"),subQ1,sQuery(id+"F0.wireOp",EDGE,"E3.15"),sQuery(id+"F0.wireOp",EDGE,"E4"),subQ0,sQuery(id+"F0.wireOp",EDGE,"E6"),sQuery(id+"F0.wireOp",EDGE,"E7"),sQuery(id+"F0.wireOp",EDGE,"E8"),sQuery(id+"F0.wireOp",EDGE,"E9"),sQuery(id+"F0.wireOp",EDGE,"E10"),sQuery(id+"F0.wireOp",EDGE,"E11"),sQuery(id+"F0.wireOp",EDGE,"E12"),sQuery(id+"F0.wireOp",EDGE,"E13"),sQuery(id+"F0.wireOp",EDGE,"E14"),sQuery(id+"F0.wireOp",EDGE,"E15"),sQuery(id+"F0.wireOp",EDGE,"E16"),sQuery(id+"F0.wireOp",EDGE,"E17"),sQuery(id+"F0.wireOp",EDGE,"E18"),sQuery(id+"F0.wireOp",EDGE,"E19")])],"isStart":true})]});}
            var Q10;
            Q10=makeQuery(id+"F1.opExtrude","CAP_EDGE",EDGE,{"disambiguationData":[OSD([sQuery(id+"F0.wireOp",EDGE,"E3.13")])],"isStart":true});
            var Q11;
            {var subQ0=sQuery(id+"F0.wireOp",EDGE,"E6");var subQ1=sQuery(id+"F0.wireOp",EDGE,"E3.13");Q11=makeQuery(id+"F5.opChamfer","BLEND_EDGE",EDGE,{"blendedFrom":[makeQuery(id+"F1.opExtrude","SWEPT_EDGE",EDGE,{"disambiguationData":[OSD([subQ1,sQuery(id+"F0.wireOp",EDGE,"E3.14"),subQ0])]}),makeQuery(id+"F1.opExtrude","CAP_FACE",FACE,{"disambiguationData":[OSD([sQuery(id+"F0.wireOp",EDGE,"E0.0"),sQuery(id+"F0.wireOp",EDGE,"E0.1"),sQuery(id+"F0.wireOp",EDGE,"E0.2"),sQuery(id+"F0.wireOp",EDGE,"E0.3"),sQuery(id+"F0.wireOp",EDGE,"E0.4"),sQuery(id+"F0.wireOp",EDGE,"E0.5"),sQuery(id+"F0.wireOp",EDGE,"E0.6"),sQuery(id+"F0.wireOp",EDGE,"E0.7"),sQuery(id+"F0.wireOp",EDGE,"E0.8"),sQuery(id+"F0.wireOp",EDGE,"E0.9"),sQuery(id+"F0.wireOp",EDGE,"E0.10"),sQuery(id+"F0.wireOp",EDGE,"E0.11"),sQuery(id+"F0.wireOp",EDGE,"E0.12"),sQuery(id+"F0.wireOp",EDGE,"E0.13"),sQuery(id+"F0.wireOp",EDGE,"E0.14"),sQuery(id+"F0.wireOp",EDGE,"E0.15"),sQuery(id+"F0.wireOp",EDGE,"E1"),sQuery(id+"F0.wireOp",EDGE,"E2.1"),sQuery(id+"F0.wireOp",EDGE,"E2.3"),sQuery(id+"F0.wireOp",EDGE,"E2.5"),sQuery(id+"F0.wireOp",EDGE,"E2.7"),sQuery(id+"F0.wireOp",EDGE,"E2.9"),sQuery(id+"F0.wireOp",EDGE,"E2.11"),sQuery(id+"F0.wireOp",EDGE,"E2.13"),sQuery(id+"F0.wireOp",EDGE,"E2.15"),sQuery(id+"F0.wireOp",EDGE,"E3.1"),sQuery(id+"F0.wireOp",EDGE,"E3.3"),sQuery(id+"F0.wireOp",EDGE,"E3.5"),sQuery(id+"F0.wireOp",EDGE,"E3.7"),sQuery(id+"F0.wireOp",EDGE,"E3.9"),sQuery(id+"F0.wireOp",EDGE,"E3.11"),subQ1,sQuery(id+"F0.wireOp",EDGE,"E3.15"),sQuery(id+"F0.wireOp",EDGE,"E4"),sQuery(id+"F0.wireOp",EDGE,"E5"),subQ0,sQuery(id+"F0.wireOp",EDGE,"E7"),sQuery(id+"F0.wireOp",EDGE,"E8"),sQuery(id+"F0.wireOp",EDGE,"E9"),sQuery(id+"F0.wireOp",EDGE,"E10"),sQuery(id+"F0.wireOp",EDGE,"E11"),sQuery(id+"F0.wireOp",EDGE,"E12"),sQuery(id+"F0.wireOp",EDGE,"E13"),sQuery(id+"F0.wireOp",EDGE,"E14"),sQuery(id+"F0.wireOp",EDGE,"E15"),sQuery(id+"F0.wireOp",EDGE,"E16"),sQuery(id+"F0.wireOp",EDGE,"E17"),sQuery(id+"F0.wireOp",EDGE,"E18"),sQuery(id+"F0.wireOp",EDGE,"E19")])],"isStart":true})],"blendedInto":[makeQuery(id+"F1.opExtrude","CAP_FACE",FACE,{"disambiguationData":[OSD([sQuery(id+"F0.wireOp",EDGE,"E0.0"),sQuery(id+"F0.wireOp",EDGE,"E0.1"),sQuery(id+"F0.wireOp",EDGE,"E0.2"),sQuery(id+"F0.wireOp",EDGE,"E0.3"),sQuery(id+"F0.wireOp",EDGE,"E0.4"),sQuery(id+"F0.wireOp",EDGE,"E0.5"),sQuery(id+"F0.wireOp",EDGE,"E0.6"),sQuery(id+"F0.wireOp",EDGE,"E0.7"),sQuery(id+"F0.wireOp",EDGE,"E0.8"),sQuery(id+"F0.wireOp",EDGE,"E0.9"),sQuery(id+"F0.wireOp",EDGE,"E0.10"),sQuery(id+"F0.wireOp",EDGE,"E0.11"),sQuery(id+"F0.wireOp",EDGE,"E0.12"),sQuery(id+"F0.wireOp",EDGE,"E0.13"),sQuery(id+"F0.wireOp",EDGE,"E0.14"),sQuery(id+"F0.wireOp",EDGE,"E0.15"),sQuery(id+"F0.wireOp",EDGE,"E1"),sQuery(id+"F0.wireOp",EDGE,"E2.1"),sQuery(id+"F0.wireOp",EDGE,"E2.3"),sQuery(id+"F0.wireOp",EDGE,"E2.5"),sQuery(id+"F0.wireOp",EDGE,"E2.7"),sQuery(id+"F0.wireOp",EDGE,"E2.9"),sQuery(id+"F0.wireOp",EDGE,"E2.11"),sQuery(id+"F0.wireOp",EDGE,"E2.13"),sQuery(id+"F0.wireOp",EDGE,"E2.15"),sQuery(id+"F0.wireOp",EDGE,"E3.1"),sQuery(id+"F0.wireOp",EDGE,"E3.3"),sQuery(id+"F0.wireOp",EDGE,"E3.5"),sQuery(id+"F0.wireOp",EDGE,"E3.7"),sQuery(id+"F0.wireOp",EDGE,"E3.9"),sQuery(id+"F0.wireOp",EDGE,"E3.11"),subQ1,sQuery(id+"F0.wireOp",EDGE,"E3.15"),sQuery(id+"F0.wireOp",EDGE,"E4"),sQuery(id+"F0.wireOp",EDGE,"E5"),subQ0,sQuery(id+"F0.wireOp",EDGE,"E7"),sQuery(id+"F0.wireOp",EDGE,"E8"),sQuery(id+"F0.wireOp",EDGE,"E9"),sQuery(id+"F0.wireOp",EDGE,"E10"),sQuery(id+"F0.wireOp",EDGE,"E11"),sQuery(id+"F0.wireOp",EDGE,"E12"),sQuery(id+"F0.wireOp",EDGE,"E13"),sQuery(id+"F0.wireOp",EDGE,"E14"),sQuery(id+"F0.wireOp",EDGE,"E15"),sQuery(id+"F0.wireOp",EDGE,"E16"),sQuery(id+"F0.wireOp",EDGE,"E17"),sQuery(id+"F0.wireOp",EDGE,"E18"),sQuery(id+"F0.wireOp",EDGE,"E19")])],"isStart":true})]});}
            var Q12;
            Q12=makeQuery(id+"F1.opExtrude","CAP_EDGE",EDGE,{"disambiguationData":[OSD([sQuery(id+"F0.wireOp",EDGE,"E6")])],"isStart":true});
            var Q13;
            {var subQ0=sQuery(id+"F0.wireOp",EDGE,"E6");var subQ1=sQuery(id+"F0.wireOp",EDGE,"E2.13");Q13=makeQuery(id+"F5.opChamfer","BLEND_EDGE",EDGE,{"blendedFrom":[makeQuery(id+"F1.opExtrude","SWEPT_EDGE",EDGE,{"disambiguationData":[OSD([subQ1,sQuery(id+"F0.wireOp",EDGE,"E2.14"),subQ0])]}),makeQuery(id+"F1.opExtrude","CAP_FACE",FACE,{"disambiguationData":[OSD([sQuery(id+"F0.wireOp",EDGE,"E0.0"),sQuery(id+"F0.wireOp",EDGE,"E0.1"),sQuery(id+"F0.wireOp",EDGE,"E0.2"),sQuery(id+"F0.wireOp",EDGE,"E0.3"),sQuery(id+"F0.wireOp",EDGE,"E0.4"),sQuery(id+"F0.wireOp",EDGE,"E0.5"),sQuery(id+"F0.wireOp",EDGE,"E0.6"),sQuery(id+"F0.wireOp",EDGE,"E0.7"),sQuery(id+"F0.wireOp",EDGE,"E0.8"),sQuery(id+"F0.wireOp",EDGE,"E0.9"),sQuery(id+"F0.wireOp",EDGE,"E0.10"),sQuery(id+"F0.wireOp",EDGE,"E0.11"),sQuery(id+"F0.wireOp",EDGE,"E0.12"),sQuery(id+"F0.wireOp",EDGE,"E0.13"),sQuery(id+"F0.wireOp",EDGE,"E0.14"),sQuery(id+"F0.wireOp",EDGE,"E0.15"),sQuery(id+"F0.wireOp",EDGE,"E1"),sQuery(id+"F0.wireOp",EDGE,"E2.1"),sQuery(id+"F0.wireOp",EDGE,"E2.3"),sQuery(id+"F0.wireOp",EDGE,"E2.5"),sQuery(id+"F0.wireOp",EDGE,"E2.7"),sQuery(id+"F0.wireOp",EDGE,"E2.9"),sQuery(id+"F0.wireOp",EDGE,"E2.11"),subQ1,sQuery(id+"F0.wireOp",EDGE,"E2.15"),sQuery(id+"F0.wireOp",EDGE,"E3.1"),sQuery(id+"F0.wireOp",EDGE,"E3.3"),sQuery(id+"F0.wireOp",EDGE,"E3.5"),sQuery(id+"F0.wireOp",EDGE,"E3.7"),sQuery(id+"F0.wireOp",EDGE,"E3.9"),sQuery(id+"F0.wireOp",EDGE,"E3.11"),sQuery(id+"F0.wireOp",EDGE,"E3.13"),sQuery(id+"F0.wireOp",EDGE,"E3.15"),sQuery(id+"F0.wireOp",EDGE,"E4"),sQuery(id+"F0.wireOp",EDGE,"E5"),subQ0,sQuery(id+"F0.wireOp",EDGE,"E7"),sQuery(id+"F0.wireOp",EDGE,"E8"),sQuery(id+"F0.wireOp",EDGE,"E9"),sQuery(id+"F0.wireOp",EDGE,"E10"),sQuery(id+"F0.wireOp",EDGE,"E11"),sQuery(id+"F0.wireOp",EDGE,"E12"),sQuery(id+"F0.wireOp",EDGE,"E13"),sQuery(id+"F0.wireOp",EDGE,"E14"),sQuery(id+"F0.wireOp",EDGE,"E15"),sQuery(id+"F0.wireOp",EDGE,"E16"),sQuery(id+"F0.wireOp",EDGE,"E17"),sQuery(id+"F0.wireOp",EDGE,"E18"),sQuery(id+"F0.wireOp",EDGE,"E19")])],"isStart":true})],"blendedInto":[makeQuery(id+"F1.opExtrude","CAP_FACE",FACE,{"disambiguationData":[OSD([sQuery(id+"F0.wireOp",EDGE,"E0.0"),sQuery(id+"F0.wireOp",EDGE,"E0.1"),sQuery(id+"F0.wireOp",EDGE,"E0.2"),sQuery(id+"F0.wireOp",EDGE,"E0.3"),sQuery(id+"F0.wireOp",EDGE,"E0.4"),sQuery(id+"F0.wireOp",EDGE,"E0.5"),sQuery(id+"F0.wireOp",EDGE,"E0.6"),sQuery(id+"F0.wireOp",EDGE,"E0.7"),sQuery(id+"F0.wireOp",EDGE,"E0.8"),sQuery(id+"F0.wireOp",EDGE,"E0.9"),sQuery(id+"F0.wireOp",EDGE,"E0.10"),sQuery(id+"F0.wireOp",EDGE,"E0.11"),sQuery(id+"F0.wireOp",EDGE,"E0.12"),sQuery(id+"F0.wireOp",EDGE,"E0.13"),sQuery(id+"F0.wireOp",EDGE,"E0.14"),sQuery(id+"F0.wireOp",EDGE,"E0.15"),sQuery(id+"F0.wireOp",EDGE,"E1"),sQuery(id+"F0.wireOp",EDGE,"E2.1"),sQuery(id+"F0.wireOp",EDGE,"E2.3"),sQuery(id+"F0.wireOp",EDGE,"E2.5"),sQuery(id+"F0.wireOp",EDGE,"E2.7"),sQuery(id+"F0.wireOp",EDGE,"E2.9"),sQuery(id+"F0.wireOp",EDGE,"E2.11"),subQ1,sQuery(id+"F0.wireOp",EDGE,"E2.15"),sQuery(id+"F0.wireOp",EDGE,"E3.1"),sQuery(id+"F0.wireOp",EDGE,"E3.3"),sQuery(id+"F0.wireOp",EDGE,"E3.5"),sQuery(id+"F0.wireOp",EDGE,"E3.7"),sQuery(id+"F0.wireOp",EDGE,"E3.9"),sQuery(id+"F0.wireOp",EDGE,"E3.11"),sQuery(id+"F0.wireOp",EDGE,"E3.13"),sQuery(id+"F0.wireOp",EDGE,"E3.15"),sQuery(id+"F0.wireOp",EDGE,"E4"),sQuery(id+"F0.wireOp",EDGE,"E5"),subQ0,sQuery(id+"F0.wireOp",EDGE,"E7"),sQuery(id+"F0.wireOp",EDGE,"E8"),sQuery(id+"F0.wireOp",EDGE,"E9"),sQuery(id+"F0.wireOp",EDGE,"E10"),sQuery(id+"F0.wireOp",EDGE,"E11"),sQuery(id+"F0.wireOp",EDGE,"E12"),sQuery(id+"F0.wireOp",EDGE,"E13"),sQuery(id+"F0.wireOp",EDGE,"E14"),sQuery(id+"F0.wireOp",EDGE,"E15"),sQuery(id+"F0.wireOp",EDGE,"E16"),sQuery(id+"F0.wireOp",EDGE,"E17"),sQuery(id+"F0.wireOp",EDGE,"E18"),sQuery(id+"F0.wireOp",EDGE,"E19")])],"isStart":true})]});}
            var Q14;
            Q14=makeQuery(id+"F1.opExtrude","CAP_EDGE",EDGE,{"disambiguationData":[OSD([sQuery(id+"F0.wireOp",EDGE,"E2.13")])],"isStart":true});
            var Q15;
            {var subQ0=sQuery(id+"F0.wireOp",EDGE,"E5");var subQ1=sQuery(id+"F0.wireOp",EDGE,"E2.13");Q15=makeQuery(id+"F5.opChamfer","BLEND_EDGE",EDGE,{"blendedFrom":[makeQuery(id+"F1.opExtrude","SWEPT_EDGE",EDGE,{"disambiguationData":[OSD([sQuery(id+"F0.wireOp",EDGE,"E2.12"),subQ1,subQ0])]}),makeQuery(id+"F1.opExtrude","CAP_FACE",FACE,{"disambiguationData":[OSD([sQuery(id+"F0.wireOp",EDGE,"E0.0"),sQuery(id+"F0.wireOp",EDGE,"E0.1"),sQuery(id+"F0.wireOp",EDGE,"E0.2"),sQuery(id+"F0.wireOp",EDGE,"E0.3"),sQuery(id+"F0.wireOp",EDGE,"E0.4"),sQuery(id+"F0.wireOp",EDGE,"E0.5"),sQuery(id+"F0.wireOp",EDGE,"E0.6"),sQuery(id+"F0.wireOp",EDGE,"E0.7"),sQuery(id+"F0.wireOp",EDGE,"E0.8"),sQuery(id+"F0.wireOp",EDGE,"E0.9"),sQuery(id+"F0.wireOp",EDGE,"E0.10"),sQuery(id+"F0.wireOp",EDGE,"E0.11"),sQuery(id+"F0.wireOp",EDGE,"E0.12"),sQuery(id+"F0.wireOp",EDGE,"E0.13"),sQuery(id+"F0.wireOp",EDGE,"E0.14"),sQuery(id+"F0.wireOp",EDGE,"E0.15"),sQuery(id+"F0.wireOp",EDGE,"E1"),sQuery(id+"F0.wireOp",EDGE,"E2.1"),sQuery(id+"F0.wireOp",EDGE,"E2.3"),sQuery(id+"F0.wireOp",EDGE,"E2.5"),sQuery(id+"F0.wireOp",EDGE,"E2.7"),sQuery(id+"F0.wireOp",EDGE,"E2.9"),sQuery(id+"F0.wireOp",EDGE,"E2.11"),subQ1,sQuery(id+"F0.wireOp",EDGE,"E2.15"),sQuery(id+"F0.wireOp",EDGE,"E3.1"),sQuery(id+"F0.wireOp",EDGE,"E3.3"),sQuery(id+"F0.wireOp",EDGE,"E3.5"),sQuery(id+"F0.wireOp",EDGE,"E3.7"),sQuery(id+"F0.wireOp",EDGE,"E3.9"),sQuery(id+"F0.wireOp",EDGE,"E3.11"),sQuery(id+"F0.wireOp",EDGE,"E3.13"),sQuery(id+"F0.wireOp",EDGE,"E3.15"),sQuery(id+"F0.wireOp",EDGE,"E4"),subQ0,sQuery(id+"F0.wireOp",EDGE,"E6"),sQuery(id+"F0.wireOp",EDGE,"E7"),sQuery(id+"F0.wireOp",EDGE,"E8"),sQuery(id+"F0.wireOp",EDGE,"E9"),sQuery(id+"F0.wireOp",EDGE,"E10"),sQuery(id+"F0.wireOp",EDGE,"E11"),sQuery(id+"F0.wireOp",EDGE,"E12"),sQuery(id+"F0.wireOp",EDGE,"E13"),sQuery(id+"F0.wireOp",EDGE,"E14"),sQuery(id+"F0.wireOp",EDGE,"E15"),sQuery(id+"F0.wireOp",EDGE,"E16"),sQuery(id+"F0.wireOp",EDGE,"E17"),sQuery(id+"F0.wireOp",EDGE,"E18"),sQuery(id+"F0.wireOp",EDGE,"E19")])],"isStart":true})],"blendedInto":[makeQuery(id+"F1.opExtrude","CAP_FACE",FACE,{"disambiguationData":[OSD([sQuery(id+"F0.wireOp",EDGE,"E0.0"),sQuery(id+"F0.wireOp",EDGE,"E0.1"),sQuery(id+"F0.wireOp",EDGE,"E0.2"),sQuery(id+"F0.wireOp",EDGE,"E0.3"),sQuery(id+"F0.wireOp",EDGE,"E0.4"),sQuery(id+"F0.wireOp",EDGE,"E0.5"),sQuery(id+"F0.wireOp",EDGE,"E0.6"),sQuery(id+"F0.wireOp",EDGE,"E0.7"),sQuery(id+"F0.wireOp",EDGE,"E0.8"),sQuery(id+"F0.wireOp",EDGE,"E0.9"),sQuery(id+"F0.wireOp",EDGE,"E0.10"),sQuery(id+"F0.wireOp",EDGE,"E0.11"),sQuery(id+"F0.wireOp",EDGE,"E0.12"),sQuery(id+"F0.wireOp",EDGE,"E0.13"),sQuery(id+"F0.wireOp",EDGE,"E0.14"),sQuery(id+"F0.wireOp",EDGE,"E0.15"),sQuery(id+"F0.wireOp",EDGE,"E1"),sQuery(id+"F0.wireOp",EDGE,"E2.1"),sQuery(id+"F0.wireOp",EDGE,"E2.3"),sQuery(id+"F0.wireOp",EDGE,"E2.5"),sQuery(id+"F0.wireOp",EDGE,"E2.7"),sQuery(id+"F0.wireOp",EDGE,"E2.9"),sQuery(id+"F0.wireOp",EDGE,"E2.11"),subQ1,sQuery(id+"F0.wireOp",EDGE,"E2.15"),sQuery(id+"F0.wireOp",EDGE,"E3.1"),sQuery(id+"F0.wireOp",EDGE,"E3.3"),sQuery(id+"F0.wireOp",EDGE,"E3.5"),sQuery(id+"F0.wireOp",EDGE,"E3.7"),sQuery(id+"F0.wireOp",EDGE,"E3.9"),sQuery(id+"F0.wireOp",EDGE,"E3.11"),sQuery(id+"F0.wireOp",EDGE,"E3.13"),sQuery(id+"F0.wireOp",EDGE,"E3.15"),sQuery(id+"F0.wireOp",EDGE,"E4"),subQ0,sQuery(id+"F0.wireOp",EDGE,"E6"),sQuery(id+"F0.wireOp",EDGE,"E7"),sQuery(id+"F0.wireOp",EDGE,"E8"),sQuery(id+"F0.wireOp",EDGE,"E9"),sQuery(id+"F0.wireOp",EDGE,"E10"),sQuery(id+"F0.wireOp",EDGE,"E11"),sQuery(id+"F0.wireOp",EDGE,"E12"),sQuery(id+"F0.wireOp",EDGE,"E13"),sQuery(id+"F0.wireOp",EDGE,"E14"),sQuery(id+"F0.wireOp",EDGE,"E15"),sQuery(id+"F0.wireOp",EDGE,"E16"),sQuery(id+"F0.wireOp",EDGE,"E17"),sQuery(id+"F0.wireOp",EDGE,"E18"),sQuery(id+"F0.wireOp",EDGE,"E19")])],"isStart":true})]});}
            var Q16;
            Q16=makeQuery(id+"F1.opExtrude","CAP_EDGE",EDGE,{"disambiguationData":[OSD([sQuery(id+"F0.wireOp",EDGE,"E18")])],"isStart":true});
            var Q17;
            {var subQ0=sQuery(id+"F0.wireOp",EDGE,"E18");var subQ1=sQuery(id+"F0.wireOp",EDGE,"E2.9");Q17=makeQuery(id+"F5.opChamfer","BLEND_EDGE",EDGE,{"blendedFrom":[makeQuery(id+"F1.opExtrude","SWEPT_EDGE",EDGE,{"disambiguationData":[OSD([subQ1,sQuery(id+"F0.wireOp",EDGE,"E2.10"),subQ0])]}),makeQuery(id+"F1.opExtrude","CAP_FACE",FACE,{"disambiguationData":[OSD([sQuery(id+"F0.wireOp",EDGE,"E0.0"),sQuery(id+"F0.wireOp",EDGE,"E0.1"),sQuery(id+"F0.wireOp",EDGE,"E0.2"),sQuery(id+"F0.wireOp",EDGE,"E0.3"),sQuery(id+"F0.wireOp",EDGE,"E0.4"),sQuery(id+"F0.wireOp",EDGE,"E0.5"),sQuery(id+"F0.wireOp",EDGE,"E0.6"),sQuery(id+"F0.wireOp",EDGE,"E0.7"),sQuery(id+"F0.wireOp",EDGE,"E0.8"),sQuery(id+"F0.wireOp",EDGE,"E0.9"),sQuery(id+"F0.wireOp",EDGE,"E0.10"),sQuery(id+"F0.wireOp",EDGE,"E0.11"),sQuery(id+"F0.wireOp",EDGE,"E0.12"),sQuery(id+"F0.wireOp",EDGE,"E0.13"),sQuery(id+"F0.wireOp",EDGE,"E0.14"),sQuery(id+"F0.wireOp",EDGE,"E0.15"),sQuery(id+"F0.wireOp",EDGE,"E1"),sQuery(id+"F0.wireOp",EDGE,"E2.1"),sQuery(id+"F0.wireOp",EDGE,"E2.3"),sQuery(id+"F0.wireOp",EDGE,"E2.5"),sQuery(id+"F0.wireOp",EDGE,"E2.7"),subQ1,sQuery(id+"F0.wireOp",EDGE,"E2.11"),sQuery(id+"F0.wireOp",EDGE,"E2.13"),sQuery(id+"F0.wireOp",EDGE,"E2.15"),sQuery(id+"F0.wireOp",EDGE,"E3.1"),sQuery(id+"F0.wireOp",EDGE,"E3.3"),sQuery(id+"F0.wireOp",EDGE,"E3.5"),sQuery(id+"F0.wireOp",EDGE,"E3.7"),sQuery(id+"F0.wireOp",EDGE,"E3.9"),sQuery(id+"F0.wireOp",EDGE,"E3.11"),sQuery(id+"F0.wireOp",EDGE,"E3.13"),sQuery(id+"F0.wireOp",EDGE,"E3.15"),sQuery(id+"F0.wireOp",EDGE,"E4"),sQuery(id+"F0.wireOp",EDGE,"E5"),sQuery(id+"F0.wireOp",EDGE,"E6"),sQuery(id+"F0.wireOp",EDGE,"E7"),sQuery(id+"F0.wireOp",EDGE,"E8"),sQuery(id+"F0.wireOp",EDGE,"E9"),sQuery(id+"F0.wireOp",EDGE,"E10"),sQuery(id+"F0.wireOp",EDGE,"E11"),sQuery(id+"F0.wireOp",EDGE,"E12"),sQuery(id+"F0.wireOp",EDGE,"E13"),sQuery(id+"F0.wireOp",EDGE,"E14"),sQuery(id+"F0.wireOp",EDGE,"E15"),sQuery(id+"F0.wireOp",EDGE,"E16"),sQuery(id+"F0.wireOp",EDGE,"E17"),subQ0,sQuery(id+"F0.wireOp",EDGE,"E19")])],"isStart":true})],"blendedInto":[makeQuery(id+"F1.opExtrude","CAP_FACE",FACE,{"disambiguationData":[OSD([sQuery(id+"F0.wireOp",EDGE,"E0.0"),sQuery(id+"F0.wireOp",EDGE,"E0.1"),sQuery(id+"F0.wireOp",EDGE,"E0.2"),sQuery(id+"F0.wireOp",EDGE,"E0.3"),sQuery(id+"F0.wireOp",EDGE,"E0.4"),sQuery(id+"F0.wireOp",EDGE,"E0.5"),sQuery(id+"F0.wireOp",EDGE,"E0.6"),sQuery(id+"F0.wireOp",EDGE,"E0.7"),sQuery(id+"F0.wireOp",EDGE,"E0.8"),sQuery(id+"F0.wireOp",EDGE,"E0.9"),sQuery(id+"F0.wireOp",EDGE,"E0.10"),sQuery(id+"F0.wireOp",EDGE,"E0.11"),sQuery(id+"F0.wireOp",EDGE,"E0.12"),sQuery(id+"F0.wireOp",EDGE,"E0.13"),sQuery(id+"F0.wireOp",EDGE,"E0.14"),sQuery(id+"F0.wireOp",EDGE,"E0.15"),sQuery(id+"F0.wireOp",EDGE,"E1"),sQuery(id+"F0.wireOp",EDGE,"E2.1"),sQuery(id+"F0.wireOp",EDGE,"E2.3"),sQuery(id+"F0.wireOp",EDGE,"E2.5"),sQuery(id+"F0.wireOp",EDGE,"E2.7"),subQ1,sQuery(id+"F0.wireOp",EDGE,"E2.11"),sQuery(id+"F0.wireOp",EDGE,"E2.13"),sQuery(id+"F0.wireOp",EDGE,"E2.15"),sQuery(id+"F0.wireOp",EDGE,"E3.1"),sQuery(id+"F0.wireOp",EDGE,"E3.3"),sQuery(id+"F0.wireOp",EDGE,"E3.5"),sQuery(id+"F0.wireOp",EDGE,"E3.7"),sQuery(id+"F0.wireOp",EDGE,"E3.9"),sQuery(id+"F0.wireOp",EDGE,"E3.11"),sQuery(id+"F0.wireOp",EDGE,"E3.13"),sQuery(id+"F0.wireOp",EDGE,"E3.15"),sQuery(id+"F0.wireOp",EDGE,"E4"),sQuery(id+"F0.wireOp",EDGE,"E5"),sQuery(id+"F0.wireOp",EDGE,"E6"),sQuery(id+"F0.wireOp",EDGE,"E7"),sQuery(id+"F0.wireOp",EDGE,"E8"),sQuery(id+"F0.wireOp",EDGE,"E9"),sQuery(id+"F0.wireOp",EDGE,"E10"),sQuery(id+"F0.wireOp",EDGE,"E11"),sQuery(id+"F0.wireOp",EDGE,"E12"),sQuery(id+"F0.wireOp",EDGE,"E13"),sQuery(id+"F0.wireOp",EDGE,"E14"),sQuery(id+"F0.wireOp",EDGE,"E15"),sQuery(id+"F0.wireOp",EDGE,"E16"),sQuery(id+"F0.wireOp",EDGE,"E17"),subQ0,sQuery(id+"F0.wireOp",EDGE,"E19")])],"isStart":true})]});}
            var Q18;
            Q18=makeQuery(id+"F1.opExtrude","CAP_EDGE",EDGE,{"disambiguationData":[OSD([sQuery(id+"F0.wireOp",EDGE,"E2.9")])],"isStart":true});
            var Q19;
            {var subQ0=sQuery(id+"F0.wireOp",EDGE,"E18");var subQ1=sQuery(id+"F0.wireOp",EDGE,"E3.9");Q19=makeQuery(id+"F5.opChamfer","BLEND_EDGE",EDGE,{"blendedFrom":[makeQuery(id+"F1.opExtrude","SWEPT_EDGE",EDGE,{"disambiguationData":[OSD([subQ1,sQuery(id+"F0.wireOp",EDGE,"E3.10"),subQ0])]}),makeQuery(id+"F1.opExtrude","CAP_FACE",FACE,{"disambiguationData":[OSD([sQuery(id+"F0.wireOp",EDGE,"E0.0"),sQuery(id+"F0.wireOp",EDGE,"E0.1"),sQuery(id+"F0.wireOp",EDGE,"E0.2"),sQuery(id+"F0.wireOp",EDGE,"E0.3"),sQuery(id+"F0.wireOp",EDGE,"E0.4"),sQuery(id+"F0.wireOp",EDGE,"E0.5"),sQuery(id+"F0.wireOp",EDGE,"E0.6"),sQuery(id+"F0.wireOp",EDGE,"E0.7"),sQuery(id+"F0.wireOp",EDGE,"E0.8"),sQuery(id+"F0.wireOp",EDGE,"E0.9"),sQuery(id+"F0.wireOp",EDGE,"E0.10"),sQuery(id+"F0.wireOp",EDGE,"E0.11"),sQuery(id+"F0.wireOp",EDGE,"E0.12"),sQuery(id+"F0.wireOp",EDGE,"E0.13"),sQuery(id+"F0.wireOp",EDGE,"E0.14"),sQuery(id+"F0.wireOp",EDGE,"E0.15"),sQuery(id+"F0.wireOp",EDGE,"E1"),sQuery(id+"F0.wireOp",EDGE,"E2.1"),sQuery(id+"F0.wireOp",EDGE,"E2.3"),sQuery(id+"F0.wireOp",EDGE,"E2.5"),sQuery(id+"F0.wireOp",EDGE,"E2.7"),sQuery(id+"F0.wireOp",EDGE,"E2.9"),sQuery(id+"F0.wireOp",EDGE,"E2.11"),sQuery(id+"F0.wireOp",EDGE,"E2.13"),sQuery(id+"F0.wireOp",EDGE,"E2.15"),sQuery(id+"F0.wireOp",EDGE,"E3.1"),sQuery(id+"F0.wireOp",EDGE,"E3.3"),sQuery(id+"F0.wireOp",EDGE,"E3.5"),sQuery(id+"F0.wireOp",EDGE,"E3.7"),subQ1,sQuery(id+"F0.wireOp",EDGE,"E3.11"),sQuery(id+"F0.wireOp",EDGE,"E3.13"),sQuery(id+"F0.wireOp",EDGE,"E3.15"),sQuery(id+"F0.wireOp",EDGE,"E4"),sQuery(id+"F0.wireOp",EDGE,"E5"),sQuery(id+"F0.wireOp",EDGE,"E6"),sQuery(id+"F0.wireOp",EDGE,"E7"),sQuery(id+"F0.wireOp",EDGE,"E8"),sQuery(id+"F0.wireOp",EDGE,"E9"),sQuery(id+"F0.wireOp",EDGE,"E10"),sQuery(id+"F0.wireOp",EDGE,"E11"),sQuery(id+"F0.wireOp",EDGE,"E12"),sQuery(id+"F0.wireOp",EDGE,"E13"),sQuery(id+"F0.wireOp",EDGE,"E14"),sQuery(id+"F0.wireOp",EDGE,"E15"),sQuery(id+"F0.wireOp",EDGE,"E16"),sQuery(id+"F0.wireOp",EDGE,"E17"),subQ0,sQuery(id+"F0.wireOp",EDGE,"E19")])],"isStart":true})],"blendedInto":[makeQuery(id+"F1.opExtrude","CAP_FACE",FACE,{"disambiguationData":[OSD([sQuery(id+"F0.wireOp",EDGE,"E0.0"),sQuery(id+"F0.wireOp",EDGE,"E0.1"),sQuery(id+"F0.wireOp",EDGE,"E0.2"),sQuery(id+"F0.wireOp",EDGE,"E0.3"),sQuery(id+"F0.wireOp",EDGE,"E0.4"),sQuery(id+"F0.wireOp",EDGE,"E0.5"),sQuery(id+"F0.wireOp",EDGE,"E0.6"),sQuery(id+"F0.wireOp",EDGE,"E0.7"),sQuery(id+"F0.wireOp",EDGE,"E0.8"),sQuery(id+"F0.wireOp",EDGE,"E0.9"),sQuery(id+"F0.wireOp",EDGE,"E0.10"),sQuery(id+"F0.wireOp",EDGE,"E0.11"),sQuery(id+"F0.wireOp",EDGE,"E0.12"),sQuery(id+"F0.wireOp",EDGE,"E0.13"),sQuery(id+"F0.wireOp",EDGE,"E0.14"),sQuery(id+"F0.wireOp",EDGE,"E0.15"),sQuery(id+"F0.wireOp",EDGE,"E1"),sQuery(id+"F0.wireOp",EDGE,"E2.1"),sQuery(id+"F0.wireOp",EDGE,"E2.3"),sQuery(id+"F0.wireOp",EDGE,"E2.5"),sQuery(id+"F0.wireOp",EDGE,"E2.7"),sQuery(id+"F0.wireOp",EDGE,"E2.9"),sQuery(id+"F0.wireOp",EDGE,"E2.11"),sQuery(id+"F0.wireOp",EDGE,"E2.13"),sQuery(id+"F0.wireOp",EDGE,"E2.15"),sQuery(id+"F0.wireOp",EDGE,"E3.1"),sQuery(id+"F0.wireOp",EDGE,"E3.3"),sQuery(id+"F0.wireOp",EDGE,"E3.5"),sQuery(id+"F0.wireOp",EDGE,"E3.7"),subQ1,sQuery(id+"F0.wireOp",EDGE,"E3.11"),sQuery(id+"F0.wireOp",EDGE,"E3.13"),sQuery(id+"F0.wireOp",EDGE,"E3.15"),sQuery(id+"F0.wireOp",EDGE,"E4"),sQuery(id+"F0.wireOp",EDGE,"E5"),sQuery(id+"F0.wireOp",EDGE,"E6"),sQuery(id+"F0.wireOp",EDGE,"E7"),sQuery(id+"F0.wireOp",EDGE,"E8"),sQuery(id+"F0.wireOp",EDGE,"E9"),sQuery(id+"F0.wireOp",EDGE,"E10"),sQuery(id+"F0.wireOp",EDGE,"E11"),sQuery(id+"F0.wireOp",EDGE,"E12"),sQuery(id+"F0.wireOp",EDGE,"E13"),sQuery(id+"F0.wireOp",EDGE,"E14"),sQuery(id+"F0.wireOp",EDGE,"E15"),sQuery(id+"F0.wireOp",EDGE,"E16"),sQuery(id+"F0.wireOp",EDGE,"E17"),subQ0,sQuery(id+"F0.wireOp",EDGE,"E19")])],"isStart":true})]});}
            var Q20;
            Q20=makeQuery(id+"F1.opExtrude","CAP_EDGE",EDGE,{"disambiguationData":[OSD([sQuery(id+"F0.wireOp",EDGE,"E3.9")])],"isStart":true});
            var Q21;
            Q21=makeQuery(id+"F1.opExtrude","CAP_EDGE",EDGE,{"disambiguationData":[OSD([sQuery(id+"F0.wireOp",EDGE,"E17")])],"isStart":true});
            var Q22;
            {var subQ0=sQuery(id+"F0.wireOp",EDGE,"E17");var subQ1=sQuery(id+"F0.wireOp",EDGE,"E2.9");Q22=makeQuery(id+"F5.opChamfer","BLEND_EDGE",EDGE,{"blendedFrom":[makeQuery(id+"F1.opExtrude","SWEPT_EDGE",EDGE,{"disambiguationData":[OSD([sQuery(id+"F0.wireOp",EDGE,"E2.8"),subQ1,subQ0])]}),makeQuery(id+"F1.opExtrude","CAP_FACE",FACE,{"disambiguationData":[OSD([sQuery(id+"F0.wireOp",EDGE,"E0.0"),sQuery(id+"F0.wireOp",EDGE,"E0.1"),sQuery(id+"F0.wireOp",EDGE,"E0.2"),sQuery(id+"F0.wireOp",EDGE,"E0.3"),sQuery(id+"F0.wireOp",EDGE,"E0.4"),sQuery(id+"F0.wireOp",EDGE,"E0.5"),sQuery(id+"F0.wireOp",EDGE,"E0.6"),sQuery(id+"F0.wireOp",EDGE,"E0.7"),sQuery(id+"F0.wireOp",EDGE,"E0.8"),sQuery(id+"F0.wireOp",EDGE,"E0.9"),sQuery(id+"F0.wireOp",EDGE,"E0.10"),sQuery(id+"F0.wireOp",EDGE,"E0.11"),sQuery(id+"F0.wireOp",EDGE,"E0.12"),sQuery(id+"F0.wireOp",EDGE,"E0.13"),sQuery(id+"F0.wireOp",EDGE,"E0.14"),sQuery(id+"F0.wireOp",EDGE,"E0.15"),sQuery(id+"F0.wireOp",EDGE,"E1"),sQuery(id+"F0.wireOp",EDGE,"E2.1"),sQuery(id+"F0.wireOp",EDGE,"E2.3"),sQuery(id+"F0.wireOp",EDGE,"E2.5"),sQuery(id+"F0.wireOp",EDGE,"E2.7"),subQ1,sQuery(id+"F0.wireOp",EDGE,"E2.11"),sQuery(id+"F0.wireOp",EDGE,"E2.13"),sQuery(id+"F0.wireOp",EDGE,"E2.15"),sQuery(id+"F0.wireOp",EDGE,"E3.1"),sQuery(id+"F0.wireOp",EDGE,"E3.3"),sQuery(id+"F0.wireOp",EDGE,"E3.5"),sQuery(id+"F0.wireOp",EDGE,"E3.7"),sQuery(id+"F0.wireOp",EDGE,"E3.9"),sQuery(id+"F0.wireOp",EDGE,"E3.11"),sQuery(id+"F0.wireOp",EDGE,"E3.13"),sQuery(id+"F0.wireOp",EDGE,"E3.15"),sQuery(id+"F0.wireOp",EDGE,"E4"),sQuery(id+"F0.wireOp",EDGE,"E5"),sQuery(id+"F0.wireOp",EDGE,"E6"),sQuery(id+"F0.wireOp",EDGE,"E7"),sQuery(id+"F0.wireOp",EDGE,"E8"),sQuery(id+"F0.wireOp",EDGE,"E9"),sQuery(id+"F0.wireOp",EDGE,"E10"),sQuery(id+"F0.wireOp",EDGE,"E11"),sQuery(id+"F0.wireOp",EDGE,"E12"),sQuery(id+"F0.wireOp",EDGE,"E13"),sQuery(id+"F0.wireOp",EDGE,"E14"),sQuery(id+"F0.wireOp",EDGE,"E15"),sQuery(id+"F0.wireOp",EDGE,"E16"),subQ0,sQuery(id+"F0.wireOp",EDGE,"E18"),sQuery(id+"F0.wireOp",EDGE,"E19")])],"isStart":true})],"blendedInto":[makeQuery(id+"F1.opExtrude","CAP_FACE",FACE,{"disambiguationData":[OSD([sQuery(id+"F0.wireOp",EDGE,"E0.0"),sQuery(id+"F0.wireOp",EDGE,"E0.1"),sQuery(id+"F0.wireOp",EDGE,"E0.2"),sQuery(id+"F0.wireOp",EDGE,"E0.3"),sQuery(id+"F0.wireOp",EDGE,"E0.4"),sQuery(id+"F0.wireOp",EDGE,"E0.5"),sQuery(id+"F0.wireOp",EDGE,"E0.6"),sQuery(id+"F0.wireOp",EDGE,"E0.7"),sQuery(id+"F0.wireOp",EDGE,"E0.8"),sQuery(id+"F0.wireOp",EDGE,"E0.9"),sQuery(id+"F0.wireOp",EDGE,"E0.10"),sQuery(id+"F0.wireOp",EDGE,"E0.11"),sQuery(id+"F0.wireOp",EDGE,"E0.12"),sQuery(id+"F0.wireOp",EDGE,"E0.13"),sQuery(id+"F0.wireOp",EDGE,"E0.14"),sQuery(id+"F0.wireOp",EDGE,"E0.15"),sQuery(id+"F0.wireOp",EDGE,"E1"),sQuery(id+"F0.wireOp",EDGE,"E2.1"),sQuery(id+"F0.wireOp",EDGE,"E2.3"),sQuery(id+"F0.wireOp",EDGE,"E2.5"),sQuery(id+"F0.wireOp",EDGE,"E2.7"),subQ1,sQuery(id+"F0.wireOp",EDGE,"E2.11"),sQuery(id+"F0.wireOp",EDGE,"E2.13"),sQuery(id+"F0.wireOp",EDGE,"E2.15"),sQuery(id+"F0.wireOp",EDGE,"E3.1"),sQuery(id+"F0.wireOp",EDGE,"E3.3"),sQuery(id+"F0.wireOp",EDGE,"E3.5"),sQuery(id+"F0.wireOp",EDGE,"E3.7"),sQuery(id+"F0.wireOp",EDGE,"E3.9"),sQuery(id+"F0.wireOp",EDGE,"E3.11"),sQuery(id+"F0.wireOp",EDGE,"E3.13"),sQuery(id+"F0.wireOp",EDGE,"E3.15"),sQuery(id+"F0.wireOp",EDGE,"E4"),sQuery(id+"F0.wireOp",EDGE,"E5"),sQuery(id+"F0.wireOp",EDGE,"E6"),sQuery(id+"F0.wireOp",EDGE,"E7"),sQuery(id+"F0.wireOp",EDGE,"E8"),sQuery(id+"F0.wireOp",EDGE,"E9"),sQuery(id+"F0.wireOp",EDGE,"E10"),sQuery(id+"F0.wireOp",EDGE,"E11"),sQuery(id+"F0.wireOp",EDGE,"E12"),sQuery(id+"F0.wireOp",EDGE,"E13"),sQuery(id+"F0.wireOp",EDGE,"E14"),sQuery(id+"F0.wireOp",EDGE,"E15"),sQuery(id+"F0.wireOp",EDGE,"E16"),subQ0,sQuery(id+"F0.wireOp",EDGE,"E18"),sQuery(id+"F0.wireOp",EDGE,"E19")])],"isStart":true})]});}
            var Q23;
            {var subQ0=sQuery(id+"F0.wireOp",EDGE,"E17");var subQ1=sQuery(id+"F0.wireOp",EDGE,"E3.9");Q23=makeQuery(id+"F5.opChamfer","BLEND_EDGE",EDGE,{"blendedFrom":[makeQuery(id+"F1.opExtrude","SWEPT_EDGE",EDGE,{"disambiguationData":[OSD([sQuery(id+"F0.wireOp",EDGE,"E3.8"),subQ1,subQ0])]}),makeQuery(id+"F1.opExtrude","CAP_FACE",FACE,{"disambiguationData":[OSD([sQuery(id+"F0.wireOp",EDGE,"E0.0"),sQuery(id+"F0.wireOp",EDGE,"E0.1"),sQuery(id+"F0.wireOp",EDGE,"E0.2"),sQuery(id+"F0.wireOp",EDGE,"E0.3"),sQuery(id+"F0.wireOp",EDGE,"E0.4"),sQuery(id+"F0.wireOp",EDGE,"E0.5"),sQuery(id+"F0.wireOp",EDGE,"E0.6"),sQuery(id+"F0.wireOp",EDGE,"E0.7"),sQuery(id+"F0.wireOp",EDGE,"E0.8"),sQuery(id+"F0.wireOp",EDGE,"E0.9"),sQuery(id+"F0.wireOp",EDGE,"E0.10"),sQuery(id+"F0.wireOp",EDGE,"E0.11"),sQuery(id+"F0.wireOp",EDGE,"E0.12"),sQuery(id+"F0.wireOp",EDGE,"E0.13"),sQuery(id+"F0.wireOp",EDGE,"E0.14"),sQuery(id+"F0.wireOp",EDGE,"E0.15"),sQuery(id+"F0.wireOp",EDGE,"E1"),sQuery(id+"F0.wireOp",EDGE,"E2.1"),sQuery(id+"F0.wireOp",EDGE,"E2.3"),sQuery(id+"F0.wireOp",EDGE,"E2.5"),sQuery(id+"F0.wireOp",EDGE,"E2.7"),sQuery(id+"F0.wireOp",EDGE,"E2.9"),sQuery(id+"F0.wireOp",EDGE,"E2.11"),sQuery(id+"F0.wireOp",EDGE,"E2.13"),sQuery(id+"F0.wireOp",EDGE,"E2.15"),sQuery(id+"F0.wireOp",EDGE,"E3.1"),sQuery(id+"F0.wireOp",EDGE,"E3.3"),sQuery(id+"F0.wireOp",EDGE,"E3.5"),sQuery(id+"F0.wireOp",EDGE,"E3.7"),subQ1,sQuery(id+"F0.wireOp",EDGE,"E3.11"),sQuery(id+"F0.wireOp",EDGE,"E3.13"),sQuery(id+"F0.wireOp",EDGE,"E3.15"),sQuery(id+"F0.wireOp",EDGE,"E4"),sQuery(id+"F0.wireOp",EDGE,"E5"),sQuery(id+"F0.wireOp",EDGE,"E6"),sQuery(id+"F0.wireOp",EDGE,"E7"),sQuery(id+"F0.wireOp",EDGE,"E8"),sQuery(id+"F0.wireOp",EDGE,"E9"),sQuery(id+"F0.wireOp",EDGE,"E10"),sQuery(id+"F0.wireOp",EDGE,"E11"),sQuery(id+"F0.wireOp",EDGE,"E12"),sQuery(id+"F0.wireOp",EDGE,"E13"),sQuery(id+"F0.wireOp",EDGE,"E14"),sQuery(id+"F0.wireOp",EDGE,"E15"),sQuery(id+"F0.wireOp",EDGE,"E16"),subQ0,sQuery(id+"F0.wireOp",EDGE,"E18"),sQuery(id+"F0.wireOp",EDGE,"E19")])],"isStart":true})],"blendedInto":[makeQuery(id+"F1.opExtrude","CAP_FACE",FACE,{"disambiguationData":[OSD([sQuery(id+"F0.wireOp",EDGE,"E0.0"),sQuery(id+"F0.wireOp",EDGE,"E0.1"),sQuery(id+"F0.wireOp",EDGE,"E0.2"),sQuery(id+"F0.wireOp",EDGE,"E0.3"),sQuery(id+"F0.wireOp",EDGE,"E0.4"),sQuery(id+"F0.wireOp",EDGE,"E0.5"),sQuery(id+"F0.wireOp",EDGE,"E0.6"),sQuery(id+"F0.wireOp",EDGE,"E0.7"),sQuery(id+"F0.wireOp",EDGE,"E0.8"),sQuery(id+"F0.wireOp",EDGE,"E0.9"),sQuery(id+"F0.wireOp",EDGE,"E0.10"),sQuery(id+"F0.wireOp",EDGE,"E0.11"),sQuery(id+"F0.wireOp",EDGE,"E0.12"),sQuery(id+"F0.wireOp",EDGE,"E0.13"),sQuery(id+"F0.wireOp",EDGE,"E0.14"),sQuery(id+"F0.wireOp",EDGE,"E0.15"),sQuery(id+"F0.wireOp",EDGE,"E1"),sQuery(id+"F0.wireOp",EDGE,"E2.1"),sQuery(id+"F0.wireOp",EDGE,"E2.3"),sQuery(id+"F0.wireOp",EDGE,"E2.5"),sQuery(id+"F0.wireOp",EDGE,"E2.7"),sQuery(id+"F0.wireOp",EDGE,"E2.9"),sQuery(id+"F0.wireOp",EDGE,"E2.11"),sQuery(id+"F0.wireOp",EDGE,"E2.13"),sQuery(id+"F0.wireOp",EDGE,"E2.15"),sQuery(id+"F0.wireOp",EDGE,"E3.1"),sQuery(id+"F0.wireOp",EDGE,"E3.3"),sQuery(id+"F0.wireOp",EDGE,"E3.5"),sQuery(id+"F0.wireOp",EDGE,"E3.7"),subQ1,sQuery(id+"F0.wireOp",EDGE,"E3.11"),sQuery(id+"F0.wireOp",EDGE,"E3.13"),sQuery(id+"F0.wireOp",EDGE,"E3.15"),sQuery(id+"F0.wireOp",EDGE,"E4"),sQuery(id+"F0.wireOp",EDGE,"E5"),sQuery(id+"F0.wireOp",EDGE,"E6"),sQuery(id+"F0.wireOp",EDGE,"E7"),sQuery(id+"F0.wireOp",EDGE,"E8"),sQuery(id+"F0.wireOp",EDGE,"E9"),sQuery(id+"F0.wireOp",EDGE,"E10"),sQuery(id+"F0.wireOp",EDGE,"E11"),sQuery(id+"F0.wireOp",EDGE,"E12"),sQuery(id+"F0.wireOp",EDGE,"E13"),sQuery(id+"F0.wireOp",EDGE,"E14"),sQuery(id+"F0.wireOp",EDGE,"E15"),sQuery(id+"F0.wireOp",EDGE,"E16"),subQ0,sQuery(id+"F0.wireOp",EDGE,"E18"),sQuery(id+"F0.wireOp",EDGE,"E19")])],"isStart":true})]});}
            var Q24;
            {var subQ0=sQuery(id+"F0.wireOp",EDGE,"E16");var subQ1=sQuery(id+"F0.wireOp",EDGE,"E3.7");Q24=makeQuery(id+"F5.opChamfer","BLEND_EDGE",EDGE,{"blendedFrom":[makeQuery(id+"F1.opExtrude","SWEPT_EDGE",EDGE,{"disambiguationData":[OSD([subQ1,sQuery(id+"F0.wireOp",EDGE,"E3.8"),subQ0])]}),makeQuery(id+"F1.opExtrude","CAP_FACE",FACE,{"disambiguationData":[OSD([sQuery(id+"F0.wireOp",EDGE,"E0.0"),sQuery(id+"F0.wireOp",EDGE,"E0.1"),sQuery(id+"F0.wireOp",EDGE,"E0.2"),sQuery(id+"F0.wireOp",EDGE,"E0.3"),sQuery(id+"F0.wireOp",EDGE,"E0.4"),sQuery(id+"F0.wireOp",EDGE,"E0.5"),sQuery(id+"F0.wireOp",EDGE,"E0.6"),sQuery(id+"F0.wireOp",EDGE,"E0.7"),sQuery(id+"F0.wireOp",EDGE,"E0.8"),sQuery(id+"F0.wireOp",EDGE,"E0.9"),sQuery(id+"F0.wireOp",EDGE,"E0.10"),sQuery(id+"F0.wireOp",EDGE,"E0.11"),sQuery(id+"F0.wireOp",EDGE,"E0.12"),sQuery(id+"F0.wireOp",EDGE,"E0.13"),sQuery(id+"F0.wireOp",EDGE,"E0.14"),sQuery(id+"F0.wireOp",EDGE,"E0.15"),sQuery(id+"F0.wireOp",EDGE,"E1"),sQuery(id+"F0.wireOp",EDGE,"E2.1"),sQuery(id+"F0.wireOp",EDGE,"E2.3"),sQuery(id+"F0.wireOp",EDGE,"E2.5"),sQuery(id+"F0.wireOp",EDGE,"E2.7"),sQuery(id+"F0.wireOp",EDGE,"E2.9"),sQuery(id+"F0.wireOp",EDGE,"E2.11"),sQuery(id+"F0.wireOp",EDGE,"E2.13"),sQuery(id+"F0.wireOp",EDGE,"E2.15"),sQuery(id+"F0.wireOp",EDGE,"E3.1"),sQuery(id+"F0.wireOp",EDGE,"E3.3"),sQuery(id+"F0.wireOp",EDGE,"E3.5"),subQ1,sQuery(id+"F0.wireOp",EDGE,"E3.9"),sQuery(id+"F0.wireOp",EDGE,"E3.11"),sQuery(id+"F0.wireOp",EDGE,"E3.13"),sQuery(id+"F0.wireOp",EDGE,"E3.15"),sQuery(id+"F0.wireOp",EDGE,"E4"),sQuery(id+"F0.wireOp",EDGE,"E5"),sQuery(id+"F0.wireOp",EDGE,"E6"),sQuery(id+"F0.wireOp",EDGE,"E7"),sQuery(id+"F0.wireOp",EDGE,"E8"),sQuery(id+"F0.wireOp",EDGE,"E9"),sQuery(id+"F0.wireOp",EDGE,"E10"),sQuery(id+"F0.wireOp",EDGE,"E11"),sQuery(id+"F0.wireOp",EDGE,"E12"),sQuery(id+"F0.wireOp",EDGE,"E13"),sQuery(id+"F0.wireOp",EDGE,"E14"),sQuery(id+"F0.wireOp",EDGE,"E15"),subQ0,sQuery(id+"F0.wireOp",EDGE,"E17"),sQuery(id+"F0.wireOp",EDGE,"E18"),sQuery(id+"F0.wireOp",EDGE,"E19")])],"isStart":true})],"blendedInto":[makeQuery(id+"F1.opExtrude","CAP_FACE",FACE,{"disambiguationData":[OSD([sQuery(id+"F0.wireOp",EDGE,"E0.0"),sQuery(id+"F0.wireOp",EDGE,"E0.1"),sQuery(id+"F0.wireOp",EDGE,"E0.2"),sQuery(id+"F0.wireOp",EDGE,"E0.3"),sQuery(id+"F0.wireOp",EDGE,"E0.4"),sQuery(id+"F0.wireOp",EDGE,"E0.5"),sQuery(id+"F0.wireOp",EDGE,"E0.6"),sQuery(id+"F0.wireOp",EDGE,"E0.7"),sQuery(id+"F0.wireOp",EDGE,"E0.8"),sQuery(id+"F0.wireOp",EDGE,"E0.9"),sQuery(id+"F0.wireOp",EDGE,"E0.10"),sQuery(id+"F0.wireOp",EDGE,"E0.11"),sQuery(id+"F0.wireOp",EDGE,"E0.12"),sQuery(id+"F0.wireOp",EDGE,"E0.13"),sQuery(id+"F0.wireOp",EDGE,"E0.14"),sQuery(id+"F0.wireOp",EDGE,"E0.15"),sQuery(id+"F0.wireOp",EDGE,"E1"),sQuery(id+"F0.wireOp",EDGE,"E2.1"),sQuery(id+"F0.wireOp",EDGE,"E2.3"),sQuery(id+"F0.wireOp",EDGE,"E2.5"),sQuery(id+"F0.wireOp",EDGE,"E2.7"),sQuery(id+"F0.wireOp",EDGE,"E2.9"),sQuery(id+"F0.wireOp",EDGE,"E2.11"),sQuery(id+"F0.wireOp",EDGE,"E2.13"),sQuery(id+"F0.wireOp",EDGE,"E2.15"),sQuery(id+"F0.wireOp",EDGE,"E3.1"),sQuery(id+"F0.wireOp",EDGE,"E3.3"),sQuery(id+"F0.wireOp",EDGE,"E3.5"),subQ1,sQuery(id+"F0.wireOp",EDGE,"E3.9"),sQuery(id+"F0.wireOp",EDGE,"E3.11"),sQuery(id+"F0.wireOp",EDGE,"E3.13"),sQuery(id+"F0.wireOp",EDGE,"E3.15"),sQuery(id+"F0.wireOp",EDGE,"E4"),sQuery(id+"F0.wireOp",EDGE,"E5"),sQuery(id+"F0.wireOp",EDGE,"E6"),sQuery(id+"F0.wireOp",EDGE,"E7"),sQuery(id+"F0.wireOp",EDGE,"E8"),sQuery(id+"F0.wireOp",EDGE,"E9"),sQuery(id+"F0.wireOp",EDGE,"E10"),sQuery(id+"F0.wireOp",EDGE,"E11"),sQuery(id+"F0.wireOp",EDGE,"E12"),sQuery(id+"F0.wireOp",EDGE,"E13"),sQuery(id+"F0.wireOp",EDGE,"E14"),sQuery(id+"F0.wireOp",EDGE,"E15"),subQ0,sQuery(id+"F0.wireOp",EDGE,"E17"),sQuery(id+"F0.wireOp",EDGE,"E18"),sQuery(id+"F0.wireOp",EDGE,"E19")])],"isStart":true})]});}
            var Q25;
            Q25=makeQuery(id+"F1.opExtrude","CAP_EDGE",EDGE,{"disambiguationData":[OSD([sQuery(id+"F0.wireOp",EDGE,"E16")])],"isStart":true});
            var Q26;
            {var subQ0=sQuery(id+"F0.wireOp",EDGE,"E16");var subQ1=sQuery(id+"F0.wireOp",EDGE,"E2.7");Q26=makeQuery(id+"F5.opChamfer","BLEND_EDGE",EDGE,{"blendedFrom":[makeQuery(id+"F1.opExtrude","SWEPT_EDGE",EDGE,{"disambiguationData":[OSD([subQ1,sQuery(id+"F0.wireOp",EDGE,"E2.8"),subQ0])]}),makeQuery(id+"F1.opExtrude","CAP_FACE",FACE,{"disambiguationData":[OSD([sQuery(id+"F0.wireOp",EDGE,"E0.0"),sQuery(id+"F0.wireOp",EDGE,"E0.1"),sQuery(id+"F0.wireOp",EDGE,"E0.2"),sQuery(id+"F0.wireOp",EDGE,"E0.3"),sQuery(id+"F0.wireOp",EDGE,"E0.4"),sQuery(id+"F0.wireOp",EDGE,"E0.5"),sQuery(id+"F0.wireOp",EDGE,"E0.6"),sQuery(id+"F0.wireOp",EDGE,"E0.7"),sQuery(id+"F0.wireOp",EDGE,"E0.8"),sQuery(id+"F0.wireOp",EDGE,"E0.9"),sQuery(id+"F0.wireOp",EDGE,"E0.10"),sQuery(id+"F0.wireOp",EDGE,"E0.11"),sQuery(id+"F0.wireOp",EDGE,"E0.12"),sQuery(id+"F0.wireOp",EDGE,"E0.13"),sQuery(id+"F0.wireOp",EDGE,"E0.14"),sQuery(id+"F0.wireOp",EDGE,"E0.15"),sQuery(id+"F0.wireOp",EDGE,"E1"),sQuery(id+"F0.wireOp",EDGE,"E2.1"),sQuery(id+"F0.wireOp",EDGE,"E2.3"),sQuery(id+"F0.wireOp",EDGE,"E2.5"),subQ1,sQuery(id+"F0.wireOp",EDGE,"E2.9"),sQuery(id+"F0.wireOp",EDGE,"E2.11"),sQuery(id+"F0.wireOp",EDGE,"E2.13"),sQuery(id+"F0.wireOp",EDGE,"E2.15"),sQuery(id+"F0.wireOp",EDGE,"E3.1"),sQuery(id+"F0.wireOp",EDGE,"E3.3"),sQuery(id+"F0.wireOp",EDGE,"E3.5"),sQuery(id+"F0.wireOp",EDGE,"E3.7"),sQuery(id+"F0.wireOp",EDGE,"E3.9"),sQuery(id+"F0.wireOp",EDGE,"E3.11"),sQuery(id+"F0.wireOp",EDGE,"E3.13"),sQuery(id+"F0.wireOp",EDGE,"E3.15"),sQuery(id+"F0.wireOp",EDGE,"E4"),sQuery(id+"F0.wireOp",EDGE,"E5"),sQuery(id+"F0.wireOp",EDGE,"E6"),sQuery(id+"F0.wireOp",EDGE,"E7"),sQuery(id+"F0.wireOp",EDGE,"E8"),sQuery(id+"F0.wireOp",EDGE,"E9"),sQuery(id+"F0.wireOp",EDGE,"E10"),sQuery(id+"F0.wireOp",EDGE,"E11"),sQuery(id+"F0.wireOp",EDGE,"E12"),sQuery(id+"F0.wireOp",EDGE,"E13"),sQuery(id+"F0.wireOp",EDGE,"E14"),sQuery(id+"F0.wireOp",EDGE,"E15"),subQ0,sQuery(id+"F0.wireOp",EDGE,"E17"),sQuery(id+"F0.wireOp",EDGE,"E18"),sQuery(id+"F0.wireOp",EDGE,"E19")])],"isStart":true})],"blendedInto":[makeQuery(id+"F1.opExtrude","CAP_FACE",FACE,{"disambiguationData":[OSD([sQuery(id+"F0.wireOp",EDGE,"E0.0"),sQuery(id+"F0.wireOp",EDGE,"E0.1"),sQuery(id+"F0.wireOp",EDGE,"E0.2"),sQuery(id+"F0.wireOp",EDGE,"E0.3"),sQuery(id+"F0.wireOp",EDGE,"E0.4"),sQuery(id+"F0.wireOp",EDGE,"E0.5"),sQuery(id+"F0.wireOp",EDGE,"E0.6"),sQuery(id+"F0.wireOp",EDGE,"E0.7"),sQuery(id+"F0.wireOp",EDGE,"E0.8"),sQuery(id+"F0.wireOp",EDGE,"E0.9"),sQuery(id+"F0.wireOp",EDGE,"E0.10"),sQuery(id+"F0.wireOp",EDGE,"E0.11"),sQuery(id+"F0.wireOp",EDGE,"E0.12"),sQuery(id+"F0.wireOp",EDGE,"E0.13"),sQuery(id+"F0.wireOp",EDGE,"E0.14"),sQuery(id+"F0.wireOp",EDGE,"E0.15"),sQuery(id+"F0.wireOp",EDGE,"E1"),sQuery(id+"F0.wireOp",EDGE,"E2.1"),sQuery(id+"F0.wireOp",EDGE,"E2.3"),sQuery(id+"F0.wireOp",EDGE,"E2.5"),subQ1,sQuery(id+"F0.wireOp",EDGE,"E2.9"),sQuery(id+"F0.wireOp",EDGE,"E2.11"),sQuery(id+"F0.wireOp",EDGE,"E2.13"),sQuery(id+"F0.wireOp",EDGE,"E2.15"),sQuery(id+"F0.wireOp",EDGE,"E3.1"),sQuery(id+"F0.wireOp",EDGE,"E3.3"),sQuery(id+"F0.wireOp",EDGE,"E3.5"),sQuery(id+"F0.wireOp",EDGE,"E3.7"),sQuery(id+"F0.wireOp",EDGE,"E3.9"),sQuery(id+"F0.wireOp",EDGE,"E3.11"),sQuery(id+"F0.wireOp",EDGE,"E3.13"),sQuery(id+"F0.wireOp",EDGE,"E3.15"),sQuery(id+"F0.wireOp",EDGE,"E4"),sQuery(id+"F0.wireOp",EDGE,"E5"),sQuery(id+"F0.wireOp",EDGE,"E6"),sQuery(id+"F0.wireOp",EDGE,"E7"),sQuery(id+"F0.wireOp",EDGE,"E8"),sQuery(id+"F0.wireOp",EDGE,"E9"),sQuery(id+"F0.wireOp",EDGE,"E10"),sQuery(id+"F0.wireOp",EDGE,"E11"),sQuery(id+"F0.wireOp",EDGE,"E12"),sQuery(id+"F0.wireOp",EDGE,"E13"),sQuery(id+"F0.wireOp",EDGE,"E14"),sQuery(id+"F0.wireOp",EDGE,"E15"),subQ0,sQuery(id+"F0.wireOp",EDGE,"E17"),sQuery(id+"F0.wireOp",EDGE,"E18"),sQuery(id+"F0.wireOp",EDGE,"E19")])],"isStart":true})]});}
            var Q27;
            Q27=makeQuery(id+"F1.opExtrude","CAP_EDGE",EDGE,{"disambiguationData":[OSD([sQuery(id+"F0.wireOp",EDGE,"E2.7")])],"isStart":true});
            var Q28;
            {var subQ0=sQuery(id+"F0.wireOp",EDGE,"E15");var subQ1=sQuery(id+"F0.wireOp",EDGE,"E2.7");Q28=makeQuery(id+"F5.opChamfer","BLEND_EDGE",EDGE,{"blendedFrom":[makeQuery(id+"F1.opExtrude","SWEPT_EDGE",EDGE,{"disambiguationData":[OSD([sQuery(id+"F0.wireOp",EDGE,"E2.6"),subQ1,subQ0])]}),makeQuery(id+"F1.opExtrude","CAP_FACE",FACE,{"disambiguationData":[OSD([sQuery(id+"F0.wireOp",EDGE,"E0.0"),sQuery(id+"F0.wireOp",EDGE,"E0.1"),sQuery(id+"F0.wireOp",EDGE,"E0.2"),sQuery(id+"F0.wireOp",EDGE,"E0.3"),sQuery(id+"F0.wireOp",EDGE,"E0.4"),sQuery(id+"F0.wireOp",EDGE,"E0.5"),sQuery(id+"F0.wireOp",EDGE,"E0.6"),sQuery(id+"F0.wireOp",EDGE,"E0.7"),sQuery(id+"F0.wireOp",EDGE,"E0.8"),sQuery(id+"F0.wireOp",EDGE,"E0.9"),sQuery(id+"F0.wireOp",EDGE,"E0.10"),sQuery(id+"F0.wireOp",EDGE,"E0.11"),sQuery(id+"F0.wireOp",EDGE,"E0.12"),sQuery(id+"F0.wireOp",EDGE,"E0.13"),sQuery(id+"F0.wireOp",EDGE,"E0.14"),sQuery(id+"F0.wireOp",EDGE,"E0.15"),sQuery(id+"F0.wireOp",EDGE,"E1"),sQuery(id+"F0.wireOp",EDGE,"E2.1"),sQuery(id+"F0.wireOp",EDGE,"E2.3"),sQuery(id+"F0.wireOp",EDGE,"E2.5"),subQ1,sQuery(id+"F0.wireOp",EDGE,"E2.9"),sQuery(id+"F0.wireOp",EDGE,"E2.11"),sQuery(id+"F0.wireOp",EDGE,"E2.13"),sQuery(id+"F0.wireOp",EDGE,"E2.15"),sQuery(id+"F0.wireOp",EDGE,"E3.1"),sQuery(id+"F0.wireOp",EDGE,"E3.3"),sQuery(id+"F0.wireOp",EDGE,"E3.5"),sQuery(id+"F0.wireOp",EDGE,"E3.7"),sQuery(id+"F0.wireOp",EDGE,"E3.9"),sQuery(id+"F0.wireOp",EDGE,"E3.11"),sQuery(id+"F0.wireOp",EDGE,"E3.13"),sQuery(id+"F0.wireOp",EDGE,"E3.15"),sQuery(id+"F0.wireOp",EDGE,"E4"),sQuery(id+"F0.wireOp",EDGE,"E5"),sQuery(id+"F0.wireOp",EDGE,"E6"),sQuery(id+"F0.wireOp",EDGE,"E7"),sQuery(id+"F0.wireOp",EDGE,"E8"),sQuery(id+"F0.wireOp",EDGE,"E9"),sQuery(id+"F0.wireOp",EDGE,"E10"),sQuery(id+"F0.wireOp",EDGE,"E11"),sQuery(id+"F0.wireOp",EDGE,"E12"),sQuery(id+"F0.wireOp",EDGE,"E13"),sQuery(id+"F0.wireOp",EDGE,"E14"),subQ0,sQuery(id+"F0.wireOp",EDGE,"E16"),sQuery(id+"F0.wireOp",EDGE,"E17"),sQuery(id+"F0.wireOp",EDGE,"E18"),sQuery(id+"F0.wireOp",EDGE,"E19")])],"isStart":true})],"blendedInto":[makeQuery(id+"F1.opExtrude","CAP_FACE",FACE,{"disambiguationData":[OSD([sQuery(id+"F0.wireOp",EDGE,"E0.0"),sQuery(id+"F0.wireOp",EDGE,"E0.1"),sQuery(id+"F0.wireOp",EDGE,"E0.2"),sQuery(id+"F0.wireOp",EDGE,"E0.3"),sQuery(id+"F0.wireOp",EDGE,"E0.4"),sQuery(id+"F0.wireOp",EDGE,"E0.5"),sQuery(id+"F0.wireOp",EDGE,"E0.6"),sQuery(id+"F0.wireOp",EDGE,"E0.7"),sQuery(id+"F0.wireOp",EDGE,"E0.8"),sQuery(id+"F0.wireOp",EDGE,"E0.9"),sQuery(id+"F0.wireOp",EDGE,"E0.10"),sQuery(id+"F0.wireOp",EDGE,"E0.11"),sQuery(id+"F0.wireOp",EDGE,"E0.12"),sQuery(id+"F0.wireOp",EDGE,"E0.13"),sQuery(id+"F0.wireOp",EDGE,"E0.14"),sQuery(id+"F0.wireOp",EDGE,"E0.15"),sQuery(id+"F0.wireOp",EDGE,"E1"),sQuery(id+"F0.wireOp",EDGE,"E2.1"),sQuery(id+"F0.wireOp",EDGE,"E2.3"),sQuery(id+"F0.wireOp",EDGE,"E2.5"),subQ1,sQuery(id+"F0.wireOp",EDGE,"E2.9"),sQuery(id+"F0.wireOp",EDGE,"E2.11"),sQuery(id+"F0.wireOp",EDGE,"E2.13"),sQuery(id+"F0.wireOp",EDGE,"E2.15"),sQuery(id+"F0.wireOp",EDGE,"E3.1"),sQuery(id+"F0.wireOp",EDGE,"E3.3"),sQuery(id+"F0.wireOp",EDGE,"E3.5"),sQuery(id+"F0.wireOp",EDGE,"E3.7"),sQuery(id+"F0.wireOp",EDGE,"E3.9"),sQuery(id+"F0.wireOp",EDGE,"E3.11"),sQuery(id+"F0.wireOp",EDGE,"E3.13"),sQuery(id+"F0.wireOp",EDGE,"E3.15"),sQuery(id+"F0.wireOp",EDGE,"E4"),sQuery(id+"F0.wireOp",EDGE,"E5"),sQuery(id+"F0.wireOp",EDGE,"E6"),sQuery(id+"F0.wireOp",EDGE,"E7"),sQuery(id+"F0.wireOp",EDGE,"E8"),sQuery(id+"F0.wireOp",EDGE,"E9"),sQuery(id+"F0.wireOp",EDGE,"E10"),sQuery(id+"F0.wireOp",EDGE,"E11"),sQuery(id+"F0.wireOp",EDGE,"E12"),sQuery(id+"F0.wireOp",EDGE,"E13"),sQuery(id+"F0.wireOp",EDGE,"E14"),subQ0,sQuery(id+"F0.wireOp",EDGE,"E16"),sQuery(id+"F0.wireOp",EDGE,"E17"),sQuery(id+"F0.wireOp",EDGE,"E18"),sQuery(id+"F0.wireOp",EDGE,"E19")])],"isStart":true})]});}
            var Q29;
            Q29=makeQuery(id+"F1.opExtrude","CAP_EDGE",EDGE,{"disambiguationData":[OSD([sQuery(id+"F0.wireOp",EDGE,"E15")])],"isStart":true});
            var Q30;
            {var subQ0=sQuery(id+"F0.wireOp",EDGE,"E15");var subQ1=sQuery(id+"F0.wireOp",EDGE,"E3.7");Q30=makeQuery(id+"F5.opChamfer","BLEND_EDGE",EDGE,{"blendedFrom":[makeQuery(id+"F1.opExtrude","SWEPT_EDGE",EDGE,{"disambiguationData":[OSD([sQuery(id+"F0.wireOp",EDGE,"E3.6"),subQ1,subQ0])]}),makeQuery(id+"F1.opExtrude","CAP_FACE",FACE,{"disambiguationData":[OSD([sQuery(id+"F0.wireOp",EDGE,"E0.0"),sQuery(id+"F0.wireOp",EDGE,"E0.1"),sQuery(id+"F0.wireOp",EDGE,"E0.2"),sQuery(id+"F0.wireOp",EDGE,"E0.3"),sQuery(id+"F0.wireOp",EDGE,"E0.4"),sQuery(id+"F0.wireOp",EDGE,"E0.5"),sQuery(id+"F0.wireOp",EDGE,"E0.6"),sQuery(id+"F0.wireOp",EDGE,"E0.7"),sQuery(id+"F0.wireOp",EDGE,"E0.8"),sQuery(id+"F0.wireOp",EDGE,"E0.9"),sQuery(id+"F0.wireOp",EDGE,"E0.10"),sQuery(id+"F0.wireOp",EDGE,"E0.11"),sQuery(id+"F0.wireOp",EDGE,"E0.12"),sQuery(id+"F0.wireOp",EDGE,"E0.13"),sQuery(id+"F0.wireOp",EDGE,"E0.14"),sQuery(id+"F0.wireOp",EDGE,"E0.15"),sQuery(id+"F0.wireOp",EDGE,"E1"),sQuery(id+"F0.wireOp",EDGE,"E2.1"),sQuery(id+"F0.wireOp",EDGE,"E2.3"),sQuery(id+"F0.wireOp",EDGE,"E2.5"),sQuery(id+"F0.wireOp",EDGE,"E2.7"),sQuery(id+"F0.wireOp",EDGE,"E2.9"),sQuery(id+"F0.wireOp",EDGE,"E2.11"),sQuery(id+"F0.wireOp",EDGE,"E2.13"),sQuery(id+"F0.wireOp",EDGE,"E2.15"),sQuery(id+"F0.wireOp",EDGE,"E3.1"),sQuery(id+"F0.wireOp",EDGE,"E3.3"),sQuery(id+"F0.wireOp",EDGE,"E3.5"),subQ1,sQuery(id+"F0.wireOp",EDGE,"E3.9"),sQuery(id+"F0.wireOp",EDGE,"E3.11"),sQuery(id+"F0.wireOp",EDGE,"E3.13"),sQuery(id+"F0.wireOp",EDGE,"E3.15"),sQuery(id+"F0.wireOp",EDGE,"E4"),sQuery(id+"F0.wireOp",EDGE,"E5"),sQuery(id+"F0.wireOp",EDGE,"E6"),sQuery(id+"F0.wireOp",EDGE,"E7"),sQuery(id+"F0.wireOp",EDGE,"E8"),sQuery(id+"F0.wireOp",EDGE,"E9"),sQuery(id+"F0.wireOp",EDGE,"E10"),sQuery(id+"F0.wireOp",EDGE,"E11"),sQuery(id+"F0.wireOp",EDGE,"E12"),sQuery(id+"F0.wireOp",EDGE,"E13"),sQuery(id+"F0.wireOp",EDGE,"E14"),subQ0,sQuery(id+"F0.wireOp",EDGE,"E16"),sQuery(id+"F0.wireOp",EDGE,"E17"),sQuery(id+"F0.wireOp",EDGE,"E18"),sQuery(id+"F0.wireOp",EDGE,"E19")])],"isStart":true})],"blendedInto":[makeQuery(id+"F1.opExtrude","CAP_FACE",FACE,{"disambiguationData":[OSD([sQuery(id+"F0.wireOp",EDGE,"E0.0"),sQuery(id+"F0.wireOp",EDGE,"E0.1"),sQuery(id+"F0.wireOp",EDGE,"E0.2"),sQuery(id+"F0.wireOp",EDGE,"E0.3"),sQuery(id+"F0.wireOp",EDGE,"E0.4"),sQuery(id+"F0.wireOp",EDGE,"E0.5"),sQuery(id+"F0.wireOp",EDGE,"E0.6"),sQuery(id+"F0.wireOp",EDGE,"E0.7"),sQuery(id+"F0.wireOp",EDGE,"E0.8"),sQuery(id+"F0.wireOp",EDGE,"E0.9"),sQuery(id+"F0.wireOp",EDGE,"E0.10"),sQuery(id+"F0.wireOp",EDGE,"E0.11"),sQuery(id+"F0.wireOp",EDGE,"E0.12"),sQuery(id+"F0.wireOp",EDGE,"E0.13"),sQuery(id+"F0.wireOp",EDGE,"E0.14"),sQuery(id+"F0.wireOp",EDGE,"E0.15"),sQuery(id+"F0.wireOp",EDGE,"E1"),sQuery(id+"F0.wireOp",EDGE,"E2.1"),sQuery(id+"F0.wireOp",EDGE,"E2.3"),sQuery(id+"F0.wireOp",EDGE,"E2.5"),sQuery(id+"F0.wireOp",EDGE,"E2.7"),sQuery(id+"F0.wireOp",EDGE,"E2.9"),sQuery(id+"F0.wireOp",EDGE,"E2.11"),sQuery(id+"F0.wireOp",EDGE,"E2.13"),sQuery(id+"F0.wireOp",EDGE,"E2.15"),sQuery(id+"F0.wireOp",EDGE,"E3.1"),sQuery(id+"F0.wireOp",EDGE,"E3.3"),sQuery(id+"F0.wireOp",EDGE,"E3.5"),subQ1,sQuery(id+"F0.wireOp",EDGE,"E3.9"),sQuery(id+"F0.wireOp",EDGE,"E3.11"),sQuery(id+"F0.wireOp",EDGE,"E3.13"),sQuery(id+"F0.wireOp",EDGE,"E3.15"),sQuery(id+"F0.wireOp",EDGE,"E4"),sQuery(id+"F0.wireOp",EDGE,"E5"),sQuery(id+"F0.wireOp",EDGE,"E6"),sQuery(id+"F0.wireOp",EDGE,"E7"),sQuery(id+"F0.wireOp",EDGE,"E8"),sQuery(id+"F0.wireOp",EDGE,"E9"),sQuery(id+"F0.wireOp",EDGE,"E10"),sQuery(id+"F0.wireOp",EDGE,"E11"),sQuery(id+"F0.wireOp",EDGE,"E12"),sQuery(id+"F0.wireOp",EDGE,"E13"),sQuery(id+"F0.wireOp",EDGE,"E14"),subQ0,sQuery(id+"F0.wireOp",EDGE,"E16"),sQuery(id+"F0.wireOp",EDGE,"E17"),sQuery(id+"F0.wireOp",EDGE,"E18"),sQuery(id+"F0.wireOp",EDGE,"E19")])],"isStart":true})]});}
            var Q31;
            Q31=makeQuery(id+"F1.opExtrude","CAP_EDGE",EDGE,{"disambiguationData":[OSD([sQuery(id+"F0.wireOp",EDGE,"E3.7")])],"isStart":true});
            var Q32;
            Q32=makeQuery(id+"F1.opExtrude","CAP_EDGE",EDGE,{"disambiguationData":[OSD([sQuery(id+"F0.wireOp",EDGE,"E13")])],"isStart":true});
            var Q33;
            Q33=makeQuery(id+"F1.opExtrude","CAP_EDGE",EDGE,{"disambiguationData":[OSD([sQuery(id+"F0.wireOp",EDGE,"E14")])],"isStart":true});
            var Q34;
            Q34=makeQuery(id+"F1.opExtrude","CAP_EDGE",EDGE,{"disambiguationData":[OSD([sQuery(id+"F0.wireOp",EDGE,"E3.5")])],"isStart":true});
            var Q35;
            Q35=makeQuery(id+"F1.opExtrude","CAP_EDGE",EDGE,{"disambiguationData":[OSD([sQuery(id+"F0.wireOp",EDGE,"E2.5")])],"isStart":true});
            var Q36;
            {var subQ0=sQuery(id+"F0.wireOp",EDGE,"E14");var subQ1=sQuery(id+"F0.wireOp",EDGE,"E2.5");Q36=makeQuery(id+"F5.opChamfer","BLEND_EDGE",EDGE,{"blendedFrom":[makeQuery(id+"F1.opExtrude","SWEPT_EDGE",EDGE,{"disambiguationData":[OSD([subQ1,sQuery(id+"F0.wireOp",EDGE,"E2.6"),subQ0])]}),makeQuery(id+"F1.opExtrude","CAP_FACE",FACE,{"disambiguationData":[OSD([sQuery(id+"F0.wireOp",EDGE,"E0.0"),sQuery(id+"F0.wireOp",EDGE,"E0.1"),sQuery(id+"F0.wireOp",EDGE,"E0.2"),sQuery(id+"F0.wireOp",EDGE,"E0.3"),sQuery(id+"F0.wireOp",EDGE,"E0.4"),sQuery(id+"F0.wireOp",EDGE,"E0.5"),sQuery(id+"F0.wireOp",EDGE,"E0.6"),sQuery(id+"F0.wireOp",EDGE,"E0.7"),sQuery(id+"F0.wireOp",EDGE,"E0.8"),sQuery(id+"F0.wireOp",EDGE,"E0.9"),sQuery(id+"F0.wireOp",EDGE,"E0.10"),sQuery(id+"F0.wireOp",EDGE,"E0.11"),sQuery(id+"F0.wireOp",EDGE,"E0.12"),sQuery(id+"F0.wireOp",EDGE,"E0.13"),sQuery(id+"F0.wireOp",EDGE,"E0.14"),sQuery(id+"F0.wireOp",EDGE,"E0.15"),sQuery(id+"F0.wireOp",EDGE,"E1"),sQuery(id+"F0.wireOp",EDGE,"E2.1"),sQuery(id+"F0.wireOp",EDGE,"E2.3"),subQ1,sQuery(id+"F0.wireOp",EDGE,"E2.7"),sQuery(id+"F0.wireOp",EDGE,"E2.9"),sQuery(id+"F0.wireOp",EDGE,"E2.11"),sQuery(id+"F0.wireOp",EDGE,"E2.13"),sQuery(id+"F0.wireOp",EDGE,"E2.15"),sQuery(id+"F0.wireOp",EDGE,"E3.1"),sQuery(id+"F0.wireOp",EDGE,"E3.3"),sQuery(id+"F0.wireOp",EDGE,"E3.5"),sQuery(id+"F0.wireOp",EDGE,"E3.7"),sQuery(id+"F0.wireOp",EDGE,"E3.9"),sQuery(id+"F0.wireOp",EDGE,"E3.11"),sQuery(id+"F0.wireOp",EDGE,"E3.13"),sQuery(id+"F0.wireOp",EDGE,"E3.15"),sQuery(id+"F0.wireOp",EDGE,"E4"),sQuery(id+"F0.wireOp",EDGE,"E5"),sQuery(id+"F0.wireOp",EDGE,"E6"),sQuery(id+"F0.wireOp",EDGE,"E7"),sQuery(id+"F0.wireOp",EDGE,"E8"),sQuery(id+"F0.wireOp",EDGE,"E9"),sQuery(id+"F0.wireOp",EDGE,"E10"),sQuery(id+"F0.wireOp",EDGE,"E11"),sQuery(id+"F0.wireOp",EDGE,"E12"),sQuery(id+"F0.wireOp",EDGE,"E13"),subQ0,sQuery(id+"F0.wireOp",EDGE,"E15"),sQuery(id+"F0.wireOp",EDGE,"E16"),sQuery(id+"F0.wireOp",EDGE,"E17"),sQuery(id+"F0.wireOp",EDGE,"E18"),sQuery(id+"F0.wireOp",EDGE,"E19")])],"isStart":true})],"blendedInto":[makeQuery(id+"F1.opExtrude","CAP_FACE",FACE,{"disambiguationData":[OSD([sQuery(id+"F0.wireOp",EDGE,"E0.0"),sQuery(id+"F0.wireOp",EDGE,"E0.1"),sQuery(id+"F0.wireOp",EDGE,"E0.2"),sQuery(id+"F0.wireOp",EDGE,"E0.3"),sQuery(id+"F0.wireOp",EDGE,"E0.4"),sQuery(id+"F0.wireOp",EDGE,"E0.5"),sQuery(id+"F0.wireOp",EDGE,"E0.6"),sQuery(id+"F0.wireOp",EDGE,"E0.7"),sQuery(id+"F0.wireOp",EDGE,"E0.8"),sQuery(id+"F0.wireOp",EDGE,"E0.9"),sQuery(id+"F0.wireOp",EDGE,"E0.10"),sQuery(id+"F0.wireOp",EDGE,"E0.11"),sQuery(id+"F0.wireOp",EDGE,"E0.12"),sQuery(id+"F0.wireOp",EDGE,"E0.13"),sQuery(id+"F0.wireOp",EDGE,"E0.14"),sQuery(id+"F0.wireOp",EDGE,"E0.15"),sQuery(id+"F0.wireOp",EDGE,"E1"),sQuery(id+"F0.wireOp",EDGE,"E2.1"),sQuery(id+"F0.wireOp",EDGE,"E2.3"),subQ1,sQuery(id+"F0.wireOp",EDGE,"E2.7"),sQuery(id+"F0.wireOp",EDGE,"E2.9"),sQuery(id+"F0.wireOp",EDGE,"E2.11"),sQuery(id+"F0.wireOp",EDGE,"E2.13"),sQuery(id+"F0.wireOp",EDGE,"E2.15"),sQuery(id+"F0.wireOp",EDGE,"E3.1"),sQuery(id+"F0.wireOp",EDGE,"E3.3"),sQuery(id+"F0.wireOp",EDGE,"E3.5"),sQuery(id+"F0.wireOp",EDGE,"E3.7"),sQuery(id+"F0.wireOp",EDGE,"E3.9"),sQuery(id+"F0.wireOp",EDGE,"E3.11"),sQuery(id+"F0.wireOp",EDGE,"E3.13"),sQuery(id+"F0.wireOp",EDGE,"E3.15"),sQuery(id+"F0.wireOp",EDGE,"E4"),sQuery(id+"F0.wireOp",EDGE,"E5"),sQuery(id+"F0.wireOp",EDGE,"E6"),sQuery(id+"F0.wireOp",EDGE,"E7"),sQuery(id+"F0.wireOp",EDGE,"E8"),sQuery(id+"F0.wireOp",EDGE,"E9"),sQuery(id+"F0.wireOp",EDGE,"E10"),sQuery(id+"F0.wireOp",EDGE,"E11"),sQuery(id+"F0.wireOp",EDGE,"E12"),sQuery(id+"F0.wireOp",EDGE,"E13"),subQ0,sQuery(id+"F0.wireOp",EDGE,"E15"),sQuery(id+"F0.wireOp",EDGE,"E16"),sQuery(id+"F0.wireOp",EDGE,"E17"),sQuery(id+"F0.wireOp",EDGE,"E18"),sQuery(id+"F0.wireOp",EDGE,"E19")])],"isStart":true})]});}
            var Q37;
            {var subQ0=sQuery(id+"F0.wireOp",EDGE,"E13");var subQ1=sQuery(id+"F0.wireOp",EDGE,"E2.5");Q37=makeQuery(id+"F5.opChamfer","BLEND_EDGE",EDGE,{"blendedFrom":[makeQuery(id+"F1.opExtrude","SWEPT_EDGE",EDGE,{"disambiguationData":[OSD([sQuery(id+"F0.wireOp",EDGE,"E2.4"),subQ1,subQ0])]}),makeQuery(id+"F1.opExtrude","CAP_FACE",FACE,{"disambiguationData":[OSD([sQuery(id+"F0.wireOp",EDGE,"E0.0"),sQuery(id+"F0.wireOp",EDGE,"E0.1"),sQuery(id+"F0.wireOp",EDGE,"E0.2"),sQuery(id+"F0.wireOp",EDGE,"E0.3"),sQuery(id+"F0.wireOp",EDGE,"E0.4"),sQuery(id+"F0.wireOp",EDGE,"E0.5"),sQuery(id+"F0.wireOp",EDGE,"E0.6"),sQuery(id+"F0.wireOp",EDGE,"E0.7"),sQuery(id+"F0.wireOp",EDGE,"E0.8"),sQuery(id+"F0.wireOp",EDGE,"E0.9"),sQuery(id+"F0.wireOp",EDGE,"E0.10"),sQuery(id+"F0.wireOp",EDGE,"E0.11"),sQuery(id+"F0.wireOp",EDGE,"E0.12"),sQuery(id+"F0.wireOp",EDGE,"E0.13"),sQuery(id+"F0.wireOp",EDGE,"E0.14"),sQuery(id+"F0.wireOp",EDGE,"E0.15"),sQuery(id+"F0.wireOp",EDGE,"E1"),sQuery(id+"F0.wireOp",EDGE,"E2.1"),sQuery(id+"F0.wireOp",EDGE,"E2.3"),subQ1,sQuery(id+"F0.wireOp",EDGE,"E2.7"),sQuery(id+"F0.wireOp",EDGE,"E2.9"),sQuery(id+"F0.wireOp",EDGE,"E2.11"),sQuery(id+"F0.wireOp",EDGE,"E2.13"),sQuery(id+"F0.wireOp",EDGE,"E2.15"),sQuery(id+"F0.wireOp",EDGE,"E3.1"),sQuery(id+"F0.wireOp",EDGE,"E3.3"),sQuery(id+"F0.wireOp",EDGE,"E3.5"),sQuery(id+"F0.wireOp",EDGE,"E3.7"),sQuery(id+"F0.wireOp",EDGE,"E3.9"),sQuery(id+"F0.wireOp",EDGE,"E3.11"),sQuery(id+"F0.wireOp",EDGE,"E3.13"),sQuery(id+"F0.wireOp",EDGE,"E3.15"),sQuery(id+"F0.wireOp",EDGE,"E4"),sQuery(id+"F0.wireOp",EDGE,"E5"),sQuery(id+"F0.wireOp",EDGE,"E6"),sQuery(id+"F0.wireOp",EDGE,"E7"),sQuery(id+"F0.wireOp",EDGE,"E8"),sQuery(id+"F0.wireOp",EDGE,"E9"),sQuery(id+"F0.wireOp",EDGE,"E10"),sQuery(id+"F0.wireOp",EDGE,"E11"),sQuery(id+"F0.wireOp",EDGE,"E12"),subQ0,sQuery(id+"F0.wireOp",EDGE,"E14"),sQuery(id+"F0.wireOp",EDGE,"E15"),sQuery(id+"F0.wireOp",EDGE,"E16"),sQuery(id+"F0.wireOp",EDGE,"E17"),sQuery(id+"F0.wireOp",EDGE,"E18"),sQuery(id+"F0.wireOp",EDGE,"E19")])],"isStart":true})],"blendedInto":[makeQuery(id+"F1.opExtrude","CAP_FACE",FACE,{"disambiguationData":[OSD([sQuery(id+"F0.wireOp",EDGE,"E0.0"),sQuery(id+"F0.wireOp",EDGE,"E0.1"),sQuery(id+"F0.wireOp",EDGE,"E0.2"),sQuery(id+"F0.wireOp",EDGE,"E0.3"),sQuery(id+"F0.wireOp",EDGE,"E0.4"),sQuery(id+"F0.wireOp",EDGE,"E0.5"),sQuery(id+"F0.wireOp",EDGE,"E0.6"),sQuery(id+"F0.wireOp",EDGE,"E0.7"),sQuery(id+"F0.wireOp",EDGE,"E0.8"),sQuery(id+"F0.wireOp",EDGE,"E0.9"),sQuery(id+"F0.wireOp",EDGE,"E0.10"),sQuery(id+"F0.wireOp",EDGE,"E0.11"),sQuery(id+"F0.wireOp",EDGE,"E0.12"),sQuery(id+"F0.wireOp",EDGE,"E0.13"),sQuery(id+"F0.wireOp",EDGE,"E0.14"),sQuery(id+"F0.wireOp",EDGE,"E0.15"),sQuery(id+"F0.wireOp",EDGE,"E1"),sQuery(id+"F0.wireOp",EDGE,"E2.1"),sQuery(id+"F0.wireOp",EDGE,"E2.3"),subQ1,sQuery(id+"F0.wireOp",EDGE,"E2.7"),sQuery(id+"F0.wireOp",EDGE,"E2.9"),sQuery(id+"F0.wireOp",EDGE,"E2.11"),sQuery(id+"F0.wireOp",EDGE,"E2.13"),sQuery(id+"F0.wireOp",EDGE,"E2.15"),sQuery(id+"F0.wireOp",EDGE,"E3.1"),sQuery(id+"F0.wireOp",EDGE,"E3.3"),sQuery(id+"F0.wireOp",EDGE,"E3.5"),sQuery(id+"F0.wireOp",EDGE,"E3.7"),sQuery(id+"F0.wireOp",EDGE,"E3.9"),sQuery(id+"F0.wireOp",EDGE,"E3.11"),sQuery(id+"F0.wireOp",EDGE,"E3.13"),sQuery(id+"F0.wireOp",EDGE,"E3.15"),sQuery(id+"F0.wireOp",EDGE,"E4"),sQuery(id+"F0.wireOp",EDGE,"E5"),sQuery(id+"F0.wireOp",EDGE,"E6"),sQuery(id+"F0.wireOp",EDGE,"E7"),sQuery(id+"F0.wireOp",EDGE,"E8"),sQuery(id+"F0.wireOp",EDGE,"E9"),sQuery(id+"F0.wireOp",EDGE,"E10"),sQuery(id+"F0.wireOp",EDGE,"E11"),sQuery(id+"F0.wireOp",EDGE,"E12"),subQ0,sQuery(id+"F0.wireOp",EDGE,"E14"),sQuery(id+"F0.wireOp",EDGE,"E15"),sQuery(id+"F0.wireOp",EDGE,"E16"),sQuery(id+"F0.wireOp",EDGE,"E17"),sQuery(id+"F0.wireOp",EDGE,"E18"),sQuery(id+"F0.wireOp",EDGE,"E19")])],"isStart":true})]});}
            var Q38;
            {var subQ0=sQuery(id+"F0.wireOp",EDGE,"E13");var subQ1=sQuery(id+"F0.wireOp",EDGE,"E3.5");Q38=makeQuery(id+"F5.opChamfer","BLEND_EDGE",EDGE,{"blendedFrom":[makeQuery(id+"F1.opExtrude","SWEPT_EDGE",EDGE,{"disambiguationData":[OSD([sQuery(id+"F0.wireOp",EDGE,"E3.4"),subQ1,subQ0])]}),makeQuery(id+"F1.opExtrude","CAP_FACE",FACE,{"disambiguationData":[OSD([sQuery(id+"F0.wireOp",EDGE,"E0.0"),sQuery(id+"F0.wireOp",EDGE,"E0.1"),sQuery(id+"F0.wireOp",EDGE,"E0.2"),sQuery(id+"F0.wireOp",EDGE,"E0.3"),sQuery(id+"F0.wireOp",EDGE,"E0.4"),sQuery(id+"F0.wireOp",EDGE,"E0.5"),sQuery(id+"F0.wireOp",EDGE,"E0.6"),sQuery(id+"F0.wireOp",EDGE,"E0.7"),sQuery(id+"F0.wireOp",EDGE,"E0.8"),sQuery(id+"F0.wireOp",EDGE,"E0.9"),sQuery(id+"F0.wireOp",EDGE,"E0.10"),sQuery(id+"F0.wireOp",EDGE,"E0.11"),sQuery(id+"F0.wireOp",EDGE,"E0.12"),sQuery(id+"F0.wireOp",EDGE,"E0.13"),sQuery(id+"F0.wireOp",EDGE,"E0.14"),sQuery(id+"F0.wireOp",EDGE,"E0.15"),sQuery(id+"F0.wireOp",EDGE,"E1"),sQuery(id+"F0.wireOp",EDGE,"E2.1"),sQuery(id+"F0.wireOp",EDGE,"E2.3"),sQuery(id+"F0.wireOp",EDGE,"E2.5"),sQuery(id+"F0.wireOp",EDGE,"E2.7"),sQuery(id+"F0.wireOp",EDGE,"E2.9"),sQuery(id+"F0.wireOp",EDGE,"E2.11"),sQuery(id+"F0.wireOp",EDGE,"E2.13"),sQuery(id+"F0.wireOp",EDGE,"E2.15"),sQuery(id+"F0.wireOp",EDGE,"E3.1"),sQuery(id+"F0.wireOp",EDGE,"E3.3"),subQ1,sQuery(id+"F0.wireOp",EDGE,"E3.7"),sQuery(id+"F0.wireOp",EDGE,"E3.9"),sQuery(id+"F0.wireOp",EDGE,"E3.11"),sQuery(id+"F0.wireOp",EDGE,"E3.13"),sQuery(id+"F0.wireOp",EDGE,"E3.15"),sQuery(id+"F0.wireOp",EDGE,"E4"),sQuery(id+"F0.wireOp",EDGE,"E5"),sQuery(id+"F0.wireOp",EDGE,"E6"),sQuery(id+"F0.wireOp",EDGE,"E7"),sQuery(id+"F0.wireOp",EDGE,"E8"),sQuery(id+"F0.wireOp",EDGE,"E9"),sQuery(id+"F0.wireOp",EDGE,"E10"),sQuery(id+"F0.wireOp",EDGE,"E11"),sQuery(id+"F0.wireOp",EDGE,"E12"),subQ0,sQuery(id+"F0.wireOp",EDGE,"E14"),sQuery(id+"F0.wireOp",EDGE,"E15"),sQuery(id+"F0.wireOp",EDGE,"E16"),sQuery(id+"F0.wireOp",EDGE,"E17"),sQuery(id+"F0.wireOp",EDGE,"E18"),sQuery(id+"F0.wireOp",EDGE,"E19")])],"isStart":true})],"blendedInto":[makeQuery(id+"F1.opExtrude","CAP_FACE",FACE,{"disambiguationData":[OSD([sQuery(id+"F0.wireOp",EDGE,"E0.0"),sQuery(id+"F0.wireOp",EDGE,"E0.1"),sQuery(id+"F0.wireOp",EDGE,"E0.2"),sQuery(id+"F0.wireOp",EDGE,"E0.3"),sQuery(id+"F0.wireOp",EDGE,"E0.4"),sQuery(id+"F0.wireOp",EDGE,"E0.5"),sQuery(id+"F0.wireOp",EDGE,"E0.6"),sQuery(id+"F0.wireOp",EDGE,"E0.7"),sQuery(id+"F0.wireOp",EDGE,"E0.8"),sQuery(id+"F0.wireOp",EDGE,"E0.9"),sQuery(id+"F0.wireOp",EDGE,"E0.10"),sQuery(id+"F0.wireOp",EDGE,"E0.11"),sQuery(id+"F0.wireOp",EDGE,"E0.12"),sQuery(id+"F0.wireOp",EDGE,"E0.13"),sQuery(id+"F0.wireOp",EDGE,"E0.14"),sQuery(id+"F0.wireOp",EDGE,"E0.15"),sQuery(id+"F0.wireOp",EDGE,"E1"),sQuery(id+"F0.wireOp",EDGE,"E2.1"),sQuery(id+"F0.wireOp",EDGE,"E2.3"),sQuery(id+"F0.wireOp",EDGE,"E2.5"),sQuery(id+"F0.wireOp",EDGE,"E2.7"),sQuery(id+"F0.wireOp",EDGE,"E2.9"),sQuery(id+"F0.wireOp",EDGE,"E2.11"),sQuery(id+"F0.wireOp",EDGE,"E2.13"),sQuery(id+"F0.wireOp",EDGE,"E2.15"),sQuery(id+"F0.wireOp",EDGE,"E3.1"),sQuery(id+"F0.wireOp",EDGE,"E3.3"),subQ1,sQuery(id+"F0.wireOp",EDGE,"E3.7"),sQuery(id+"F0.wireOp",EDGE,"E3.9"),sQuery(id+"F0.wireOp",EDGE,"E3.11"),sQuery(id+"F0.wireOp",EDGE,"E3.13"),sQuery(id+"F0.wireOp",EDGE,"E3.15"),sQuery(id+"F0.wireOp",EDGE,"E4"),sQuery(id+"F0.wireOp",EDGE,"E5"),sQuery(id+"F0.wireOp",EDGE,"E6"),sQuery(id+"F0.wireOp",EDGE,"E7"),sQuery(id+"F0.wireOp",EDGE,"E8"),sQuery(id+"F0.wireOp",EDGE,"E9"),sQuery(id+"F0.wireOp",EDGE,"E10"),sQuery(id+"F0.wireOp",EDGE,"E11"),sQuery(id+"F0.wireOp",EDGE,"E12"),subQ0,sQuery(id+"F0.wireOp",EDGE,"E14"),sQuery(id+"F0.wireOp",EDGE,"E15"),sQuery(id+"F0.wireOp",EDGE,"E16"),sQuery(id+"F0.wireOp",EDGE,"E17"),sQuery(id+"F0.wireOp",EDGE,"E18"),sQuery(id+"F0.wireOp",EDGE,"E19")])],"isStart":true})]});}
            var Q39;
            {var subQ0=sQuery(id+"F0.wireOp",EDGE,"E14");var subQ1=sQuery(id+"F0.wireOp",EDGE,"E3.5");Q39=makeQuery(id+"F5.opChamfer","BLEND_EDGE",EDGE,{"blendedFrom":[makeQuery(id+"F1.opExtrude","SWEPT_EDGE",EDGE,{"disambiguationData":[OSD([subQ1,sQuery(id+"F0.wireOp",EDGE,"E3.6"),subQ0])]}),makeQuery(id+"F1.opExtrude","CAP_FACE",FACE,{"disambiguationData":[OSD([sQuery(id+"F0.wireOp",EDGE,"E0.0"),sQuery(id+"F0.wireOp",EDGE,"E0.1"),sQuery(id+"F0.wireOp",EDGE,"E0.2"),sQuery(id+"F0.wireOp",EDGE,"E0.3"),sQuery(id+"F0.wireOp",EDGE,"E0.4"),sQuery(id+"F0.wireOp",EDGE,"E0.5"),sQuery(id+"F0.wireOp",EDGE,"E0.6"),sQuery(id+"F0.wireOp",EDGE,"E0.7"),sQuery(id+"F0.wireOp",EDGE,"E0.8"),sQuery(id+"F0.wireOp",EDGE,"E0.9"),sQuery(id+"F0.wireOp",EDGE,"E0.10"),sQuery(id+"F0.wireOp",EDGE,"E0.11"),sQuery(id+"F0.wireOp",EDGE,"E0.12"),sQuery(id+"F0.wireOp",EDGE,"E0.13"),sQuery(id+"F0.wireOp",EDGE,"E0.14"),sQuery(id+"F0.wireOp",EDGE,"E0.15"),sQuery(id+"F0.wireOp",EDGE,"E1"),sQuery(id+"F0.wireOp",EDGE,"E2.1"),sQuery(id+"F0.wireOp",EDGE,"E2.3"),sQuery(id+"F0.wireOp",EDGE,"E2.5"),sQuery(id+"F0.wireOp",EDGE,"E2.7"),sQuery(id+"F0.wireOp",EDGE,"E2.9"),sQuery(id+"F0.wireOp",EDGE,"E2.11"),sQuery(id+"F0.wireOp",EDGE,"E2.13"),sQuery(id+"F0.wireOp",EDGE,"E2.15"),sQuery(id+"F0.wireOp",EDGE,"E3.1"),sQuery(id+"F0.wireOp",EDGE,"E3.3"),subQ1,sQuery(id+"F0.wireOp",EDGE,"E3.7"),sQuery(id+"F0.wireOp",EDGE,"E3.9"),sQuery(id+"F0.wireOp",EDGE,"E3.11"),sQuery(id+"F0.wireOp",EDGE,"E3.13"),sQuery(id+"F0.wireOp",EDGE,"E3.15"),sQuery(id+"F0.wireOp",EDGE,"E4"),sQuery(id+"F0.wireOp",EDGE,"E5"),sQuery(id+"F0.wireOp",EDGE,"E6"),sQuery(id+"F0.wireOp",EDGE,"E7"),sQuery(id+"F0.wireOp",EDGE,"E8"),sQuery(id+"F0.wireOp",EDGE,"E9"),sQuery(id+"F0.wireOp",EDGE,"E10"),sQuery(id+"F0.wireOp",EDGE,"E11"),sQuery(id+"F0.wireOp",EDGE,"E12"),sQuery(id+"F0.wireOp",EDGE,"E13"),subQ0,sQuery(id+"F0.wireOp",EDGE,"E15"),sQuery(id+"F0.wireOp",EDGE,"E16"),sQuery(id+"F0.wireOp",EDGE,"E17"),sQuery(id+"F0.wireOp",EDGE,"E18"),sQuery(id+"F0.wireOp",EDGE,"E19")])],"isStart":true})],"blendedInto":[makeQuery(id+"F1.opExtrude","CAP_FACE",FACE,{"disambiguationData":[OSD([sQuery(id+"F0.wireOp",EDGE,"E0.0"),sQuery(id+"F0.wireOp",EDGE,"E0.1"),sQuery(id+"F0.wireOp",EDGE,"E0.2"),sQuery(id+"F0.wireOp",EDGE,"E0.3"),sQuery(id+"F0.wireOp",EDGE,"E0.4"),sQuery(id+"F0.wireOp",EDGE,"E0.5"),sQuery(id+"F0.wireOp",EDGE,"E0.6"),sQuery(id+"F0.wireOp",EDGE,"E0.7"),sQuery(id+"F0.wireOp",EDGE,"E0.8"),sQuery(id+"F0.wireOp",EDGE,"E0.9"),sQuery(id+"F0.wireOp",EDGE,"E0.10"),sQuery(id+"F0.wireOp",EDGE,"E0.11"),sQuery(id+"F0.wireOp",EDGE,"E0.12"),sQuery(id+"F0.wireOp",EDGE,"E0.13"),sQuery(id+"F0.wireOp",EDGE,"E0.14"),sQuery(id+"F0.wireOp",EDGE,"E0.15"),sQuery(id+"F0.wireOp",EDGE,"E1"),sQuery(id+"F0.wireOp",EDGE,"E2.1"),sQuery(id+"F0.wireOp",EDGE,"E2.3"),sQuery(id+"F0.wireOp",EDGE,"E2.5"),sQuery(id+"F0.wireOp",EDGE,"E2.7"),sQuery(id+"F0.wireOp",EDGE,"E2.9"),sQuery(id+"F0.wireOp",EDGE,"E2.11"),sQuery(id+"F0.wireOp",EDGE,"E2.13"),sQuery(id+"F0.wireOp",EDGE,"E2.15"),sQuery(id+"F0.wireOp",EDGE,"E3.1"),sQuery(id+"F0.wireOp",EDGE,"E3.3"),subQ1,sQuery(id+"F0.wireOp",EDGE,"E3.7"),sQuery(id+"F0.wireOp",EDGE,"E3.9"),sQuery(id+"F0.wireOp",EDGE,"E3.11"),sQuery(id+"F0.wireOp",EDGE,"E3.13"),sQuery(id+"F0.wireOp",EDGE,"E3.15"),sQuery(id+"F0.wireOp",EDGE,"E4"),sQuery(id+"F0.wireOp",EDGE,"E5"),sQuery(id+"F0.wireOp",EDGE,"E6"),sQuery(id+"F0.wireOp",EDGE,"E7"),sQuery(id+"F0.wireOp",EDGE,"E8"),sQuery(id+"F0.wireOp",EDGE,"E9"),sQuery(id+"F0.wireOp",EDGE,"E10"),sQuery(id+"F0.wireOp",EDGE,"E11"),sQuery(id+"F0.wireOp",EDGE,"E12"),sQuery(id+"F0.wireOp",EDGE,"E13"),subQ0,sQuery(id+"F0.wireOp",EDGE,"E15"),sQuery(id+"F0.wireOp",EDGE,"E16"),sQuery(id+"F0.wireOp",EDGE,"E17"),sQuery(id+"F0.wireOp",EDGE,"E18"),sQuery(id+"F0.wireOp",EDGE,"E19")])],"isStart":true})]});}
            var Q40;
            Q40=makeQuery(id+"F1.opExtrude","CAP_EDGE",EDGE,{"disambiguationData":[OSD([sQuery(id+"F0.wireOp",EDGE,"E3.3")])],"isStart":true});
            var Q41;
            {var subQ0=sQuery(id+"F0.wireOp",EDGE,"E12");var subQ1=sQuery(id+"F0.wireOp",EDGE,"E3.3");Q41=makeQuery(id+"F5.opChamfer","BLEND_EDGE",EDGE,{"blendedFrom":[makeQuery(id+"F1.opExtrude","SWEPT_EDGE",EDGE,{"disambiguationData":[OSD([subQ1,sQuery(id+"F0.wireOp",EDGE,"E3.4"),subQ0])]}),makeQuery(id+"F1.opExtrude","CAP_FACE",FACE,{"disambiguationData":[OSD([sQuery(id+"F0.wireOp",EDGE,"E0.0"),sQuery(id+"F0.wireOp",EDGE,"E0.1"),sQuery(id+"F0.wireOp",EDGE,"E0.2"),sQuery(id+"F0.wireOp",EDGE,"E0.3"),sQuery(id+"F0.wireOp",EDGE,"E0.4"),sQuery(id+"F0.wireOp",EDGE,"E0.5"),sQuery(id+"F0.wireOp",EDGE,"E0.6"),sQuery(id+"F0.wireOp",EDGE,"E0.7"),sQuery(id+"F0.wireOp",EDGE,"E0.8"),sQuery(id+"F0.wireOp",EDGE,"E0.9"),sQuery(id+"F0.wireOp",EDGE,"E0.10"),sQuery(id+"F0.wireOp",EDGE,"E0.11"),sQuery(id+"F0.wireOp",EDGE,"E0.12"),sQuery(id+"F0.wireOp",EDGE,"E0.13"),sQuery(id+"F0.wireOp",EDGE,"E0.14"),sQuery(id+"F0.wireOp",EDGE,"E0.15"),sQuery(id+"F0.wireOp",EDGE,"E1"),sQuery(id+"F0.wireOp",EDGE,"E2.1"),sQuery(id+"F0.wireOp",EDGE,"E2.3"),sQuery(id+"F0.wireOp",EDGE,"E2.5"),sQuery(id+"F0.wireOp",EDGE,"E2.7"),sQuery(id+"F0.wireOp",EDGE,"E2.9"),sQuery(id+"F0.wireOp",EDGE,"E2.11"),sQuery(id+"F0.wireOp",EDGE,"E2.13"),sQuery(id+"F0.wireOp",EDGE,"E2.15"),sQuery(id+"F0.wireOp",EDGE,"E3.1"),subQ1,sQuery(id+"F0.wireOp",EDGE,"E3.5"),sQuery(id+"F0.wireOp",EDGE,"E3.7"),sQuery(id+"F0.wireOp",EDGE,"E3.9"),sQuery(id+"F0.wireOp",EDGE,"E3.11"),sQuery(id+"F0.wireOp",EDGE,"E3.13"),sQuery(id+"F0.wireOp",EDGE,"E3.15"),sQuery(id+"F0.wireOp",EDGE,"E4"),sQuery(id+"F0.wireOp",EDGE,"E5"),sQuery(id+"F0.wireOp",EDGE,"E6"),sQuery(id+"F0.wireOp",EDGE,"E7"),sQuery(id+"F0.wireOp",EDGE,"E8"),sQuery(id+"F0.wireOp",EDGE,"E9"),sQuery(id+"F0.wireOp",EDGE,"E10"),sQuery(id+"F0.wireOp",EDGE,"E11"),subQ0,sQuery(id+"F0.wireOp",EDGE,"E13"),sQuery(id+"F0.wireOp",EDGE,"E14"),sQuery(id+"F0.wireOp",EDGE,"E15"),sQuery(id+"F0.wireOp",EDGE,"E16"),sQuery(id+"F0.wireOp",EDGE,"E17"),sQuery(id+"F0.wireOp",EDGE,"E18"),sQuery(id+"F0.wireOp",EDGE,"E19")])],"isStart":true})],"blendedInto":[makeQuery(id+"F1.opExtrude","CAP_FACE",FACE,{"disambiguationData":[OSD([sQuery(id+"F0.wireOp",EDGE,"E0.0"),sQuery(id+"F0.wireOp",EDGE,"E0.1"),sQuery(id+"F0.wireOp",EDGE,"E0.2"),sQuery(id+"F0.wireOp",EDGE,"E0.3"),sQuery(id+"F0.wireOp",EDGE,"E0.4"),sQuery(id+"F0.wireOp",EDGE,"E0.5"),sQuery(id+"F0.wireOp",EDGE,"E0.6"),sQuery(id+"F0.wireOp",EDGE,"E0.7"),sQuery(id+"F0.wireOp",EDGE,"E0.8"),sQuery(id+"F0.wireOp",EDGE,"E0.9"),sQuery(id+"F0.wireOp",EDGE,"E0.10"),sQuery(id+"F0.wireOp",EDGE,"E0.11"),sQuery(id+"F0.wireOp",EDGE,"E0.12"),sQuery(id+"F0.wireOp",EDGE,"E0.13"),sQuery(id+"F0.wireOp",EDGE,"E0.14"),sQuery(id+"F0.wireOp",EDGE,"E0.15"),sQuery(id+"F0.wireOp",EDGE,"E1"),sQuery(id+"F0.wireOp",EDGE,"E2.1"),sQuery(id+"F0.wireOp",EDGE,"E2.3"),sQuery(id+"F0.wireOp",EDGE,"E2.5"),sQuery(id+"F0.wireOp",EDGE,"E2.7"),sQuery(id+"F0.wireOp",EDGE,"E2.9"),sQuery(id+"F0.wireOp",EDGE,"E2.11"),sQuery(id+"F0.wireOp",EDGE,"E2.13"),sQuery(id+"F0.wireOp",EDGE,"E2.15"),sQuery(id+"F0.wireOp",EDGE,"E3.1"),subQ1,sQuery(id+"F0.wireOp",EDGE,"E3.5"),sQuery(id+"F0.wireOp",EDGE,"E3.7"),sQuery(id+"F0.wireOp",EDGE,"E3.9"),sQuery(id+"F0.wireOp",EDGE,"E3.11"),sQuery(id+"F0.wireOp",EDGE,"E3.13"),sQuery(id+"F0.wireOp",EDGE,"E3.15"),sQuery(id+"F0.wireOp",EDGE,"E4"),sQuery(id+"F0.wireOp",EDGE,"E5"),sQuery(id+"F0.wireOp",EDGE,"E6"),sQuery(id+"F0.wireOp",EDGE,"E7"),sQuery(id+"F0.wireOp",EDGE,"E8"),sQuery(id+"F0.wireOp",EDGE,"E9"),sQuery(id+"F0.wireOp",EDGE,"E10"),sQuery(id+"F0.wireOp",EDGE,"E11"),subQ0,sQuery(id+"F0.wireOp",EDGE,"E13"),sQuery(id+"F0.wireOp",EDGE,"E14"),sQuery(id+"F0.wireOp",EDGE,"E15"),sQuery(id+"F0.wireOp",EDGE,"E16"),sQuery(id+"F0.wireOp",EDGE,"E17"),sQuery(id+"F0.wireOp",EDGE,"E18"),sQuery(id+"F0.wireOp",EDGE,"E19")])],"isStart":true})]});}
            var Q42;
            Q42=makeQuery(id+"F1.opExtrude","CAP_EDGE",EDGE,{"disambiguationData":[OSD([sQuery(id+"F0.wireOp",EDGE,"E12")])],"isStart":true});
            var Q43;
            {var subQ0=sQuery(id+"F0.wireOp",EDGE,"E12");var subQ1=sQuery(id+"F0.wireOp",EDGE,"E2.3");Q43=makeQuery(id+"F5.opChamfer","BLEND_EDGE",EDGE,{"blendedFrom":[makeQuery(id+"F1.opExtrude","SWEPT_EDGE",EDGE,{"disambiguationData":[OSD([subQ1,sQuery(id+"F0.wireOp",EDGE,"E2.4"),subQ0])]}),makeQuery(id+"F1.opExtrude","CAP_FACE",FACE,{"disambiguationData":[OSD([sQuery(id+"F0.wireOp",EDGE,"E0.0"),sQuery(id+"F0.wireOp",EDGE,"E0.1"),sQuery(id+"F0.wireOp",EDGE,"E0.2"),sQuery(id+"F0.wireOp",EDGE,"E0.3"),sQuery(id+"F0.wireOp",EDGE,"E0.4"),sQuery(id+"F0.wireOp",EDGE,"E0.5"),sQuery(id+"F0.wireOp",EDGE,"E0.6"),sQuery(id+"F0.wireOp",EDGE,"E0.7"),sQuery(id+"F0.wireOp",EDGE,"E0.8"),sQuery(id+"F0.wireOp",EDGE,"E0.9"),sQuery(id+"F0.wireOp",EDGE,"E0.10"),sQuery(id+"F0.wireOp",EDGE,"E0.11"),sQuery(id+"F0.wireOp",EDGE,"E0.12"),sQuery(id+"F0.wireOp",EDGE,"E0.13"),sQuery(id+"F0.wireOp",EDGE,"E0.14"),sQuery(id+"F0.wireOp",EDGE,"E0.15"),sQuery(id+"F0.wireOp",EDGE,"E1"),sQuery(id+"F0.wireOp",EDGE,"E2.1"),subQ1,sQuery(id+"F0.wireOp",EDGE,"E2.5"),sQuery(id+"F0.wireOp",EDGE,"E2.7"),sQuery(id+"F0.wireOp",EDGE,"E2.9"),sQuery(id+"F0.wireOp",EDGE,"E2.11"),sQuery(id+"F0.wireOp",EDGE,"E2.13"),sQuery(id+"F0.wireOp",EDGE,"E2.15"),sQuery(id+"F0.wireOp",EDGE,"E3.1"),sQuery(id+"F0.wireOp",EDGE,"E3.3"),sQuery(id+"F0.wireOp",EDGE,"E3.5"),sQuery(id+"F0.wireOp",EDGE,"E3.7"),sQuery(id+"F0.wireOp",EDGE,"E3.9"),sQuery(id+"F0.wireOp",EDGE,"E3.11"),sQuery(id+"F0.wireOp",EDGE,"E3.13"),sQuery(id+"F0.wireOp",EDGE,"E3.15"),sQuery(id+"F0.wireOp",EDGE,"E4"),sQuery(id+"F0.wireOp",EDGE,"E5"),sQuery(id+"F0.wireOp",EDGE,"E6"),sQuery(id+"F0.wireOp",EDGE,"E7"),sQuery(id+"F0.wireOp",EDGE,"E8"),sQuery(id+"F0.wireOp",EDGE,"E9"),sQuery(id+"F0.wireOp",EDGE,"E10"),sQuery(id+"F0.wireOp",EDGE,"E11"),subQ0,sQuery(id+"F0.wireOp",EDGE,"E13"),sQuery(id+"F0.wireOp",EDGE,"E14"),sQuery(id+"F0.wireOp",EDGE,"E15"),sQuery(id+"F0.wireOp",EDGE,"E16"),sQuery(id+"F0.wireOp",EDGE,"E17"),sQuery(id+"F0.wireOp",EDGE,"E18"),sQuery(id+"F0.wireOp",EDGE,"E19")])],"isStart":true})],"blendedInto":[makeQuery(id+"F1.opExtrude","CAP_FACE",FACE,{"disambiguationData":[OSD([sQuery(id+"F0.wireOp",EDGE,"E0.0"),sQuery(id+"F0.wireOp",EDGE,"E0.1"),sQuery(id+"F0.wireOp",EDGE,"E0.2"),sQuery(id+"F0.wireOp",EDGE,"E0.3"),sQuery(id+"F0.wireOp",EDGE,"E0.4"),sQuery(id+"F0.wireOp",EDGE,"E0.5"),sQuery(id+"F0.wireOp",EDGE,"E0.6"),sQuery(id+"F0.wireOp",EDGE,"E0.7"),sQuery(id+"F0.wireOp",EDGE,"E0.8"),sQuery(id+"F0.wireOp",EDGE,"E0.9"),sQuery(id+"F0.wireOp",EDGE,"E0.10"),sQuery(id+"F0.wireOp",EDGE,"E0.11"),sQuery(id+"F0.wireOp",EDGE,"E0.12"),sQuery(id+"F0.wireOp",EDGE,"E0.13"),sQuery(id+"F0.wireOp",EDGE,"E0.14"),sQuery(id+"F0.wireOp",EDGE,"E0.15"),sQuery(id+"F0.wireOp",EDGE,"E1"),sQuery(id+"F0.wireOp",EDGE,"E2.1"),subQ1,sQuery(id+"F0.wireOp",EDGE,"E2.5"),sQuery(id+"F0.wireOp",EDGE,"E2.7"),sQuery(id+"F0.wireOp",EDGE,"E2.9"),sQuery(id+"F0.wireOp",EDGE,"E2.11"),sQuery(id+"F0.wireOp",EDGE,"E2.13"),sQuery(id+"F0.wireOp",EDGE,"E2.15"),sQuery(id+"F0.wireOp",EDGE,"E3.1"),sQuery(id+"F0.wireOp",EDGE,"E3.3"),sQuery(id+"F0.wireOp",EDGE,"E3.5"),sQuery(id+"F0.wireOp",EDGE,"E3.7"),sQuery(id+"F0.wireOp",EDGE,"E3.9"),sQuery(id+"F0.wireOp",EDGE,"E3.11"),sQuery(id+"F0.wireOp",EDGE,"E3.13"),sQuery(id+"F0.wireOp",EDGE,"E3.15"),sQuery(id+"F0.wireOp",EDGE,"E4"),sQuery(id+"F0.wireOp",EDGE,"E5"),sQuery(id+"F0.wireOp",EDGE,"E6"),sQuery(id+"F0.wireOp",EDGE,"E7"),sQuery(id+"F0.wireOp",EDGE,"E8"),sQuery(id+"F0.wireOp",EDGE,"E9"),sQuery(id+"F0.wireOp",EDGE,"E10"),sQuery(id+"F0.wireOp",EDGE,"E11"),subQ0,sQuery(id+"F0.wireOp",EDGE,"E13"),sQuery(id+"F0.wireOp",EDGE,"E14"),sQuery(id+"F0.wireOp",EDGE,"E15"),sQuery(id+"F0.wireOp",EDGE,"E16"),sQuery(id+"F0.wireOp",EDGE,"E17"),sQuery(id+"F0.wireOp",EDGE,"E18"),sQuery(id+"F0.wireOp",EDGE,"E19")])],"isStart":true})]});}
            var Q44;
            Q44=makeQuery(id+"F1.opExtrude","CAP_EDGE",EDGE,{"disambiguationData":[OSD([sQuery(id+"F0.wireOp",EDGE,"E2.3")])],"isStart":true});
            var Q45;
            {var subQ0=sQuery(id+"F0.wireOp",EDGE,"E11");var subQ1=sQuery(id+"F0.wireOp",EDGE,"E2.3");Q45=makeQuery(id+"F5.opChamfer","BLEND_EDGE",EDGE,{"blendedFrom":[makeQuery(id+"F1.opExtrude","SWEPT_EDGE",EDGE,{"disambiguationData":[OSD([sQuery(id+"F0.wireOp",EDGE,"E2.2"),subQ1,subQ0])]}),makeQuery(id+"F1.opExtrude","CAP_FACE",FACE,{"disambiguationData":[OSD([sQuery(id+"F0.wireOp",EDGE,"E0.0"),sQuery(id+"F0.wireOp",EDGE,"E0.1"),sQuery(id+"F0.wireOp",EDGE,"E0.2"),sQuery(id+"F0.wireOp",EDGE,"E0.3"),sQuery(id+"F0.wireOp",EDGE,"E0.4"),sQuery(id+"F0.wireOp",EDGE,"E0.5"),sQuery(id+"F0.wireOp",EDGE,"E0.6"),sQuery(id+"F0.wireOp",EDGE,"E0.7"),sQuery(id+"F0.wireOp",EDGE,"E0.8"),sQuery(id+"F0.wireOp",EDGE,"E0.9"),sQuery(id+"F0.wireOp",EDGE,"E0.10"),sQuery(id+"F0.wireOp",EDGE,"E0.11"),sQuery(id+"F0.wireOp",EDGE,"E0.12"),sQuery(id+"F0.wireOp",EDGE,"E0.13"),sQuery(id+"F0.wireOp",EDGE,"E0.14"),sQuery(id+"F0.wireOp",EDGE,"E0.15"),sQuery(id+"F0.wireOp",EDGE,"E1"),sQuery(id+"F0.wireOp",EDGE,"E2.1"),subQ1,sQuery(id+"F0.wireOp",EDGE,"E2.5"),sQuery(id+"F0.wireOp",EDGE,"E2.7"),sQuery(id+"F0.wireOp",EDGE,"E2.9"),sQuery(id+"F0.wireOp",EDGE,"E2.11"),sQuery(id+"F0.wireOp",EDGE,"E2.13"),sQuery(id+"F0.wireOp",EDGE,"E2.15"),sQuery(id+"F0.wireOp",EDGE,"E3.1"),sQuery(id+"F0.wireOp",EDGE,"E3.3"),sQuery(id+"F0.wireOp",EDGE,"E3.5"),sQuery(id+"F0.wireOp",EDGE,"E3.7"),sQuery(id+"F0.wireOp",EDGE,"E3.9"),sQuery(id+"F0.wireOp",EDGE,"E3.11"),sQuery(id+"F0.wireOp",EDGE,"E3.13"),sQuery(id+"F0.wireOp",EDGE,"E3.15"),sQuery(id+"F0.wireOp",EDGE,"E4"),sQuery(id+"F0.wireOp",EDGE,"E5"),sQuery(id+"F0.wireOp",EDGE,"E6"),sQuery(id+"F0.wireOp",EDGE,"E7"),sQuery(id+"F0.wireOp",EDGE,"E8"),sQuery(id+"F0.wireOp",EDGE,"E9"),sQuery(id+"F0.wireOp",EDGE,"E10"),subQ0,sQuery(id+"F0.wireOp",EDGE,"E12"),sQuery(id+"F0.wireOp",EDGE,"E13"),sQuery(id+"F0.wireOp",EDGE,"E14"),sQuery(id+"F0.wireOp",EDGE,"E15"),sQuery(id+"F0.wireOp",EDGE,"E16"),sQuery(id+"F0.wireOp",EDGE,"E17"),sQuery(id+"F0.wireOp",EDGE,"E18"),sQuery(id+"F0.wireOp",EDGE,"E19")])],"isStart":true})],"blendedInto":[makeQuery(id+"F1.opExtrude","CAP_FACE",FACE,{"disambiguationData":[OSD([sQuery(id+"F0.wireOp",EDGE,"E0.0"),sQuery(id+"F0.wireOp",EDGE,"E0.1"),sQuery(id+"F0.wireOp",EDGE,"E0.2"),sQuery(id+"F0.wireOp",EDGE,"E0.3"),sQuery(id+"F0.wireOp",EDGE,"E0.4"),sQuery(id+"F0.wireOp",EDGE,"E0.5"),sQuery(id+"F0.wireOp",EDGE,"E0.6"),sQuery(id+"F0.wireOp",EDGE,"E0.7"),sQuery(id+"F0.wireOp",EDGE,"E0.8"),sQuery(id+"F0.wireOp",EDGE,"E0.9"),sQuery(id+"F0.wireOp",EDGE,"E0.10"),sQuery(id+"F0.wireOp",EDGE,"E0.11"),sQuery(id+"F0.wireOp",EDGE,"E0.12"),sQuery(id+"F0.wireOp",EDGE,"E0.13"),sQuery(id+"F0.wireOp",EDGE,"E0.14"),sQuery(id+"F0.wireOp",EDGE,"E0.15"),sQuery(id+"F0.wireOp",EDGE,"E1"),sQuery(id+"F0.wireOp",EDGE,"E2.1"),subQ1,sQuery(id+"F0.wireOp",EDGE,"E2.5"),sQuery(id+"F0.wireOp",EDGE,"E2.7"),sQuery(id+"F0.wireOp",EDGE,"E2.9"),sQuery(id+"F0.wireOp",EDGE,"E2.11"),sQuery(id+"F0.wireOp",EDGE,"E2.13"),sQuery(id+"F0.wireOp",EDGE,"E2.15"),sQuery(id+"F0.wireOp",EDGE,"E3.1"),sQuery(id+"F0.wireOp",EDGE,"E3.3"),sQuery(id+"F0.wireOp",EDGE,"E3.5"),sQuery(id+"F0.wireOp",EDGE,"E3.7"),sQuery(id+"F0.wireOp",EDGE,"E3.9"),sQuery(id+"F0.wireOp",EDGE,"E3.11"),sQuery(id+"F0.wireOp",EDGE,"E3.13"),sQuery(id+"F0.wireOp",EDGE,"E3.15"),sQuery(id+"F0.wireOp",EDGE,"E4"),sQuery(id+"F0.wireOp",EDGE,"E5"),sQuery(id+"F0.wireOp",EDGE,"E6"),sQuery(id+"F0.wireOp",EDGE,"E7"),sQuery(id+"F0.wireOp",EDGE,"E8"),sQuery(id+"F0.wireOp",EDGE,"E9"),sQuery(id+"F0.wireOp",EDGE,"E10"),subQ0,sQuery(id+"F0.wireOp",EDGE,"E12"),sQuery(id+"F0.wireOp",EDGE,"E13"),sQuery(id+"F0.wireOp",EDGE,"E14"),sQuery(id+"F0.wireOp",EDGE,"E15"),sQuery(id+"F0.wireOp",EDGE,"E16"),sQuery(id+"F0.wireOp",EDGE,"E17"),sQuery(id+"F0.wireOp",EDGE,"E18"),sQuery(id+"F0.wireOp",EDGE,"E19")])],"isStart":true})]});}
            var Q46;
            Q46=makeQuery(id+"F1.opExtrude","CAP_EDGE",EDGE,{"disambiguationData":[OSD([sQuery(id+"F0.wireOp",EDGE,"E11")])],"isStart":true});
            var Q47;
            {var subQ0=sQuery(id+"F0.wireOp",EDGE,"E11");var subQ1=sQuery(id+"F0.wireOp",EDGE,"E3.3");Q47=makeQuery(id+"F5.opChamfer","BLEND_EDGE",EDGE,{"blendedFrom":[makeQuery(id+"F1.opExtrude","SWEPT_EDGE",EDGE,{"disambiguationData":[OSD([sQuery(id+"F0.wireOp",EDGE,"E3.2"),subQ1,subQ0])]}),makeQuery(id+"F1.opExtrude","CAP_FACE",FACE,{"disambiguationData":[OSD([sQuery(id+"F0.wireOp",EDGE,"E0.0"),sQuery(id+"F0.wireOp",EDGE,"E0.1"),sQuery(id+"F0.wireOp",EDGE,"E0.2"),sQuery(id+"F0.wireOp",EDGE,"E0.3"),sQuery(id+"F0.wireOp",EDGE,"E0.4"),sQuery(id+"F0.wireOp",EDGE,"E0.5"),sQuery(id+"F0.wireOp",EDGE,"E0.6"),sQuery(id+"F0.wireOp",EDGE,"E0.7"),sQuery(id+"F0.wireOp",EDGE,"E0.8"),sQuery(id+"F0.wireOp",EDGE,"E0.9"),sQuery(id+"F0.wireOp",EDGE,"E0.10"),sQuery(id+"F0.wireOp",EDGE,"E0.11"),sQuery(id+"F0.wireOp",EDGE,"E0.12"),sQuery(id+"F0.wireOp",EDGE,"E0.13"),sQuery(id+"F0.wireOp",EDGE,"E0.14"),sQuery(id+"F0.wireOp",EDGE,"E0.15"),sQuery(id+"F0.wireOp",EDGE,"E1"),sQuery(id+"F0.wireOp",EDGE,"E2.1"),sQuery(id+"F0.wireOp",EDGE,"E2.3"),sQuery(id+"F0.wireOp",EDGE,"E2.5"),sQuery(id+"F0.wireOp",EDGE,"E2.7"),sQuery(id+"F0.wireOp",EDGE,"E2.9"),sQuery(id+"F0.wireOp",EDGE,"E2.11"),sQuery(id+"F0.wireOp",EDGE,"E2.13"),sQuery(id+"F0.wireOp",EDGE,"E2.15"),sQuery(id+"F0.wireOp",EDGE,"E3.1"),subQ1,sQuery(id+"F0.wireOp",EDGE,"E3.5"),sQuery(id+"F0.wireOp",EDGE,"E3.7"),sQuery(id+"F0.wireOp",EDGE,"E3.9"),sQuery(id+"F0.wireOp",EDGE,"E3.11"),sQuery(id+"F0.wireOp",EDGE,"E3.13"),sQuery(id+"F0.wireOp",EDGE,"E3.15"),sQuery(id+"F0.wireOp",EDGE,"E4"),sQuery(id+"F0.wireOp",EDGE,"E5"),sQuery(id+"F0.wireOp",EDGE,"E6"),sQuery(id+"F0.wireOp",EDGE,"E7"),sQuery(id+"F0.wireOp",EDGE,"E8"),sQuery(id+"F0.wireOp",EDGE,"E9"),sQuery(id+"F0.wireOp",EDGE,"E10"),subQ0,sQuery(id+"F0.wireOp",EDGE,"E12"),sQuery(id+"F0.wireOp",EDGE,"E13"),sQuery(id+"F0.wireOp",EDGE,"E14"),sQuery(id+"F0.wireOp",EDGE,"E15"),sQuery(id+"F0.wireOp",EDGE,"E16"),sQuery(id+"F0.wireOp",EDGE,"E17"),sQuery(id+"F0.wireOp",EDGE,"E18"),sQuery(id+"F0.wireOp",EDGE,"E19")])],"isStart":true})],"blendedInto":[makeQuery(id+"F1.opExtrude","CAP_FACE",FACE,{"disambiguationData":[OSD([sQuery(id+"F0.wireOp",EDGE,"E0.0"),sQuery(id+"F0.wireOp",EDGE,"E0.1"),sQuery(id+"F0.wireOp",EDGE,"E0.2"),sQuery(id+"F0.wireOp",EDGE,"E0.3"),sQuery(id+"F0.wireOp",EDGE,"E0.4"),sQuery(id+"F0.wireOp",EDGE,"E0.5"),sQuery(id+"F0.wireOp",EDGE,"E0.6"),sQuery(id+"F0.wireOp",EDGE,"E0.7"),sQuery(id+"F0.wireOp",EDGE,"E0.8"),sQuery(id+"F0.wireOp",EDGE,"E0.9"),sQuery(id+"F0.wireOp",EDGE,"E0.10"),sQuery(id+"F0.wireOp",EDGE,"E0.11"),sQuery(id+"F0.wireOp",EDGE,"E0.12"),sQuery(id+"F0.wireOp",EDGE,"E0.13"),sQuery(id+"F0.wireOp",EDGE,"E0.14"),sQuery(id+"F0.wireOp",EDGE,"E0.15"),sQuery(id+"F0.wireOp",EDGE,"E1"),sQuery(id+"F0.wireOp",EDGE,"E2.1"),sQuery(id+"F0.wireOp",EDGE,"E2.3"),sQuery(id+"F0.wireOp",EDGE,"E2.5"),sQuery(id+"F0.wireOp",EDGE,"E2.7"),sQuery(id+"F0.wireOp",EDGE,"E2.9"),sQuery(id+"F0.wireOp",EDGE,"E2.11"),sQuery(id+"F0.wireOp",EDGE,"E2.13"),sQuery(id+"F0.wireOp",EDGE,"E2.15"),sQuery(id+"F0.wireOp",EDGE,"E3.1"),subQ1,sQuery(id+"F0.wireOp",EDGE,"E3.5"),sQuery(id+"F0.wireOp",EDGE,"E3.7"),sQuery(id+"F0.wireOp",EDGE,"E3.9"),sQuery(id+"F0.wireOp",EDGE,"E3.11"),sQuery(id+"F0.wireOp",EDGE,"E3.13"),sQuery(id+"F0.wireOp",EDGE,"E3.15"),sQuery(id+"F0.wireOp",EDGE,"E4"),sQuery(id+"F0.wireOp",EDGE,"E5"),sQuery(id+"F0.wireOp",EDGE,"E6"),sQuery(id+"F0.wireOp",EDGE,"E7"),sQuery(id+"F0.wireOp",EDGE,"E8"),sQuery(id+"F0.wireOp",EDGE,"E9"),sQuery(id+"F0.wireOp",EDGE,"E10"),subQ0,sQuery(id+"F0.wireOp",EDGE,"E12"),sQuery(id+"F0.wireOp",EDGE,"E13"),sQuery(id+"F0.wireOp",EDGE,"E14"),sQuery(id+"F0.wireOp",EDGE,"E15"),sQuery(id+"F0.wireOp",EDGE,"E16"),sQuery(id+"F0.wireOp",EDGE,"E17"),sQuery(id+"F0.wireOp",EDGE,"E18"),sQuery(id+"F0.wireOp",EDGE,"E19")])],"isStart":true})]});}
            var Q48;
            {var subQ0=sQuery(id+"F0.wireOp",EDGE,"E10");var subQ1=sQuery(id+"F0.wireOp",EDGE,"E3.1");Q48=makeQuery(id+"F5.opChamfer","BLEND_EDGE",EDGE,{"blendedFrom":[makeQuery(id+"F1.opExtrude","SWEPT_EDGE",EDGE,{"disambiguationData":[OSD([subQ1,sQuery(id+"F0.wireOp",EDGE,"E3.2"),subQ0])]}),makeQuery(id+"F1.opExtrude","CAP_FACE",FACE,{"disambiguationData":[OSD([sQuery(id+"F0.wireOp",EDGE,"E0.0"),sQuery(id+"F0.wireOp",EDGE,"E0.1"),sQuery(id+"F0.wireOp",EDGE,"E0.2"),sQuery(id+"F0.wireOp",EDGE,"E0.3"),sQuery(id+"F0.wireOp",EDGE,"E0.4"),sQuery(id+"F0.wireOp",EDGE,"E0.5"),sQuery(id+"F0.wireOp",EDGE,"E0.6"),sQuery(id+"F0.wireOp",EDGE,"E0.7"),sQuery(id+"F0.wireOp",EDGE,"E0.8"),sQuery(id+"F0.wireOp",EDGE,"E0.9"),sQuery(id+"F0.wireOp",EDGE,"E0.10"),sQuery(id+"F0.wireOp",EDGE,"E0.11"),sQuery(id+"F0.wireOp",EDGE,"E0.12"),sQuery(id+"F0.wireOp",EDGE,"E0.13"),sQuery(id+"F0.wireOp",EDGE,"E0.14"),sQuery(id+"F0.wireOp",EDGE,"E0.15"),sQuery(id+"F0.wireOp",EDGE,"E1"),sQuery(id+"F0.wireOp",EDGE,"E2.1"),sQuery(id+"F0.wireOp",EDGE,"E2.3"),sQuery(id+"F0.wireOp",EDGE,"E2.5"),sQuery(id+"F0.wireOp",EDGE,"E2.7"),sQuery(id+"F0.wireOp",EDGE,"E2.9"),sQuery(id+"F0.wireOp",EDGE,"E2.11"),sQuery(id+"F0.wireOp",EDGE,"E2.13"),sQuery(id+"F0.wireOp",EDGE,"E2.15"),subQ1,sQuery(id+"F0.wireOp",EDGE,"E3.3"),sQuery(id+"F0.wireOp",EDGE,"E3.5"),sQuery(id+"F0.wireOp",EDGE,"E3.7"),sQuery(id+"F0.wireOp",EDGE,"E3.9"),sQuery(id+"F0.wireOp",EDGE,"E3.11"),sQuery(id+"F0.wireOp",EDGE,"E3.13"),sQuery(id+"F0.wireOp",EDGE,"E3.15"),sQuery(id+"F0.wireOp",EDGE,"E4"),sQuery(id+"F0.wireOp",EDGE,"E5"),sQuery(id+"F0.wireOp",EDGE,"E6"),sQuery(id+"F0.wireOp",EDGE,"E7"),sQuery(id+"F0.wireOp",EDGE,"E8"),sQuery(id+"F0.wireOp",EDGE,"E9"),subQ0,sQuery(id+"F0.wireOp",EDGE,"E11"),sQuery(id+"F0.wireOp",EDGE,"E12"),sQuery(id+"F0.wireOp",EDGE,"E13"),sQuery(id+"F0.wireOp",EDGE,"E14"),sQuery(id+"F0.wireOp",EDGE,"E15"),sQuery(id+"F0.wireOp",EDGE,"E16"),sQuery(id+"F0.wireOp",EDGE,"E17"),sQuery(id+"F0.wireOp",EDGE,"E18"),sQuery(id+"F0.wireOp",EDGE,"E19")])],"isStart":true})],"blendedInto":[makeQuery(id+"F1.opExtrude","CAP_FACE",FACE,{"disambiguationData":[OSD([sQuery(id+"F0.wireOp",EDGE,"E0.0"),sQuery(id+"F0.wireOp",EDGE,"E0.1"),sQuery(id+"F0.wireOp",EDGE,"E0.2"),sQuery(id+"F0.wireOp",EDGE,"E0.3"),sQuery(id+"F0.wireOp",EDGE,"E0.4"),sQuery(id+"F0.wireOp",EDGE,"E0.5"),sQuery(id+"F0.wireOp",EDGE,"E0.6"),sQuery(id+"F0.wireOp",EDGE,"E0.7"),sQuery(id+"F0.wireOp",EDGE,"E0.8"),sQuery(id+"F0.wireOp",EDGE,"E0.9"),sQuery(id+"F0.wireOp",EDGE,"E0.10"),sQuery(id+"F0.wireOp",EDGE,"E0.11"),sQuery(id+"F0.wireOp",EDGE,"E0.12"),sQuery(id+"F0.wireOp",EDGE,"E0.13"),sQuery(id+"F0.wireOp",EDGE,"E0.14"),sQuery(id+"F0.wireOp",EDGE,"E0.15"),sQuery(id+"F0.wireOp",EDGE,"E1"),sQuery(id+"F0.wireOp",EDGE,"E2.1"),sQuery(id+"F0.wireOp",EDGE,"E2.3"),sQuery(id+"F0.wireOp",EDGE,"E2.5"),sQuery(id+"F0.wireOp",EDGE,"E2.7"),sQuery(id+"F0.wireOp",EDGE,"E2.9"),sQuery(id+"F0.wireOp",EDGE,"E2.11"),sQuery(id+"F0.wireOp",EDGE,"E2.13"),sQuery(id+"F0.wireOp",EDGE,"E2.15"),subQ1,sQuery(id+"F0.wireOp",EDGE,"E3.3"),sQuery(id+"F0.wireOp",EDGE,"E3.5"),sQuery(id+"F0.wireOp",EDGE,"E3.7"),sQuery(id+"F0.wireOp",EDGE,"E3.9"),sQuery(id+"F0.wireOp",EDGE,"E3.11"),sQuery(id+"F0.wireOp",EDGE,"E3.13"),sQuery(id+"F0.wireOp",EDGE,"E3.15"),sQuery(id+"F0.wireOp",EDGE,"E4"),sQuery(id+"F0.wireOp",EDGE,"E5"),sQuery(id+"F0.wireOp",EDGE,"E6"),sQuery(id+"F0.wireOp",EDGE,"E7"),sQuery(id+"F0.wireOp",EDGE,"E8"),sQuery(id+"F0.wireOp",EDGE,"E9"),subQ0,sQuery(id+"F0.wireOp",EDGE,"E11"),sQuery(id+"F0.wireOp",EDGE,"E12"),sQuery(id+"F0.wireOp",EDGE,"E13"),sQuery(id+"F0.wireOp",EDGE,"E14"),sQuery(id+"F0.wireOp",EDGE,"E15"),sQuery(id+"F0.wireOp",EDGE,"E16"),sQuery(id+"F0.wireOp",EDGE,"E17"),sQuery(id+"F0.wireOp",EDGE,"E18"),sQuery(id+"F0.wireOp",EDGE,"E19")])],"isStart":true})]});}
            var Q49;
            Q49=makeQuery(id+"F1.opExtrude","CAP_EDGE",EDGE,{"disambiguationData":[OSD([sQuery(id+"F0.wireOp",EDGE,"E10")])],"isStart":true});
            var Q50;
            Q50=makeQuery(id+"F1.opExtrude","CAP_EDGE",EDGE,{"disambiguationData":[OSD([sQuery(id+"F0.wireOp",EDGE,"E3.1")])],"isStart":true});
            var Q51;
            {var subQ0=sQuery(id+"F0.wireOp",EDGE,"E9");var subQ1=sQuery(id+"F0.wireOp",EDGE,"E3.1");Q51=makeQuery(id+"F5.opChamfer","BLEND_EDGE",EDGE,{"blendedFrom":[makeQuery(id+"F1.opExtrude","SWEPT_EDGE",EDGE,{"disambiguationData":[OSD([sQuery(id+"F0.wireOp",EDGE,"E3.0"),subQ1,subQ0])]}),makeQuery(id+"F1.opExtrude","CAP_FACE",FACE,{"disambiguationData":[OSD([sQuery(id+"F0.wireOp",EDGE,"E0.0"),sQuery(id+"F0.wireOp",EDGE,"E0.1"),sQuery(id+"F0.wireOp",EDGE,"E0.2"),sQuery(id+"F0.wireOp",EDGE,"E0.3"),sQuery(id+"F0.wireOp",EDGE,"E0.4"),sQuery(id+"F0.wireOp",EDGE,"E0.5"),sQuery(id+"F0.wireOp",EDGE,"E0.6"),sQuery(id+"F0.wireOp",EDGE,"E0.7"),sQuery(id+"F0.wireOp",EDGE,"E0.8"),sQuery(id+"F0.wireOp",EDGE,"E0.9"),sQuery(id+"F0.wireOp",EDGE,"E0.10"),sQuery(id+"F0.wireOp",EDGE,"E0.11"),sQuery(id+"F0.wireOp",EDGE,"E0.12"),sQuery(id+"F0.wireOp",EDGE,"E0.13"),sQuery(id+"F0.wireOp",EDGE,"E0.14"),sQuery(id+"F0.wireOp",EDGE,"E0.15"),sQuery(id+"F0.wireOp",EDGE,"E1"),sQuery(id+"F0.wireOp",EDGE,"E2.1"),sQuery(id+"F0.wireOp",EDGE,"E2.3"),sQuery(id+"F0.wireOp",EDGE,"E2.5"),sQuery(id+"F0.wireOp",EDGE,"E2.7"),sQuery(id+"F0.wireOp",EDGE,"E2.9"),sQuery(id+"F0.wireOp",EDGE,"E2.11"),sQuery(id+"F0.wireOp",EDGE,"E2.13"),sQuery(id+"F0.wireOp",EDGE,"E2.15"),subQ1,sQuery(id+"F0.wireOp",EDGE,"E3.3"),sQuery(id+"F0.wireOp",EDGE,"E3.5"),sQuery(id+"F0.wireOp",EDGE,"E3.7"),sQuery(id+"F0.wireOp",EDGE,"E3.9"),sQuery(id+"F0.wireOp",EDGE,"E3.11"),sQuery(id+"F0.wireOp",EDGE,"E3.13"),sQuery(id+"F0.wireOp",EDGE,"E3.15"),sQuery(id+"F0.wireOp",EDGE,"E4"),sQuery(id+"F0.wireOp",EDGE,"E5"),sQuery(id+"F0.wireOp",EDGE,"E6"),sQuery(id+"F0.wireOp",EDGE,"E7"),sQuery(id+"F0.wireOp",EDGE,"E8"),subQ0,sQuery(id+"F0.wireOp",EDGE,"E10"),sQuery(id+"F0.wireOp",EDGE,"E11"),sQuery(id+"F0.wireOp",EDGE,"E12"),sQuery(id+"F0.wireOp",EDGE,"E13"),sQuery(id+"F0.wireOp",EDGE,"E14"),sQuery(id+"F0.wireOp",EDGE,"E15"),sQuery(id+"F0.wireOp",EDGE,"E16"),sQuery(id+"F0.wireOp",EDGE,"E17"),sQuery(id+"F0.wireOp",EDGE,"E18"),sQuery(id+"F0.wireOp",EDGE,"E19")])],"isStart":true})],"blendedInto":[makeQuery(id+"F1.opExtrude","CAP_FACE",FACE,{"disambiguationData":[OSD([sQuery(id+"F0.wireOp",EDGE,"E0.0"),sQuery(id+"F0.wireOp",EDGE,"E0.1"),sQuery(id+"F0.wireOp",EDGE,"E0.2"),sQuery(id+"F0.wireOp",EDGE,"E0.3"),sQuery(id+"F0.wireOp",EDGE,"E0.4"),sQuery(id+"F0.wireOp",EDGE,"E0.5"),sQuery(id+"F0.wireOp",EDGE,"E0.6"),sQuery(id+"F0.wireOp",EDGE,"E0.7"),sQuery(id+"F0.wireOp",EDGE,"E0.8"),sQuery(id+"F0.wireOp",EDGE,"E0.9"),sQuery(id+"F0.wireOp",EDGE,"E0.10"),sQuery(id+"F0.wireOp",EDGE,"E0.11"),sQuery(id+"F0.wireOp",EDGE,"E0.12"),sQuery(id+"F0.wireOp",EDGE,"E0.13"),sQuery(id+"F0.wireOp",EDGE,"E0.14"),sQuery(id+"F0.wireOp",EDGE,"E0.15"),sQuery(id+"F0.wireOp",EDGE,"E1"),sQuery(id+"F0.wireOp",EDGE,"E2.1"),sQuery(id+"F0.wireOp",EDGE,"E2.3"),sQuery(id+"F0.wireOp",EDGE,"E2.5"),sQuery(id+"F0.wireOp",EDGE,"E2.7"),sQuery(id+"F0.wireOp",EDGE,"E2.9"),sQuery(id+"F0.wireOp",EDGE,"E2.11"),sQuery(id+"F0.wireOp",EDGE,"E2.13"),sQuery(id+"F0.wireOp",EDGE,"E2.15"),subQ1,sQuery(id+"F0.wireOp",EDGE,"E3.3"),sQuery(id+"F0.wireOp",EDGE,"E3.5"),sQuery(id+"F0.wireOp",EDGE,"E3.7"),sQuery(id+"F0.wireOp",EDGE,"E3.9"),sQuery(id+"F0.wireOp",EDGE,"E3.11"),sQuery(id+"F0.wireOp",EDGE,"E3.13"),sQuery(id+"F0.wireOp",EDGE,"E3.15"),sQuery(id+"F0.wireOp",EDGE,"E4"),sQuery(id+"F0.wireOp",EDGE,"E5"),sQuery(id+"F0.wireOp",EDGE,"E6"),sQuery(id+"F0.wireOp",EDGE,"E7"),sQuery(id+"F0.wireOp",EDGE,"E8"),subQ0,sQuery(id+"F0.wireOp",EDGE,"E10"),sQuery(id+"F0.wireOp",EDGE,"E11"),sQuery(id+"F0.wireOp",EDGE,"E12"),sQuery(id+"F0.wireOp",EDGE,"E13"),sQuery(id+"F0.wireOp",EDGE,"E14"),sQuery(id+"F0.wireOp",EDGE,"E15"),sQuery(id+"F0.wireOp",EDGE,"E16"),sQuery(id+"F0.wireOp",EDGE,"E17"),sQuery(id+"F0.wireOp",EDGE,"E18"),sQuery(id+"F0.wireOp",EDGE,"E19")])],"isStart":true})]});}
            var Q52;
            Q52=makeQuery(id+"F1.opExtrude","CAP_EDGE",EDGE,{"disambiguationData":[OSD([sQuery(id+"F0.wireOp",EDGE,"E9")])],"isStart":true});
            var Q53;
            {var subQ0=sQuery(id+"F0.wireOp",EDGE,"E9");var subQ1=sQuery(id+"F0.wireOp",EDGE,"E2.1");Q53=makeQuery(id+"F5.opChamfer","BLEND_EDGE",EDGE,{"blendedFrom":[makeQuery(id+"F1.opExtrude","SWEPT_EDGE",EDGE,{"disambiguationData":[OSD([sQuery(id+"F0.wireOp",EDGE,"E2.0"),subQ1,subQ0])]}),makeQuery(id+"F1.opExtrude","CAP_FACE",FACE,{"disambiguationData":[OSD([sQuery(id+"F0.wireOp",EDGE,"E0.0"),sQuery(id+"F0.wireOp",EDGE,"E0.1"),sQuery(id+"F0.wireOp",EDGE,"E0.2"),sQuery(id+"F0.wireOp",EDGE,"E0.3"),sQuery(id+"F0.wireOp",EDGE,"E0.4"),sQuery(id+"F0.wireOp",EDGE,"E0.5"),sQuery(id+"F0.wireOp",EDGE,"E0.6"),sQuery(id+"F0.wireOp",EDGE,"E0.7"),sQuery(id+"F0.wireOp",EDGE,"E0.8"),sQuery(id+"F0.wireOp",EDGE,"E0.9"),sQuery(id+"F0.wireOp",EDGE,"E0.10"),sQuery(id+"F0.wireOp",EDGE,"E0.11"),sQuery(id+"F0.wireOp",EDGE,"E0.12"),sQuery(id+"F0.wireOp",EDGE,"E0.13"),sQuery(id+"F0.wireOp",EDGE,"E0.14"),sQuery(id+"F0.wireOp",EDGE,"E0.15"),sQuery(id+"F0.wireOp",EDGE,"E1"),subQ1,sQuery(id+"F0.wireOp",EDGE,"E2.3"),sQuery(id+"F0.wireOp",EDGE,"E2.5"),sQuery(id+"F0.wireOp",EDGE,"E2.7"),sQuery(id+"F0.wireOp",EDGE,"E2.9"),sQuery(id+"F0.wireOp",EDGE,"E2.11"),sQuery(id+"F0.wireOp",EDGE,"E2.13"),sQuery(id+"F0.wireOp",EDGE,"E2.15"),sQuery(id+"F0.wireOp",EDGE,"E3.1"),sQuery(id+"F0.wireOp",EDGE,"E3.3"),sQuery(id+"F0.wireOp",EDGE,"E3.5"),sQuery(id+"F0.wireOp",EDGE,"E3.7"),sQuery(id+"F0.wireOp",EDGE,"E3.9"),sQuery(id+"F0.wireOp",EDGE,"E3.11"),sQuery(id+"F0.wireOp",EDGE,"E3.13"),sQuery(id+"F0.wireOp",EDGE,"E3.15"),sQuery(id+"F0.wireOp",EDGE,"E4"),sQuery(id+"F0.wireOp",EDGE,"E5"),sQuery(id+"F0.wireOp",EDGE,"E6"),sQuery(id+"F0.wireOp",EDGE,"E7"),sQuery(id+"F0.wireOp",EDGE,"E8"),subQ0,sQuery(id+"F0.wireOp",EDGE,"E10"),sQuery(id+"F0.wireOp",EDGE,"E11"),sQuery(id+"F0.wireOp",EDGE,"E12"),sQuery(id+"F0.wireOp",EDGE,"E13"),sQuery(id+"F0.wireOp",EDGE,"E14"),sQuery(id+"F0.wireOp",EDGE,"E15"),sQuery(id+"F0.wireOp",EDGE,"E16"),sQuery(id+"F0.wireOp",EDGE,"E17"),sQuery(id+"F0.wireOp",EDGE,"E18"),sQuery(id+"F0.wireOp",EDGE,"E19")])],"isStart":true})],"blendedInto":[makeQuery(id+"F1.opExtrude","CAP_FACE",FACE,{"disambiguationData":[OSD([sQuery(id+"F0.wireOp",EDGE,"E0.0"),sQuery(id+"F0.wireOp",EDGE,"E0.1"),sQuery(id+"F0.wireOp",EDGE,"E0.2"),sQuery(id+"F0.wireOp",EDGE,"E0.3"),sQuery(id+"F0.wireOp",EDGE,"E0.4"),sQuery(id+"F0.wireOp",EDGE,"E0.5"),sQuery(id+"F0.wireOp",EDGE,"E0.6"),sQuery(id+"F0.wireOp",EDGE,"E0.7"),sQuery(id+"F0.wireOp",EDGE,"E0.8"),sQuery(id+"F0.wireOp",EDGE,"E0.9"),sQuery(id+"F0.wireOp",EDGE,"E0.10"),sQuery(id+"F0.wireOp",EDGE,"E0.11"),sQuery(id+"F0.wireOp",EDGE,"E0.12"),sQuery(id+"F0.wireOp",EDGE,"E0.13"),sQuery(id+"F0.wireOp",EDGE,"E0.14"),sQuery(id+"F0.wireOp",EDGE,"E0.15"),sQuery(id+"F0.wireOp",EDGE,"E1"),subQ1,sQuery(id+"F0.wireOp",EDGE,"E2.3"),sQuery(id+"F0.wireOp",EDGE,"E2.5"),sQuery(id+"F0.wireOp",EDGE,"E2.7"),sQuery(id+"F0.wireOp",EDGE,"E2.9"),sQuery(id+"F0.wireOp",EDGE,"E2.11"),sQuery(id+"F0.wireOp",EDGE,"E2.13"),sQuery(id+"F0.wireOp",EDGE,"E2.15"),sQuery(id+"F0.wireOp",EDGE,"E3.1"),sQuery(id+"F0.wireOp",EDGE,"E3.3"),sQuery(id+"F0.wireOp",EDGE,"E3.5"),sQuery(id+"F0.wireOp",EDGE,"E3.7"),sQuery(id+"F0.wireOp",EDGE,"E3.9"),sQuery(id+"F0.wireOp",EDGE,"E3.11"),sQuery(id+"F0.wireOp",EDGE,"E3.13"),sQuery(id+"F0.wireOp",EDGE,"E3.15"),sQuery(id+"F0.wireOp",EDGE,"E4"),sQuery(id+"F0.wireOp",EDGE,"E5"),sQuery(id+"F0.wireOp",EDGE,"E6"),sQuery(id+"F0.wireOp",EDGE,"E7"),sQuery(id+"F0.wireOp",EDGE,"E8"),subQ0,sQuery(id+"F0.wireOp",EDGE,"E10"),sQuery(id+"F0.wireOp",EDGE,"E11"),sQuery(id+"F0.wireOp",EDGE,"E12"),sQuery(id+"F0.wireOp",EDGE,"E13"),sQuery(id+"F0.wireOp",EDGE,"E14"),sQuery(id+"F0.wireOp",EDGE,"E15"),sQuery(id+"F0.wireOp",EDGE,"E16"),sQuery(id+"F0.wireOp",EDGE,"E17"),sQuery(id+"F0.wireOp",EDGE,"E18"),sQuery(id+"F0.wireOp",EDGE,"E19")])],"isStart":true})]});}
            var Q54;
            Q54=makeQuery(id+"F1.opExtrude","CAP_EDGE",EDGE,{"disambiguationData":[OSD([sQuery(id+"F0.wireOp",EDGE,"E2.1")])],"isStart":true});
            var Q55;
            {var subQ0=sQuery(id+"F0.wireOp",EDGE,"E10");var subQ1=sQuery(id+"F0.wireOp",EDGE,"E2.1");Q55=makeQuery(id+"F5.opChamfer","BLEND_EDGE",EDGE,{"blendedFrom":[makeQuery(id+"F1.opExtrude","SWEPT_EDGE",EDGE,{"disambiguationData":[OSD([subQ1,sQuery(id+"F0.wireOp",EDGE,"E2.2"),subQ0])]}),makeQuery(id+"F1.opExtrude","CAP_FACE",FACE,{"disambiguationData":[OSD([sQuery(id+"F0.wireOp",EDGE,"E0.0"),sQuery(id+"F0.wireOp",EDGE,"E0.1"),sQuery(id+"F0.wireOp",EDGE,"E0.2"),sQuery(id+"F0.wireOp",EDGE,"E0.3"),sQuery(id+"F0.wireOp",EDGE,"E0.4"),sQuery(id+"F0.wireOp",EDGE,"E0.5"),sQuery(id+"F0.wireOp",EDGE,"E0.6"),sQuery(id+"F0.wireOp",EDGE,"E0.7"),sQuery(id+"F0.wireOp",EDGE,"E0.8"),sQuery(id+"F0.wireOp",EDGE,"E0.9"),sQuery(id+"F0.wireOp",EDGE,"E0.10"),sQuery(id+"F0.wireOp",EDGE,"E0.11"),sQuery(id+"F0.wireOp",EDGE,"E0.12"),sQuery(id+"F0.wireOp",EDGE,"E0.13"),sQuery(id+"F0.wireOp",EDGE,"E0.14"),sQuery(id+"F0.wireOp",EDGE,"E0.15"),sQuery(id+"F0.wireOp",EDGE,"E1"),subQ1,sQuery(id+"F0.wireOp",EDGE,"E2.3"),sQuery(id+"F0.wireOp",EDGE,"E2.5"),sQuery(id+"F0.wireOp",EDGE,"E2.7"),sQuery(id+"F0.wireOp",EDGE,"E2.9"),sQuery(id+"F0.wireOp",EDGE,"E2.11"),sQuery(id+"F0.wireOp",EDGE,"E2.13"),sQuery(id+"F0.wireOp",EDGE,"E2.15"),sQuery(id+"F0.wireOp",EDGE,"E3.1"),sQuery(id+"F0.wireOp",EDGE,"E3.3"),sQuery(id+"F0.wireOp",EDGE,"E3.5"),sQuery(id+"F0.wireOp",EDGE,"E3.7"),sQuery(id+"F0.wireOp",EDGE,"E3.9"),sQuery(id+"F0.wireOp",EDGE,"E3.11"),sQuery(id+"F0.wireOp",EDGE,"E3.13"),sQuery(id+"F0.wireOp",EDGE,"E3.15"),sQuery(id+"F0.wireOp",EDGE,"E4"),sQuery(id+"F0.wireOp",EDGE,"E5"),sQuery(id+"F0.wireOp",EDGE,"E6"),sQuery(id+"F0.wireOp",EDGE,"E7"),sQuery(id+"F0.wireOp",EDGE,"E8"),sQuery(id+"F0.wireOp",EDGE,"E9"),subQ0,sQuery(id+"F0.wireOp",EDGE,"E11"),sQuery(id+"F0.wireOp",EDGE,"E12"),sQuery(id+"F0.wireOp",EDGE,"E13"),sQuery(id+"F0.wireOp",EDGE,"E14"),sQuery(id+"F0.wireOp",EDGE,"E15"),sQuery(id+"F0.wireOp",EDGE,"E16"),sQuery(id+"F0.wireOp",EDGE,"E17"),sQuery(id+"F0.wireOp",EDGE,"E18"),sQuery(id+"F0.wireOp",EDGE,"E19")])],"isStart":true})],"blendedInto":[makeQuery(id+"F1.opExtrude","CAP_FACE",FACE,{"disambiguationData":[OSD([sQuery(id+"F0.wireOp",EDGE,"E0.0"),sQuery(id+"F0.wireOp",EDGE,"E0.1"),sQuery(id+"F0.wireOp",EDGE,"E0.2"),sQuery(id+"F0.wireOp",EDGE,"E0.3"),sQuery(id+"F0.wireOp",EDGE,"E0.4"),sQuery(id+"F0.wireOp",EDGE,"E0.5"),sQuery(id+"F0.wireOp",EDGE,"E0.6"),sQuery(id+"F0.wireOp",EDGE,"E0.7"),sQuery(id+"F0.wireOp",EDGE,"E0.8"),sQuery(id+"F0.wireOp",EDGE,"E0.9"),sQuery(id+"F0.wireOp",EDGE,"E0.10"),sQuery(id+"F0.wireOp",EDGE,"E0.11"),sQuery(id+"F0.wireOp",EDGE,"E0.12"),sQuery(id+"F0.wireOp",EDGE,"E0.13"),sQuery(id+"F0.wireOp",EDGE,"E0.14"),sQuery(id+"F0.wireOp",EDGE,"E0.15"),sQuery(id+"F0.wireOp",EDGE,"E1"),subQ1,sQuery(id+"F0.wireOp",EDGE,"E2.3"),sQuery(id+"F0.wireOp",EDGE,"E2.5"),sQuery(id+"F0.wireOp",EDGE,"E2.7"),sQuery(id+"F0.wireOp",EDGE,"E2.9"),sQuery(id+"F0.wireOp",EDGE,"E2.11"),sQuery(id+"F0.wireOp",EDGE,"E2.13"),sQuery(id+"F0.wireOp",EDGE,"E2.15"),sQuery(id+"F0.wireOp",EDGE,"E3.1"),sQuery(id+"F0.wireOp",EDGE,"E3.3"),sQuery(id+"F0.wireOp",EDGE,"E3.5"),sQuery(id+"F0.wireOp",EDGE,"E3.7"),sQuery(id+"F0.wireOp",EDGE,"E3.9"),sQuery(id+"F0.wireOp",EDGE,"E3.11"),sQuery(id+"F0.wireOp",EDGE,"E3.13"),sQuery(id+"F0.wireOp",EDGE,"E3.15"),sQuery(id+"F0.wireOp",EDGE,"E4"),sQuery(id+"F0.wireOp",EDGE,"E5"),sQuery(id+"F0.wireOp",EDGE,"E6"),sQuery(id+"F0.wireOp",EDGE,"E7"),sQuery(id+"F0.wireOp",EDGE,"E8"),sQuery(id+"F0.wireOp",EDGE,"E9"),subQ0,sQuery(id+"F0.wireOp",EDGE,"E11"),sQuery(id+"F0.wireOp",EDGE,"E12"),sQuery(id+"F0.wireOp",EDGE,"E13"),sQuery(id+"F0.wireOp",EDGE,"E14"),sQuery(id+"F0.wireOp",EDGE,"E15"),sQuery(id+"F0.wireOp",EDGE,"E16"),sQuery(id+"F0.wireOp",EDGE,"E17"),sQuery(id+"F0.wireOp",EDGE,"E18"),sQuery(id+"F0.wireOp",EDGE,"E19")])],"isStart":true})]});}
            var Q56;
            Q56=makeQuery(id+"F1.opExtrude","CAP_EDGE",EDGE,{"disambiguationData":[OSD([sQuery(id+"F0.wireOp",EDGE,"E3.15")])],"isStart":true});
            var Q57;
            Q57=makeQuery(id+"F1.opExtrude","CAP_EDGE",EDGE,{"disambiguationData":[OSD([sQuery(id+"F0.wireOp",EDGE,"E7")])],"isStart":true});
            var Q58;
            {var subQ0=sQuery(id+"F0.wireOp",EDGE,"E7");var subQ1=sQuery(id+"F0.wireOp",EDGE,"E2.15");Q58=makeQuery(id+"F5.opChamfer","BLEND_EDGE",EDGE,{"blendedFrom":[makeQuery(id+"F1.opExtrude","SWEPT_EDGE",EDGE,{"disambiguationData":[OSD([sQuery(id+"F0.wireOp",EDGE,"E2.14"),subQ1,subQ0])]}),makeQuery(id+"F1.opExtrude","CAP_FACE",FACE,{"disambiguationData":[OSD([sQuery(id+"F0.wireOp",EDGE,"E0.0"),sQuery(id+"F0.wireOp",EDGE,"E0.1"),sQuery(id+"F0.wireOp",EDGE,"E0.2"),sQuery(id+"F0.wireOp",EDGE,"E0.3"),sQuery(id+"F0.wireOp",EDGE,"E0.4"),sQuery(id+"F0.wireOp",EDGE,"E0.5"),sQuery(id+"F0.wireOp",EDGE,"E0.6"),sQuery(id+"F0.wireOp",EDGE,"E0.7"),sQuery(id+"F0.wireOp",EDGE,"E0.8"),sQuery(id+"F0.wireOp",EDGE,"E0.9"),sQuery(id+"F0.wireOp",EDGE,"E0.10"),sQuery(id+"F0.wireOp",EDGE,"E0.11"),sQuery(id+"F0.wireOp",EDGE,"E0.12"),sQuery(id+"F0.wireOp",EDGE,"E0.13"),sQuery(id+"F0.wireOp",EDGE,"E0.14"),sQuery(id+"F0.wireOp",EDGE,"E0.15"),sQuery(id+"F0.wireOp",EDGE,"E1"),sQuery(id+"F0.wireOp",EDGE,"E2.1"),sQuery(id+"F0.wireOp",EDGE,"E2.3"),sQuery(id+"F0.wireOp",EDGE,"E2.5"),sQuery(id+"F0.wireOp",EDGE,"E2.7"),sQuery(id+"F0.wireOp",EDGE,"E2.9"),sQuery(id+"F0.wireOp",EDGE,"E2.11"),sQuery(id+"F0.wireOp",EDGE,"E2.13"),subQ1,sQuery(id+"F0.wireOp",EDGE,"E3.1"),sQuery(id+"F0.wireOp",EDGE,"E3.3"),sQuery(id+"F0.wireOp",EDGE,"E3.5"),sQuery(id+"F0.wireOp",EDGE,"E3.7"),sQuery(id+"F0.wireOp",EDGE,"E3.9"),sQuery(id+"F0.wireOp",EDGE,"E3.11"),sQuery(id+"F0.wireOp",EDGE,"E3.13"),sQuery(id+"F0.wireOp",EDGE,"E3.15"),sQuery(id+"F0.wireOp",EDGE,"E4"),sQuery(id+"F0.wireOp",EDGE,"E5"),sQuery(id+"F0.wireOp",EDGE,"E6"),subQ0,sQuery(id+"F0.wireOp",EDGE,"E8"),sQuery(id+"F0.wireOp",EDGE,"E9"),sQuery(id+"F0.wireOp",EDGE,"E10"),sQuery(id+"F0.wireOp",EDGE,"E11"),sQuery(id+"F0.wireOp",EDGE,"E12"),sQuery(id+"F0.wireOp",EDGE,"E13"),sQuery(id+"F0.wireOp",EDGE,"E14"),sQuery(id+"F0.wireOp",EDGE,"E15"),sQuery(id+"F0.wireOp",EDGE,"E16"),sQuery(id+"F0.wireOp",EDGE,"E17"),sQuery(id+"F0.wireOp",EDGE,"E18"),sQuery(id+"F0.wireOp",EDGE,"E19")])],"isStart":true})],"blendedInto":[makeQuery(id+"F1.opExtrude","CAP_FACE",FACE,{"disambiguationData":[OSD([sQuery(id+"F0.wireOp",EDGE,"E0.0"),sQuery(id+"F0.wireOp",EDGE,"E0.1"),sQuery(id+"F0.wireOp",EDGE,"E0.2"),sQuery(id+"F0.wireOp",EDGE,"E0.3"),sQuery(id+"F0.wireOp",EDGE,"E0.4"),sQuery(id+"F0.wireOp",EDGE,"E0.5"),sQuery(id+"F0.wireOp",EDGE,"E0.6"),sQuery(id+"F0.wireOp",EDGE,"E0.7"),sQuery(id+"F0.wireOp",EDGE,"E0.8"),sQuery(id+"F0.wireOp",EDGE,"E0.9"),sQuery(id+"F0.wireOp",EDGE,"E0.10"),sQuery(id+"F0.wireOp",EDGE,"E0.11"),sQuery(id+"F0.wireOp",EDGE,"E0.12"),sQuery(id+"F0.wireOp",EDGE,"E0.13"),sQuery(id+"F0.wireOp",EDGE,"E0.14"),sQuery(id+"F0.wireOp",EDGE,"E0.15"),sQuery(id+"F0.wireOp",EDGE,"E1"),sQuery(id+"F0.wireOp",EDGE,"E2.1"),sQuery(id+"F0.wireOp",EDGE,"E2.3"),sQuery(id+"F0.wireOp",EDGE,"E2.5"),sQuery(id+"F0.wireOp",EDGE,"E2.7"),sQuery(id+"F0.wireOp",EDGE,"E2.9"),sQuery(id+"F0.wireOp",EDGE,"E2.11"),sQuery(id+"F0.wireOp",EDGE,"E2.13"),subQ1,sQuery(id+"F0.wireOp",EDGE,"E3.1"),sQuery(id+"F0.wireOp",EDGE,"E3.3"),sQuery(id+"F0.wireOp",EDGE,"E3.5"),sQuery(id+"F0.wireOp",EDGE,"E3.7"),sQuery(id+"F0.wireOp",EDGE,"E3.9"),sQuery(id+"F0.wireOp",EDGE,"E3.11"),sQuery(id+"F0.wireOp",EDGE,"E3.13"),sQuery(id+"F0.wireOp",EDGE,"E3.15"),sQuery(id+"F0.wireOp",EDGE,"E4"),sQuery(id+"F0.wireOp",EDGE,"E5"),sQuery(id+"F0.wireOp",EDGE,"E6"),subQ0,sQuery(id+"F0.wireOp",EDGE,"E8"),sQuery(id+"F0.wireOp",EDGE,"E9"),sQuery(id+"F0.wireOp",EDGE,"E10"),sQuery(id+"F0.wireOp",EDGE,"E11"),sQuery(id+"F0.wireOp",EDGE,"E12"),sQuery(id+"F0.wireOp",EDGE,"E13"),sQuery(id+"F0.wireOp",EDGE,"E14"),sQuery(id+"F0.wireOp",EDGE,"E15"),sQuery(id+"F0.wireOp",EDGE,"E16"),sQuery(id+"F0.wireOp",EDGE,"E17"),sQuery(id+"F0.wireOp",EDGE,"E18"),sQuery(id+"F0.wireOp",EDGE,"E19")])],"isStart":true})]});}
            var Q59;
            {var subQ0=sQuery(id+"F0.wireOp",EDGE,"E7");var subQ1=sQuery(id+"F0.wireOp",EDGE,"E3.15");Q59=makeQuery(id+"F5.opChamfer","BLEND_EDGE",EDGE,{"blendedFrom":[makeQuery(id+"F1.opExtrude","SWEPT_EDGE",EDGE,{"disambiguationData":[OSD([sQuery(id+"F0.wireOp",EDGE,"E3.14"),subQ1,subQ0])]}),makeQuery(id+"F1.opExtrude","CAP_FACE",FACE,{"disambiguationData":[OSD([sQuery(id+"F0.wireOp",EDGE,"E0.0"),sQuery(id+"F0.wireOp",EDGE,"E0.1"),sQuery(id+"F0.wireOp",EDGE,"E0.2"),sQuery(id+"F0.wireOp",EDGE,"E0.3"),sQuery(id+"F0.wireOp",EDGE,"E0.4"),sQuery(id+"F0.wireOp",EDGE,"E0.5"),sQuery(id+"F0.wireOp",EDGE,"E0.6"),sQuery(id+"F0.wireOp",EDGE,"E0.7"),sQuery(id+"F0.wireOp",EDGE,"E0.8"),sQuery(id+"F0.wireOp",EDGE,"E0.9"),sQuery(id+"F0.wireOp",EDGE,"E0.10"),sQuery(id+"F0.wireOp",EDGE,"E0.11"),sQuery(id+"F0.wireOp",EDGE,"E0.12"),sQuery(id+"F0.wireOp",EDGE,"E0.13"),sQuery(id+"F0.wireOp",EDGE,"E0.14"),sQuery(id+"F0.wireOp",EDGE,"E0.15"),sQuery(id+"F0.wireOp",EDGE,"E1"),sQuery(id+"F0.wireOp",EDGE,"E2.1"),sQuery(id+"F0.wireOp",EDGE,"E2.3"),sQuery(id+"F0.wireOp",EDGE,"E2.5"),sQuery(id+"F0.wireOp",EDGE,"E2.7"),sQuery(id+"F0.wireOp",EDGE,"E2.9"),sQuery(id+"F0.wireOp",EDGE,"E2.11"),sQuery(id+"F0.wireOp",EDGE,"E2.13"),sQuery(id+"F0.wireOp",EDGE,"E2.15"),sQuery(id+"F0.wireOp",EDGE,"E3.1"),sQuery(id+"F0.wireOp",EDGE,"E3.3"),sQuery(id+"F0.wireOp",EDGE,"E3.5"),sQuery(id+"F0.wireOp",EDGE,"E3.7"),sQuery(id+"F0.wireOp",EDGE,"E3.9"),sQuery(id+"F0.wireOp",EDGE,"E3.11"),sQuery(id+"F0.wireOp",EDGE,"E3.13"),subQ1,sQuery(id+"F0.wireOp",EDGE,"E4"),sQuery(id+"F0.wireOp",EDGE,"E5"),sQuery(id+"F0.wireOp",EDGE,"E6"),subQ0,sQuery(id+"F0.wireOp",EDGE,"E8"),sQuery(id+"F0.wireOp",EDGE,"E9"),sQuery(id+"F0.wireOp",EDGE,"E10"),sQuery(id+"F0.wireOp",EDGE,"E11"),sQuery(id+"F0.wireOp",EDGE,"E12"),sQuery(id+"F0.wireOp",EDGE,"E13"),sQuery(id+"F0.wireOp",EDGE,"E14"),sQuery(id+"F0.wireOp",EDGE,"E15"),sQuery(id+"F0.wireOp",EDGE,"E16"),sQuery(id+"F0.wireOp",EDGE,"E17"),sQuery(id+"F0.wireOp",EDGE,"E18"),sQuery(id+"F0.wireOp",EDGE,"E19")])],"isStart":true})],"blendedInto":[makeQuery(id+"F1.opExtrude","CAP_FACE",FACE,{"disambiguationData":[OSD([sQuery(id+"F0.wireOp",EDGE,"E0.0"),sQuery(id+"F0.wireOp",EDGE,"E0.1"),sQuery(id+"F0.wireOp",EDGE,"E0.2"),sQuery(id+"F0.wireOp",EDGE,"E0.3"),sQuery(id+"F0.wireOp",EDGE,"E0.4"),sQuery(id+"F0.wireOp",EDGE,"E0.5"),sQuery(id+"F0.wireOp",EDGE,"E0.6"),sQuery(id+"F0.wireOp",EDGE,"E0.7"),sQuery(id+"F0.wireOp",EDGE,"E0.8"),sQuery(id+"F0.wireOp",EDGE,"E0.9"),sQuery(id+"F0.wireOp",EDGE,"E0.10"),sQuery(id+"F0.wireOp",EDGE,"E0.11"),sQuery(id+"F0.wireOp",EDGE,"E0.12"),sQuery(id+"F0.wireOp",EDGE,"E0.13"),sQuery(id+"F0.wireOp",EDGE,"E0.14"),sQuery(id+"F0.wireOp",EDGE,"E0.15"),sQuery(id+"F0.wireOp",EDGE,"E1"),sQuery(id+"F0.wireOp",EDGE,"E2.1"),sQuery(id+"F0.wireOp",EDGE,"E2.3"),sQuery(id+"F0.wireOp",EDGE,"E2.5"),sQuery(id+"F0.wireOp",EDGE,"E2.7"),sQuery(id+"F0.wireOp",EDGE,"E2.9"),sQuery(id+"F0.wireOp",EDGE,"E2.11"),sQuery(id+"F0.wireOp",EDGE,"E2.13"),sQuery(id+"F0.wireOp",EDGE,"E2.15"),sQuery(id+"F0.wireOp",EDGE,"E3.1"),sQuery(id+"F0.wireOp",EDGE,"E3.3"),sQuery(id+"F0.wireOp",EDGE,"E3.5"),sQuery(id+"F0.wireOp",EDGE,"E3.7"),sQuery(id+"F0.wireOp",EDGE,"E3.9"),sQuery(id+"F0.wireOp",EDGE,"E3.11"),sQuery(id+"F0.wireOp",EDGE,"E3.13"),subQ1,sQuery(id+"F0.wireOp",EDGE,"E4"),sQuery(id+"F0.wireOp",EDGE,"E5"),sQuery(id+"F0.wireOp",EDGE,"E6"),subQ0,sQuery(id+"F0.wireOp",EDGE,"E8"),sQuery(id+"F0.wireOp",EDGE,"E9"),sQuery(id+"F0.wireOp",EDGE,"E10"),sQuery(id+"F0.wireOp",EDGE,"E11"),sQuery(id+"F0.wireOp",EDGE,"E12"),sQuery(id+"F0.wireOp",EDGE,"E13"),sQuery(id+"F0.wireOp",EDGE,"E14"),sQuery(id+"F0.wireOp",EDGE,"E15"),sQuery(id+"F0.wireOp",EDGE,"E16"),sQuery(id+"F0.wireOp",EDGE,"E17"),sQuery(id+"F0.wireOp",EDGE,"E18"),sQuery(id+"F0.wireOp",EDGE,"E19")])],"isStart":true})]});}
            var Q60;
            {var subQ0=sQuery(id+"F0.wireOp",EDGE,"E8");var subQ1=sQuery(id+"F0.wireOp",EDGE,"E3.15");Q60=makeQuery(id+"F5.opChamfer","BLEND_EDGE",EDGE,{"blendedFrom":[makeQuery(id+"F1.opExtrude","SWEPT_EDGE",EDGE,{"disambiguationData":[OSD([sQuery(id+"F0.wireOp",EDGE,"E3.0"),subQ1,subQ0])]}),makeQuery(id+"F1.opExtrude","CAP_FACE",FACE,{"disambiguationData":[OSD([sQuery(id+"F0.wireOp",EDGE,"E0.0"),sQuery(id+"F0.wireOp",EDGE,"E0.1"),sQuery(id+"F0.wireOp",EDGE,"E0.2"),sQuery(id+"F0.wireOp",EDGE,"E0.3"),sQuery(id+"F0.wireOp",EDGE,"E0.4"),sQuery(id+"F0.wireOp",EDGE,"E0.5"),sQuery(id+"F0.wireOp",EDGE,"E0.6"),sQuery(id+"F0.wireOp",EDGE,"E0.7"),sQuery(id+"F0.wireOp",EDGE,"E0.8"),sQuery(id+"F0.wireOp",EDGE,"E0.9"),sQuery(id+"F0.wireOp",EDGE,"E0.10"),sQuery(id+"F0.wireOp",EDGE,"E0.11"),sQuery(id+"F0.wireOp",EDGE,"E0.12"),sQuery(id+"F0.wireOp",EDGE,"E0.13"),sQuery(id+"F0.wireOp",EDGE,"E0.14"),sQuery(id+"F0.wireOp",EDGE,"E0.15"),sQuery(id+"F0.wireOp",EDGE,"E1"),sQuery(id+"F0.wireOp",EDGE,"E2.1"),sQuery(id+"F0.wireOp",EDGE,"E2.3"),sQuery(id+"F0.wireOp",EDGE,"E2.5"),sQuery(id+"F0.wireOp",EDGE,"E2.7"),sQuery(id+"F0.wireOp",EDGE,"E2.9"),sQuery(id+"F0.wireOp",EDGE,"E2.11"),sQuery(id+"F0.wireOp",EDGE,"E2.13"),sQuery(id+"F0.wireOp",EDGE,"E2.15"),sQuery(id+"F0.wireOp",EDGE,"E3.1"),sQuery(id+"F0.wireOp",EDGE,"E3.3"),sQuery(id+"F0.wireOp",EDGE,"E3.5"),sQuery(id+"F0.wireOp",EDGE,"E3.7"),sQuery(id+"F0.wireOp",EDGE,"E3.9"),sQuery(id+"F0.wireOp",EDGE,"E3.11"),sQuery(id+"F0.wireOp",EDGE,"E3.13"),subQ1,sQuery(id+"F0.wireOp",EDGE,"E4"),sQuery(id+"F0.wireOp",EDGE,"E5"),sQuery(id+"F0.wireOp",EDGE,"E6"),sQuery(id+"F0.wireOp",EDGE,"E7"),subQ0,sQuery(id+"F0.wireOp",EDGE,"E9"),sQuery(id+"F0.wireOp",EDGE,"E10"),sQuery(id+"F0.wireOp",EDGE,"E11"),sQuery(id+"F0.wireOp",EDGE,"E12"),sQuery(id+"F0.wireOp",EDGE,"E13"),sQuery(id+"F0.wireOp",EDGE,"E14"),sQuery(id+"F0.wireOp",EDGE,"E15"),sQuery(id+"F0.wireOp",EDGE,"E16"),sQuery(id+"F0.wireOp",EDGE,"E17"),sQuery(id+"F0.wireOp",EDGE,"E18"),sQuery(id+"F0.wireOp",EDGE,"E19")])],"isStart":true})],"blendedInto":[makeQuery(id+"F1.opExtrude","CAP_FACE",FACE,{"disambiguationData":[OSD([sQuery(id+"F0.wireOp",EDGE,"E0.0"),sQuery(id+"F0.wireOp",EDGE,"E0.1"),sQuery(id+"F0.wireOp",EDGE,"E0.2"),sQuery(id+"F0.wireOp",EDGE,"E0.3"),sQuery(id+"F0.wireOp",EDGE,"E0.4"),sQuery(id+"F0.wireOp",EDGE,"E0.5"),sQuery(id+"F0.wireOp",EDGE,"E0.6"),sQuery(id+"F0.wireOp",EDGE,"E0.7"),sQuery(id+"F0.wireOp",EDGE,"E0.8"),sQuery(id+"F0.wireOp",EDGE,"E0.9"),sQuery(id+"F0.wireOp",EDGE,"E0.10"),sQuery(id+"F0.wireOp",EDGE,"E0.11"),sQuery(id+"F0.wireOp",EDGE,"E0.12"),sQuery(id+"F0.wireOp",EDGE,"E0.13"),sQuery(id+"F0.wireOp",EDGE,"E0.14"),sQuery(id+"F0.wireOp",EDGE,"E0.15"),sQuery(id+"F0.wireOp",EDGE,"E1"),sQuery(id+"F0.wireOp",EDGE,"E2.1"),sQuery(id+"F0.wireOp",EDGE,"E2.3"),sQuery(id+"F0.wireOp",EDGE,"E2.5"),sQuery(id+"F0.wireOp",EDGE,"E2.7"),sQuery(id+"F0.wireOp",EDGE,"E2.9"),sQuery(id+"F0.wireOp",EDGE,"E2.11"),sQuery(id+"F0.wireOp",EDGE,"E2.13"),sQuery(id+"F0.wireOp",EDGE,"E2.15"),sQuery(id+"F0.wireOp",EDGE,"E3.1"),sQuery(id+"F0.wireOp",EDGE,"E3.3"),sQuery(id+"F0.wireOp",EDGE,"E3.5"),sQuery(id+"F0.wireOp",EDGE,"E3.7"),sQuery(id+"F0.wireOp",EDGE,"E3.9"),sQuery(id+"F0.wireOp",EDGE,"E3.11"),sQuery(id+"F0.wireOp",EDGE,"E3.13"),subQ1,sQuery(id+"F0.wireOp",EDGE,"E4"),sQuery(id+"F0.wireOp",EDGE,"E5"),sQuery(id+"F0.wireOp",EDGE,"E6"),sQuery(id+"F0.wireOp",EDGE,"E7"),subQ0,sQuery(id+"F0.wireOp",EDGE,"E9"),sQuery(id+"F0.wireOp",EDGE,"E10"),sQuery(id+"F0.wireOp",EDGE,"E11"),sQuery(id+"F0.wireOp",EDGE,"E12"),sQuery(id+"F0.wireOp",EDGE,"E13"),sQuery(id+"F0.wireOp",EDGE,"E14"),sQuery(id+"F0.wireOp",EDGE,"E15"),sQuery(id+"F0.wireOp",EDGE,"E16"),sQuery(id+"F0.wireOp",EDGE,"E17"),sQuery(id+"F0.wireOp",EDGE,"E18"),sQuery(id+"F0.wireOp",EDGE,"E19")])],"isStart":true})]});}
            var Q61;
            Q61=makeQuery(id+"F1.opExtrude","CAP_EDGE",EDGE,{"disambiguationData":[OSD([sQuery(id+"F0.wireOp",EDGE,"E8")])],"isStart":true});
            var Q62;
            {var subQ0=sQuery(id+"F0.wireOp",EDGE,"E8");var subQ1=sQuery(id+"F0.wireOp",EDGE,"E2.15");Q62=makeQuery(id+"F5.opChamfer","BLEND_EDGE",EDGE,{"blendedFrom":[makeQuery(id+"F1.opExtrude","SWEPT_EDGE",EDGE,{"disambiguationData":[OSD([sQuery(id+"F0.wireOp",EDGE,"E2.0"),subQ1,subQ0])]}),makeQuery(id+"F1.opExtrude","CAP_FACE",FACE,{"disambiguationData":[OSD([sQuery(id+"F0.wireOp",EDGE,"E0.0"),sQuery(id+"F0.wireOp",EDGE,"E0.1"),sQuery(id+"F0.wireOp",EDGE,"E0.2"),sQuery(id+"F0.wireOp",EDGE,"E0.3"),sQuery(id+"F0.wireOp",EDGE,"E0.4"),sQuery(id+"F0.wireOp",EDGE,"E0.5"),sQuery(id+"F0.wireOp",EDGE,"E0.6"),sQuery(id+"F0.wireOp",EDGE,"E0.7"),sQuery(id+"F0.wireOp",EDGE,"E0.8"),sQuery(id+"F0.wireOp",EDGE,"E0.9"),sQuery(id+"F0.wireOp",EDGE,"E0.10"),sQuery(id+"F0.wireOp",EDGE,"E0.11"),sQuery(id+"F0.wireOp",EDGE,"E0.12"),sQuery(id+"F0.wireOp",EDGE,"E0.13"),sQuery(id+"F0.wireOp",EDGE,"E0.14"),sQuery(id+"F0.wireOp",EDGE,"E0.15"),sQuery(id+"F0.wireOp",EDGE,"E1"),sQuery(id+"F0.wireOp",EDGE,"E2.1"),sQuery(id+"F0.wireOp",EDGE,"E2.3"),sQuery(id+"F0.wireOp",EDGE,"E2.5"),sQuery(id+"F0.wireOp",EDGE,"E2.7"),sQuery(id+"F0.wireOp",EDGE,"E2.9"),sQuery(id+"F0.wireOp",EDGE,"E2.11"),sQuery(id+"F0.wireOp",EDGE,"E2.13"),subQ1,sQuery(id+"F0.wireOp",EDGE,"E3.1"),sQuery(id+"F0.wireOp",EDGE,"E3.3"),sQuery(id+"F0.wireOp",EDGE,"E3.5"),sQuery(id+"F0.wireOp",EDGE,"E3.7"),sQuery(id+"F0.wireOp",EDGE,"E3.9"),sQuery(id+"F0.wireOp",EDGE,"E3.11"),sQuery(id+"F0.wireOp",EDGE,"E3.13"),sQuery(id+"F0.wireOp",EDGE,"E3.15"),sQuery(id+"F0.wireOp",EDGE,"E4"),sQuery(id+"F0.wireOp",EDGE,"E5"),sQuery(id+"F0.wireOp",EDGE,"E6"),sQuery(id+"F0.wireOp",EDGE,"E7"),subQ0,sQuery(id+"F0.wireOp",EDGE,"E9"),sQuery(id+"F0.wireOp",EDGE,"E10"),sQuery(id+"F0.wireOp",EDGE,"E11"),sQuery(id+"F0.wireOp",EDGE,"E12"),sQuery(id+"F0.wireOp",EDGE,"E13"),sQuery(id+"F0.wireOp",EDGE,"E14"),sQuery(id+"F0.wireOp",EDGE,"E15"),sQuery(id+"F0.wireOp",EDGE,"E16"),sQuery(id+"F0.wireOp",EDGE,"E17"),sQuery(id+"F0.wireOp",EDGE,"E18"),sQuery(id+"F0.wireOp",EDGE,"E19")])],"isStart":true})],"blendedInto":[makeQuery(id+"F1.opExtrude","CAP_FACE",FACE,{"disambiguationData":[OSD([sQuery(id+"F0.wireOp",EDGE,"E0.0"),sQuery(id+"F0.wireOp",EDGE,"E0.1"),sQuery(id+"F0.wireOp",EDGE,"E0.2"),sQuery(id+"F0.wireOp",EDGE,"E0.3"),sQuery(id+"F0.wireOp",EDGE,"E0.4"),sQuery(id+"F0.wireOp",EDGE,"E0.5"),sQuery(id+"F0.wireOp",EDGE,"E0.6"),sQuery(id+"F0.wireOp",EDGE,"E0.7"),sQuery(id+"F0.wireOp",EDGE,"E0.8"),sQuery(id+"F0.wireOp",EDGE,"E0.9"),sQuery(id+"F0.wireOp",EDGE,"E0.10"),sQuery(id+"F0.wireOp",EDGE,"E0.11"),sQuery(id+"F0.wireOp",EDGE,"E0.12"),sQuery(id+"F0.wireOp",EDGE,"E0.13"),sQuery(id+"F0.wireOp",EDGE,"E0.14"),sQuery(id+"F0.wireOp",EDGE,"E0.15"),sQuery(id+"F0.wireOp",EDGE,"E1"),sQuery(id+"F0.wireOp",EDGE,"E2.1"),sQuery(id+"F0.wireOp",EDGE,"E2.3"),sQuery(id+"F0.wireOp",EDGE,"E2.5"),sQuery(id+"F0.wireOp",EDGE,"E2.7"),sQuery(id+"F0.wireOp",EDGE,"E2.9"),sQuery(id+"F0.wireOp",EDGE,"E2.11"),sQuery(id+"F0.wireOp",EDGE,"E2.13"),subQ1,sQuery(id+"F0.wireOp",EDGE,"E3.1"),sQuery(id+"F0.wireOp",EDGE,"E3.3"),sQuery(id+"F0.wireOp",EDGE,"E3.5"),sQuery(id+"F0.wireOp",EDGE,"E3.7"),sQuery(id+"F0.wireOp",EDGE,"E3.9"),sQuery(id+"F0.wireOp",EDGE,"E3.11"),sQuery(id+"F0.wireOp",EDGE,"E3.13"),sQuery(id+"F0.wireOp",EDGE,"E3.15"),sQuery(id+"F0.wireOp",EDGE,"E4"),sQuery(id+"F0.wireOp",EDGE,"E5"),sQuery(id+"F0.wireOp",EDGE,"E6"),sQuery(id+"F0.wireOp",EDGE,"E7"),subQ0,sQuery(id+"F0.wireOp",EDGE,"E9"),sQuery(id+"F0.wireOp",EDGE,"E10"),sQuery(id+"F0.wireOp",EDGE,"E11"),sQuery(id+"F0.wireOp",EDGE,"E12"),sQuery(id+"F0.wireOp",EDGE,"E13"),sQuery(id+"F0.wireOp",EDGE,"E14"),sQuery(id+"F0.wireOp",EDGE,"E15"),sQuery(id+"F0.wireOp",EDGE,"E16"),sQuery(id+"F0.wireOp",EDGE,"E17"),sQuery(id+"F0.wireOp",EDGE,"E18"),sQuery(id+"F0.wireOp",EDGE,"E19")])],"isStart":true})]});}
            var Q63;
            Q63=makeQuery(id+"F1.opExtrude","CAP_EDGE",EDGE,{"disambiguationData":[OSD([sQuery(id+"F0.wireOp",EDGE,"E2.15")])],"isStart":true});
            fillet(context, id + "F6", {"entities" : qUnion([Q0, Q1, Q2, Q3, Q4, Q5, Q6, Q7, Q8, Q9, Q10, Q11, Q12, Q13, Q14, Q15, Q16, Q17, Q18, Q19, Q20, Q21, Q22, Q23, Q24, Q25, Q26, Q27, Q28, Q29, Q30, Q31, Q32, Q33, Q34, Q35, Q36, Q37, Q38, Q39, Q40, Q41, Q42, Q43, Q44, Q45, Q46, Q47, Q48, Q49, Q50, Q51, Q52, Q53, Q54, Q55, Q56, Q57, Q58, Q59, Q60, Q61, Q62, Q63]), "radius" : 2 * mm, "tangentPropagation" : true, "allowEdgeOverflow" : false});
        }
        {
            var Q0;
            Q0=makeQuery(id+"F1.opExtrude","SWEPT_BODY",BODY,{"disambiguationData":[OSD([sQuery(id+"F0.wireOp",EDGE,"E0.0"),sQuery(id+"F0.wireOp",EDGE,"E0.1"),sQuery(id+"F0.wireOp",EDGE,"E0.2"),sQuery(id+"F0.wireOp",EDGE,"E0.3"),sQuery(id+"F0.wireOp",EDGE,"E0.4"),sQuery(id+"F0.wireOp",EDGE,"E0.5"),sQuery(id+"F0.wireOp",EDGE,"E0.6"),sQuery(id+"F0.wireOp",EDGE,"E0.7"),sQuery(id+"F0.wireOp",EDGE,"E0.8"),sQuery(id+"F0.wireOp",EDGE,"E0.9"),sQuery(id+"F0.wireOp",EDGE,"E0.10"),sQuery(id+"F0.wireOp",EDGE,"E0.11"),sQuery(id+"F0.wireOp",EDGE,"E0.12"),sQuery(id+"F0.wireOp",EDGE,"E0.13"),sQuery(id+"F0.wireOp",EDGE,"E0.14"),sQuery(id+"F0.wireOp",EDGE,"E0.15"),sQuery(id+"F0.wireOp",EDGE,"E1"),sQuery(id+"F0.wireOp",EDGE,"E2.1"),sQuery(id+"F0.wireOp",EDGE,"E2.3"),sQuery(id+"F0.wireOp",EDGE,"E2.5"),sQuery(id+"F0.wireOp",EDGE,"E2.7"),sQuery(id+"F0.wireOp",EDGE,"E2.9"),sQuery(id+"F0.wireOp",EDGE,"E2.11"),sQuery(id+"F0.wireOp",EDGE,"E2.13"),sQuery(id+"F0.wireOp",EDGE,"E2.15"),sQuery(id+"F0.wireOp",EDGE,"E3.1"),sQuery(id+"F0.wireOp",EDGE,"E3.3"),sQuery(id+"F0.wireOp",EDGE,"E3.5"),sQuery(id+"F0.wireOp",EDGE,"E3.7"),sQuery(id+"F0.wireOp",EDGE,"E3.9"),sQuery(id+"F0.wireOp",EDGE,"E3.11"),sQuery(id+"F0.wireOp",EDGE,"E3.13"),sQuery(id+"F0.wireOp",EDGE,"E3.15"),sQuery(id+"F0.wireOp",EDGE,"E4"),sQuery(id+"F0.wireOp",EDGE,"E5"),sQuery(id+"F0.wireOp",EDGE,"E6"),sQuery(id+"F0.wireOp",EDGE,"E7"),sQuery(id+"F0.wireOp",EDGE,"E8"),sQuery(id+"F0.wireOp",EDGE,"E9"),sQuery(id+"F0.wireOp",EDGE,"E10"),sQuery(id+"F0.wireOp",EDGE,"E11"),sQuery(id+"F0.wireOp",EDGE,"E12"),sQuery(id+"F0.wireOp",EDGE,"E13"),sQuery(id+"F0.wireOp",EDGE,"E14"),sQuery(id+"F0.wireOp",EDGE,"E15"),sQuery(id+"F0.wireOp",EDGE,"E16"),sQuery(id+"F0.wireOp",EDGE,"E17"),sQuery(id+"F0.wireOp",EDGE,"E18"),sQuery(id+"F0.wireOp",EDGE,"E19")])]});
            var Q1;
            Q1=makeQuery(id+"F1.opExtrude","CAP_FACE",FACE,{"disambiguationData":[OSD([sQuery(id+"F0.wireOp",EDGE,"E0.0"),sQuery(id+"F0.wireOp",EDGE,"E0.1"),sQuery(id+"F0.wireOp",EDGE,"E0.2"),sQuery(id+"F0.wireOp",EDGE,"E0.3"),sQuery(id+"F0.wireOp",EDGE,"E0.4"),sQuery(id+"F0.wireOp",EDGE,"E0.5"),sQuery(id+"F0.wireOp",EDGE,"E0.6"),sQuery(id+"F0.wireOp",EDGE,"E0.7"),sQuery(id+"F0.wireOp",EDGE,"E0.8"),sQuery(id+"F0.wireOp",EDGE,"E0.9"),sQuery(id+"F0.wireOp",EDGE,"E0.10"),sQuery(id+"F0.wireOp",EDGE,"E0.11"),sQuery(id+"F0.wireOp",EDGE,"E0.12"),sQuery(id+"F0.wireOp",EDGE,"E0.13"),sQuery(id+"F0.wireOp",EDGE,"E0.14"),sQuery(id+"F0.wireOp",EDGE,"E0.15"),sQuery(id+"F0.wireOp",EDGE,"E1"),sQuery(id+"F0.wireOp",EDGE,"E2.1"),sQuery(id+"F0.wireOp",EDGE,"E2.3"),sQuery(id+"F0.wireOp",EDGE,"E2.5"),sQuery(id+"F0.wireOp",EDGE,"E2.7"),sQuery(id+"F0.wireOp",EDGE,"E2.9"),sQuery(id+"F0.wireOp",EDGE,"E2.11"),sQuery(id+"F0.wireOp",EDGE,"E2.13"),sQuery(id+"F0.wireOp",EDGE,"E2.15"),sQuery(id+"F0.wireOp",EDGE,"E3.1"),sQuery(id+"F0.wireOp",EDGE,"E3.3"),sQuery(id+"F0.wireOp",EDGE,"E3.5"),sQuery(id+"F0.wireOp",EDGE,"E3.7"),sQuery(id+"F0.wireOp",EDGE,"E3.9"),sQuery(id+"F0.wireOp",EDGE,"E3.11"),sQuery(id+"F0.wireOp",EDGE,"E3.13"),sQuery(id+"F0.wireOp",EDGE,"E3.15"),sQuery(id+"F0.wireOp",EDGE,"E4"),sQuery(id+"F0.wireOp",EDGE,"E5"),sQuery(id+"F0.wireOp",EDGE,"E6"),sQuery(id+"F0.wireOp",EDGE,"E7"),sQuery(id+"F0.wireOp",EDGE,"E8"),sQuery(id+"F0.wireOp",EDGE,"E9"),sQuery(id+"F0.wireOp",EDGE,"E10"),sQuery(id+"F0.wireOp",EDGE,"E11"),sQuery(id+"F0.wireOp",EDGE,"E12"),sQuery(id+"F0.wireOp",EDGE,"E13"),sQuery(id+"F0.wireOp",EDGE,"E14"),sQuery(id+"F0.wireOp",EDGE,"E15"),sQuery(id+"F0.wireOp",EDGE,"E16"),sQuery(id+"F0.wireOp",EDGE,"E17"),sQuery(id+"F0.wireOp",EDGE,"E18"),sQuery(id+"F0.wireOp",EDGE,"E19")])],"isStart":false});
            mirror(context, id + "F7", {"operationType" : NewBodyOperationType.ADD, "entities" : qUnion([Q0]), "mirrorPlane" : qUnion([Q1])});
        }
    });
